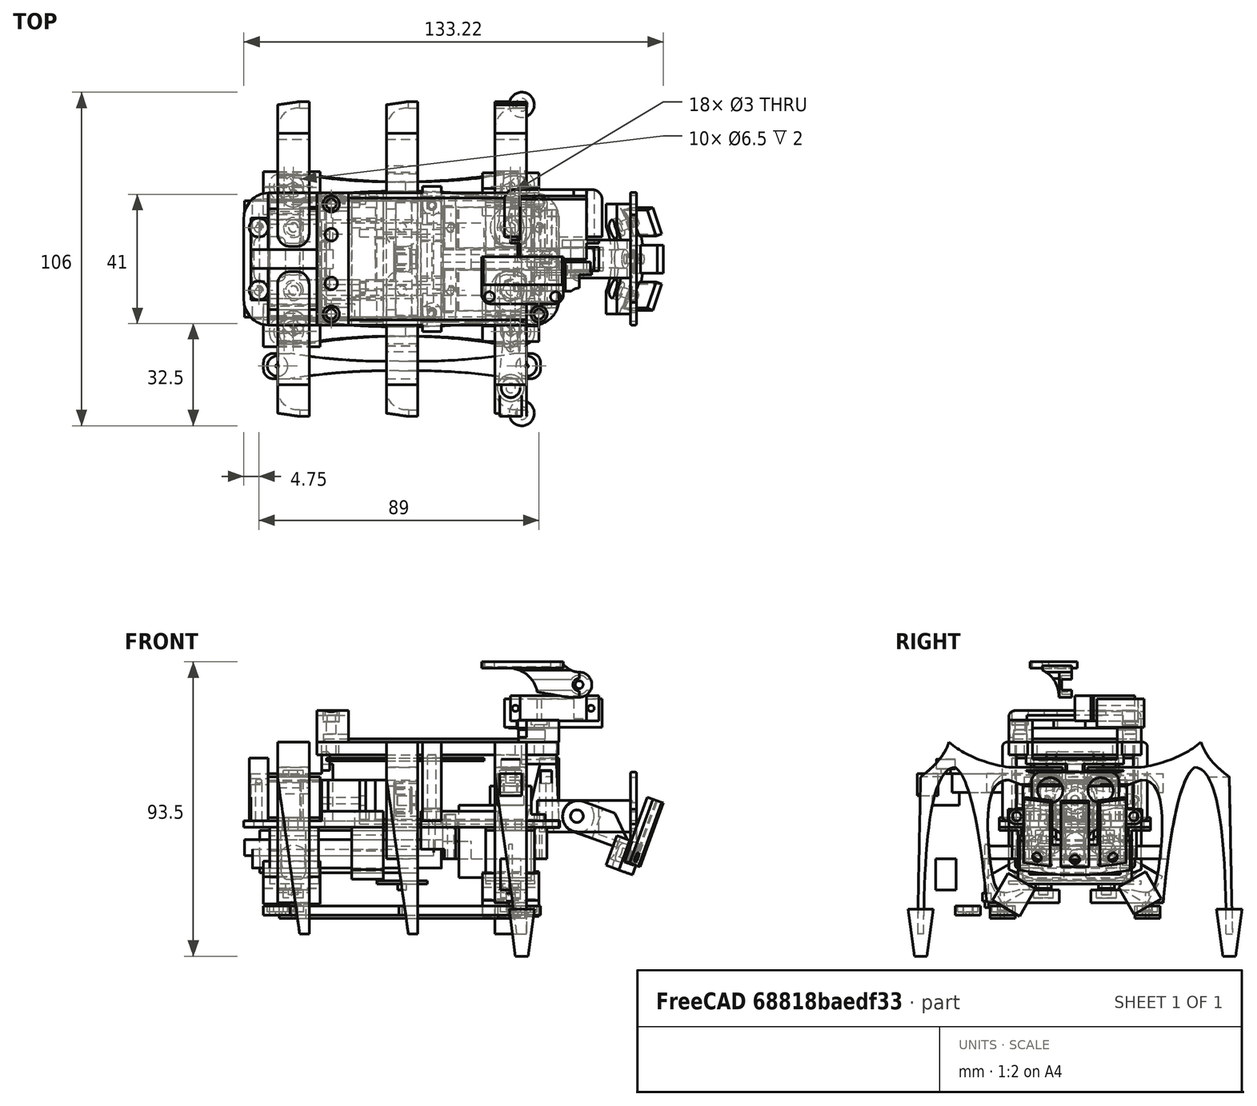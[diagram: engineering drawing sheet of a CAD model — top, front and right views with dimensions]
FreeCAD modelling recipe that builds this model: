
FCSTD DOCUMENT  (FreeCAD 0.20R29410 (Git))
Label: walki_24
License: All rights reserved
LicenseURL: http://en.wikipedia.org/wiki/All_rights_reserved
objects: Part::Cylinder×253, Part::Box×178, Part::MultiFuse×142, Part::Cut×92, Part::Fillet×64, App::DocumentObjectGroup×31, Part::Chamfer×26, Sketcher::SketchObject×17, PartDesign::Pad×17, PartDesign::Body×15, Part::Mirroring×10, Part::Wedge×7, App::Part×3, Part::Cone×2, Image::ImagePlane×1, Part::Feature×1, Part::FeaturePython×1, Mesh::Feature×1
note: 842 computed .brp shape members not serialized (recipe doc carries the construction recipe); baked Part::Feature solids carry a one-line shape summary decoded from their .brp

FEATURE [Part::Box] Box  label="Würfel"
  AttacherType = Attacher::AttachEngine3D
  Height = 23
  Length = 23
  Width = 13
FEATURE [Part::Box] Box001  label="Würfel001"
  AttacherType = Attacher::AttachEngine3D
  Height = 2
  Length = 32
  Placement = pos=(-4.5,0,18) rot=(0,0,1;0rad)
  Width = 13
FEATURE [Part::Cylinder] Cylinder  label="Zylinder"
  Angle = 360
  AttacherType = Attacher::AttachEngine3D
  FirstAngle = 0
  Height = 6
  Placement = pos=(16.5,6.5,23) rot=(0,0,1;0rad)
  Radius = 6.5
  SecondAngle = 0
FEATURE [Part::Cylinder] Cylinder001  label="Zylinder001"
  Angle = 360
  AttacherType = Attacher::AttachEngine3D
  FirstAngle = 0
  Height = 5
  Placement = pos=(16.5,6.5,30) rot=(0,0,1;0rad)
  Radius = 1.5
  SecondAngle = 0
FEATURE [Part::Cylinder] Cylinder002  label="Zylinder002"
  Angle = 360
  AttacherType = Attacher::AttachEngine3D
  FirstAngle = 0
  Height = 10
  Placement = pos=(25.5,6.5,13) rot=(0,0,1;0rad)
  Radius = 1.5
  SecondAngle = 0
FEATURE [Part::Cylinder] Cylinder003  label="Zylinder003"
  Angle = 360
  AttacherType = Attacher::AttachEngine3D
  FirstAngle = 0
  Height = 10
  Placement = pos=(-2.5,6.5,13) rot=(0,0,1;0rad)
  Radius = 1.5
  SecondAngle = 0
FEATURE [Part::Cylinder] Cylinder004  label="Zylinder004"
  Angle = 360
  AttacherType = Attacher::AttachEngine3D
  FirstAngle = 0
  Height = 5
  Placement = pos=(16.5,6.5,29) rot=(0,0,1;0rad)
  Radius = 3.5
  SecondAngle = 0
FEATURE [Part::MultiFuse] Fusion
  Shapes = -> [Cylinder003,Cylinder002,Cylinder001]
FEATURE [Part::MultiFuse] Fusion001
  Shapes = -> [Box,Cylinder004,Box001,Cylinder]
FEATURE [Part::Cut] Cut  label="Servo1"
  Base = -> Fusion001
  Placement = pos=(0,3.5,-25) rot=(0,0,1;0rad)
  Tool = -> Fusion
FEATURE [Part::Box] Box002  label="Würfel002"
  AttacherType = Attacher::AttachEngine3D
  Height = 23
  Length = 23
  Width = 13
FEATURE [Part::Cylinder] Cylinder005  label="Zylinder005"
  Angle = 360
  AttacherType = Attacher::AttachEngine3D
  FirstAngle = 0
  Height = 5
  Placement = pos=(16.5,6.5,30) rot=(0,0,1;0rad)
  Radius = 1.5
  SecondAngle = 0
FEATURE [Part::Cylinder] Cylinder006  label="Zylinder006"
  Angle = 360
  AttacherType = Attacher::AttachEngine3D
  FirstAngle = 0
  Height = 10
  Placement = pos=(-2.5,6.5,13) rot=(0,0,1;0rad)
  Radius = 1.5
  SecondAngle = 0
FEATURE [Part::Cylinder] Cylinder007  label="Zylinder007"
  Angle = 360
  AttacherType = Attacher::AttachEngine3D
  FirstAngle = 0
  Height = 10
  Placement = pos=(25.5,6.5,13) rot=(0,0,1;0rad)
  Radius = 1.5
  SecondAngle = 0
FEATURE [Part::MultiFuse] Fusion003
  Shapes = -> [Cylinder006,Cylinder007,Cylinder005]
FEATURE [Part::Cylinder] Cylinder008  label="Zylinder008"
  Angle = 360
  AttacherType = Attacher::AttachEngine3D
  FirstAngle = 0
  Height = 5
  Placement = pos=(16.5,6.5,29) rot=(0,0,1;0rad)
  Radius = 3.5
  SecondAngle = 0
FEATURE [Part::Box] Box003  label="Würfel003"
  AttacherType = Attacher::AttachEngine3D
  Height = 2
  Length = 32
  Placement = pos=(-4.5,0,18) rot=(0,0,1;0rad)
  Width = 13
FEATURE [Part::Cylinder] Cylinder009  label="Zylinder009"
  Angle = 360
  AttacherType = Attacher::AttachEngine3D
  FirstAngle = 0
  Height = 6
  Placement = pos=(16.5,6.5,23) rot=(0,0,1;0rad)
  Radius = 6.5
  SecondAngle = 0
FEATURE [Part::MultiFuse] Fusion002
  Shapes = -> [Box002,Cylinder008,Box003,Cylinder009]
FEATURE [Part::Cut] Cut001  label="Servo2"
  Base = -> Fusion002
  Placement = pos=(0,-16.5,-25) rot=(0,0,1;0rad)
  Tool = -> Fusion003
FEATURE [Part::Cylinder] Cylinder010  label="Zylinder010"
  Angle = 360
  AttacherType = Attacher::AttachEngine3D
  FirstAngle = 0
  Height = 10
  Placement = pos=(25.5,6.5,13) rot=(0,0,1;0rad)
  Radius = 1.5
  SecondAngle = 0
FEATURE [Part::Cylinder] Cylinder011  label="Zylinder011"
  Angle = 360
  AttacherType = Attacher::AttachEngine3D
  FirstAngle = 0
  Height = 5
  Placement = pos=(16.5,6.5,29) rot=(0,0,1;0rad)
  Radius = 3.5
  SecondAngle = 0
FEATURE [Part::Box] Box004  label="Würfel004"
  AttacherType = Attacher::AttachEngine3D
  Height = 2
  Length = 32
  Placement = pos=(-4.5,0,18) rot=(0,0,1;0rad)
  Width = 13
FEATURE [Part::Cylinder] Cylinder012  label="Zylinder012"
  Angle = 360
  AttacherType = Attacher::AttachEngine3D
  FirstAngle = 0
  Height = 6
  Placement = pos=(16.5,6.5,23) rot=(0,0,1;0rad)
  Radius = 6.5
  SecondAngle = 0
FEATURE [Part::Cylinder] Cylinder013  label="Zylinder013"
  Angle = 360
  AttacherType = Attacher::AttachEngine3D
  FirstAngle = 0
  Height = 5
  Placement = pos=(16.5,6.5,30) rot=(0,0,1;0rad)
  Radius = 1.5
  SecondAngle = 0
FEATURE [Part::Cylinder] Cylinder014  label="Zylinder014"
  Angle = 360
  AttacherType = Attacher::AttachEngine3D
  FirstAngle = 0
  Height = 10
  Placement = pos=(-2.5,6.5,13) rot=(0,0,1;0rad)
  Radius = 1.5
  SecondAngle = 0
FEATURE [Part::MultiFuse] Fusion004
  Shapes = -> [Cylinder014,Cylinder010,Cylinder013]
FEATURE [Part::Box] Box005  label="Würfel005"
  AttacherType = Attacher::AttachEngine3D
  Height = 23
  Length = 23
  Width = 13
FEATURE [Part::MultiFuse] Fusion005
  Shapes = -> [Box005,Cylinder011,Box004,Cylinder012]
FEATURE [Part::Cut] Cut002  label="Servo3"
  Base = -> Fusion005
  Placement = pos=(-49.5,16.5,6) rot=(0.57735,-0.57735,0.57735;4.18879rad)
  Tool = -> Fusion004
FEATURE [Part::Box] Box006  label="Würfel006"
  AttacherType = Attacher::AttachEngine3D
  Height = 18
  Length = 17.5
  Placement = pos=(7.5,-21.5,-28) rot=(0,0,1;0rad)
  Width = 3.5
FEATURE [Part::Box] Box007  label="Base"
  AttacherType = Attacher::AttachEngine3D
  Height = 2
  Length = 100
  Placement = pos=(-68.25,-21,-9) rot=(0,0,1;0rad)
  Width = 42
FEATURE [Part::Cylinder] Cylinder015  label="Zylinder015"
  Angle = 360
  AttacherType = Attacher::AttachEngine3D
  FirstAngle = 0
  Height = 2.5
  Placement = pos=(16.5,10,-29.5) rot=(0,0,1;0rad)
  Radius = 1.4
  SecondAngle = 0
FEATURE [Part::Cylinder] Cylinder016  label="Zylinder016"
  Angle = 360
  AttacherType = Attacher::AttachEngine3D
  FirstAngle = 0
  Height = 2.5
  Placement = pos=(16.5,-10,-29.5) rot=(0,0,1;0rad)
  Radius = 1.4
  SecondAngle = 0
FEATURE [Part::Box] Box008  label="Würfel008"
  AttacherType = Attacher::AttachEngine3D
  Height = 1
  Length = 16
  Placement = pos=(8.5,-21,-27.5) rot=(0,0,1;0rad)
  Width = 42
FEATURE [Part::Cylinder] Cylinder017  label="Zylinder017"
  Angle = 360
  AttacherType = Attacher::AttachEngine3D
  FirstAngle = 0
  Height = 2
  Placement = pos=(16.5,10,-29.5) rot=(0,0,1;0rad)
  Radius = 1.4
  SecondAngle = 0
FEATURE [Part::Cylinder] Cylinder018  label="Zylinder018"
  Angle = 360
  AttacherType = Attacher::AttachEngine3D
  FirstAngle = 0
  Height = 2
  Placement = pos=(16.5,-10,-29.5) rot=(0,0,1;0rad)
  Radius = 1.4
  SecondAngle = 0
FEATURE [Part::MultiFuse] Fusion007
  Placement = pos=(-34.5,0,0.5) rot=(0,0,1;0rad)
  Shapes = -> [Box008,Cylinder017,Cylinder018]
FEATURE [Part::Cylinder] Cylinder021  label="Zylinder021"
  Angle = 360
  AttacherType = Attacher::AttachEngine3D
  FirstAngle = 0
  Height = 2
  Placement = pos=(16.5,10,-26.5) rot=(0,0,1;0rad)
  Radius = 1.4
  SecondAngle = 0
FEATURE [Part::Cylinder] Cylinder022  label="Zylinder022"
  Angle = 360
  AttacherType = Attacher::AttachEngine3D
  FirstAngle = 0
  Height = 2
  Placement = pos=(16.5,-10,-26.5) rot=(0,0,1;0rad)
  Radius = 1.4
  SecondAngle = 0
FEATURE [Part::Box] Box010  label="Würfel010"
  AttacherType = Attacher::AttachEngine3D
  Height = 1
  Length = 16
  Placement = pos=(8.5,-16,-27.5) rot=(0,0,1;0rad)
  Width = 32
FEATURE [Part::Box] Box012  label="Würfel012"
  AttacherType = Attacher::AttachEngine3D
  Height = 14
  Length = 12
  Placement = pos=(-43.5,-21,-8) rot=(0,0,1;0rad)
  Width = 42
FEATURE [Part::Cylinder] Cylinder023  label="Zylinder023"
  Angle = 360
  AttacherType = Attacher::AttachEngine3D
  FirstAngle = 0
  Height = 20
  Placement = pos=(-45,-9,-1.5) rot=(0,1,0;1.5708rad)
  Radius = 1
  SecondAngle = 0
FEATURE [Part::Cylinder] Cylinder024  label="Zylinder024"
  Angle = 360
  AttacherType = Attacher::AttachEngine3D
  FirstAngle = 0
  Height = 20
  Placement = pos=(-45,19,-1.5) rot=(0,1,0;1.5708rad)
  Radius = 1
  SecondAngle = 0
FEATURE [Part::MultiFuse] Fusion010
  Shapes = -> [Cylinder023,Cylinder024]
FEATURE [Part::Cylinder] Cylinder026  label="Zylinder026"
  Angle = 360
  AttacherType = Attacher::AttachEngine3D
  FirstAngle = 0
  Height = 5
  Placement = pos=(16.5,6.5,30) rot=(0,0,1;0rad)
  Radius = 1.5
  SecondAngle = 0
FEATURE [Part::Box] Box014  label="Würfel014"
  AttacherType = Attacher::AttachEngine3D
  Height = 23
  Length = 23
  Width = 13
FEATURE [Part::Cylinder] Cylinder027  label="Zylinder027"
  Angle = 360
  AttacherType = Attacher::AttachEngine3D
  FirstAngle = 0
  Height = 5
  Placement = pos=(16.5,6.5,29) rot=(0,0,1;0rad)
  Radius = 3.5
  SecondAngle = 0
FEATURE [Part::Cylinder] Cylinder028  label="Zylinder028"
  Angle = 360
  AttacherType = Attacher::AttachEngine3D
  FirstAngle = 0
  Height = 6
  Placement = pos=(16.5,6.5,23) rot=(0,0,1;0rad)
  Radius = 6.5
  SecondAngle = 0
FEATURE [Part::Cylinder] Cylinder029  label="Zylinder029"
  Angle = 360
  AttacherType = Attacher::AttachEngine3D
  FirstAngle = 0
  Height = 10
  Placement = pos=(25.5,6.5,13) rot=(0,0,1;0rad)
  Radius = 1.5
  SecondAngle = 0
FEATURE [Part::Cylinder] Cylinder030  label="Zylinder030"
  Angle = 360
  AttacherType = Attacher::AttachEngine3D
  FirstAngle = 0
  Height = 10
  Placement = pos=(-2.5,6.5,13) rot=(0,0,1;0rad)
  Radius = 1.5
  SecondAngle = 0
FEATURE [Part::MultiFuse] Fusion013
  Shapes = -> [Cylinder030,Cylinder029,Cylinder026]
FEATURE [Part::Box] Box015  label="Würfel015"
  AttacherType = Attacher::AttachEngine3D
  Height = 2
  Length = 32
  Placement = pos=(-4.5,0,18) rot=(0,0,1;0rad)
  Width = 13
FEATURE [Part::MultiFuse] Fusion012
  Shapes = -> [Box014,Cylinder027,Box015,Cylinder028]
FEATURE [Part::Cut] Cut005  label="Servo3_mask"
  Base = -> Fusion012
  Placement = pos=(-49.5,16.5,5) rot=(0.57735,-0.57735,0.57735;4.18879rad)
  Tool = -> Fusion013
FEATURE [Part::Box] Box016  label="Würfel016"
  AttacherType = Attacher::AttachEngine3D
  Height = 23
  Length = 23
  Width = 13
FEATURE [Part::Cylinder] Cylinder031  label="Zylinder031"
  Angle = 360
  AttacherType = Attacher::AttachEngine3D
  FirstAngle = 0
  Height = 5
  Placement = pos=(16.5,6.5,30) rot=(0,0,1;0rad)
  Radius = 1.5
  SecondAngle = 0
FEATURE [Part::Cylinder] Cylinder032  label="Zylinder032"
  Angle = 360
  AttacherType = Attacher::AttachEngine3D
  FirstAngle = 0
  Height = 10
  Placement = pos=(-2.5,6.5,13) rot=(0,0,1;0rad)
  Radius = 1.5
  SecondAngle = 0
FEATURE [Part::Cylinder] Cylinder033  label="Zylinder033"
  Angle = 360
  AttacherType = Attacher::AttachEngine3D
  FirstAngle = 0
  Height = 10
  Placement = pos=(25.5,6.5,13) rot=(0,0,1;0rad)
  Radius = 1.5
  SecondAngle = 0
FEATURE [Part::MultiFuse] Fusion015
  Shapes = -> [Cylinder032,Cylinder033,Cylinder031]
FEATURE [Part::Cylinder] Cylinder034  label="Zylinder034"
  Angle = 360
  AttacherType = Attacher::AttachEngine3D
  FirstAngle = 0
  Height = 5
  Placement = pos=(16.5,6.5,29) rot=(0,0,1;0rad)
  Radius = 3.5
  SecondAngle = 0
FEATURE [Part::Box] Box017  label="Würfel017"
  AttacherType = Attacher::AttachEngine3D
  Height = 2
  Length = 32
  Placement = pos=(-4.5,0,18) rot=(0,0,1;0rad)
  Width = 13
FEATURE [Part::Cylinder] Cylinder035  label="Zylinder035"
  Angle = 360
  AttacherType = Attacher::AttachEngine3D
  FirstAngle = 0
  Height = 6
  Placement = pos=(16.5,6.5,23) rot=(0,0,1;0rad)
  Radius = 6.5
  SecondAngle = 0
FEATURE [Part::MultiFuse] Fusion014
  Shapes = -> [Box016,Cylinder034,Box017,Cylinder035]
FEATURE [Part::Cut] Cut007  label="Servo1_mask"
  Base = -> Fusion014
  Placement = pos=(0,3.5,-25) rot=(0,0,1;0rad)
  Tool = -> Fusion015
FEATURE [Part::Cylinder] Cylinder036  label="Zylinder036"
  Angle = 360
  AttacherType = Attacher::AttachEngine3D
  FirstAngle = 0
  Height = 10
  Placement = pos=(25.5,6.5,13) rot=(0,0,1;0rad)
  Radius = 1.5
  SecondAngle = 0
FEATURE [Part::Cylinder] Cylinder037  label="Zylinder037"
  Angle = 360
  AttacherType = Attacher::AttachEngine3D
  FirstAngle = 0
  Height = 5
  Placement = pos=(16.5,6.5,29) rot=(0,0,1;0rad)
  Radius = 3.5
  SecondAngle = 0
FEATURE [Part::Box] Box018  label="Würfel018"
  AttacherType = Attacher::AttachEngine3D
  Height = 2
  Length = 32
  Placement = pos=(-4.5,0,18) rot=(0,0,1;0rad)
  Width = 13
FEATURE [Part::Cylinder] Cylinder038  label="Zylinder038"
  Angle = 360
  AttacherType = Attacher::AttachEngine3D
  FirstAngle = 0
  Height = 6
  Placement = pos=(16.5,6.5,23) rot=(0,0,1;0rad)
  Radius = 6.5
  SecondAngle = 0
FEATURE [Part::Cylinder] Cylinder039  label="Zylinder039"
  Angle = 360
  AttacherType = Attacher::AttachEngine3D
  FirstAngle = 0
  Height = 5
  Placement = pos=(16.5,6.5,30) rot=(0,0,1;0rad)
  Radius = 1.5
  SecondAngle = 0
FEATURE [Part::Cylinder] Cylinder040  label="Zylinder040"
  Angle = 360
  AttacherType = Attacher::AttachEngine3D
  FirstAngle = 0
  Height = 10
  Placement = pos=(-2.5,6.5,13) rot=(0,0,1;0rad)
  Radius = 1.5
  SecondAngle = 0
FEATURE [Part::MultiFuse] Fusion016
  Shapes = -> [Cylinder040,Cylinder036,Cylinder039]
FEATURE [Part::Box] Box019  label="Würfel019"
  AttacherType = Attacher::AttachEngine3D
  Height = 23
  Length = 23
  Width = 13
FEATURE [Part::MultiFuse] Fusion017
  Shapes = -> [Box019,Cylinder037,Box018,Cylinder038]
FEATURE [Part::Cut] Cut008  label="Servo2_mask"
  Base = -> Fusion017
  Placement = pos=(0,-16.5,-25) rot=(0,0,1;0rad)
  Tool = -> Fusion016
FEATURE [Part::Box] Box020  label="Würfel020"
  AttacherType = Attacher::AttachEngine3D
  Height = 18
  Length = 15.5
  Placement = pos=(8.5,-21,-27) rot=(0,0,1;0rad)
  Width = 42
FEATURE [Part::Box] Box021  label="Würfel021"
  AttacherType = Attacher::AttachEngine3D
  Height = 18
  Length = 17.5
  Placement = pos=(7.5,18,-28) rot=(0,0,1;0rad)
  Width = 3.5
FEATURE [Part::MultiFuse] Fusion018
  Shapes = -> [Box006,Box021]
FEATURE [Part::Cut] Cut009
  Base = -> Box020
  Tool = -> Fusion018
FEATURE [Part::Cylinder] Cylinder041  label="Zylinder041"
  Angle = 360
  AttacherType = Attacher::AttachEngine3D
  FirstAngle = 0
  Height = 10
  Placement = pos=(16.5,20.5,-14) rot=(0,0,1;0rad)
  Radius = 1.5
  SecondAngle = 0
FEATURE [Part::Cylinder] Cylinder042  label="Zylinder042"
  Angle = 360
  AttacherType = Attacher::AttachEngine3D
  FirstAngle = 0
  Height = 1
  Placement = pos=(16.5,20.5,-10) rot=(0,0,1;0rad)
  Radius = 3.5
  SecondAngle = 0
FEATURE [Part::Cylinder] Cylinder043  label="Zylinder043"
  Angle = 360
  AttacherType = Attacher::AttachEngine3D
  FirstAngle = 0
  Height = 2
  Placement = pos=(16.5,20.5,-9) rot=(0,0,1;0rad)
  Radius = 3.5
  SecondAngle = 0
FEATURE [Part::Cylinder] Cylinder044  label="Zylinder044"
  Angle = 360
  AttacherType = Attacher::AttachEngine3D
  FirstAngle = 0
  Height = 2
  Placement = pos=(16.5,-20.5,-9) rot=(0,0,1;0rad)
  Radius = 3.5
  SecondAngle = 0
FEATURE [Part::Cylinder] Cylinder045  label="Zylinder045"
  Angle = 360
  AttacherType = Attacher::AttachEngine3D
  FirstAngle = 0
  Height = 1
  Placement = pos=(16.5,-20.5,-10) rot=(0,0,1;0rad)
  Radius = 3.5
  SecondAngle = 0
FEATURE [Part::Cylinder] Cylinder046  label="Zylinder046"
  Angle = 360
  AttacherType = Attacher::AttachEngine3D
  FirstAngle = 0
  Height = 10
  Placement = pos=(16.5,-20.5,-14) rot=(0,0,1;0rad)
  Radius = 1.5
  SecondAngle = 0
FEATURE [Part::MultiFuse] Fusion019
  Shapes = -> [Cylinder045,Cylinder042,Cylinder016,Cylinder015]
FEATURE [Part::Cylinder] Cylinder047  label="Zylinder047"
  Angle = 360
  AttacherType = Attacher::AttachEngine3D
  FirstAngle = 0
  Height = 10
  Placement = pos=(16.5,-20.5,-14) rot=(0,0,1;0rad)
  Radius = 1.5
  SecondAngle = 0
FEATURE [Part::Cylinder] Cylinder048  label="Zylinder048"
  Angle = 360
  AttacherType = Attacher::AttachEngine3D
  FirstAngle = 0
  Height = 10
  Placement = pos=(16.5,20.5,-14) rot=(0,0,1;0rad)
  Radius = 1.5
  SecondAngle = 0
FEATURE [Part::Box] Box022  label="Würfel022"
  AttacherType = Attacher::AttachEngine3D
  Height = 21
  Length = 22
  Placement = pos=(1,-4,-26) rot=(0,0,1;0rad)
  Width = 8
FEATURE [Part::MultiFuse] Fusion021
  Shapes = -> [Cylinder041,Cylinder046,Box022]
FEATURE [Part::MultiFuse] Fusion022
  Shapes = -> [Cut007,Cut008]
FEATURE [Part::Box] Box023  label="Würfel023"
  AttacherType = Attacher::AttachEngine3D
  Height = 2
  Length = 32
  Placement = pos=(-4.5,0,18) rot=(0,0,1;0rad)
  Width = 13
FEATURE [Part::Box] Box024  label="Würfel024"
  AttacherType = Attacher::AttachEngine3D
  Height = 2
  Length = 32
  Placement = pos=(-4.5,0,18) rot=(0,0,1;0rad)
  Width = 13
FEATURE [Part::Cylinder] Cylinder049  label="Zylinder049"
  Angle = 360
  AttacherType = Attacher::AttachEngine3D
  FirstAngle = 0
  Height = 5
  Placement = pos=(16.5,6.5,29) rot=(0,0,1;0rad)
  Radius = 3.5
  SecondAngle = 0
FEATURE [Part::Cylinder] Cylinder050  label="Zylinder050"
  Angle = 360
  AttacherType = Attacher::AttachEngine3D
  FirstAngle = 0
  Height = 10
  Placement = pos=(-2.5,6.5,13) rot=(0,0,1;0rad)
  Radius = 1.5
  SecondAngle = 0
FEATURE [Part::Cylinder] Cylinder051  label="Zylinder051"
  Angle = 360
  AttacherType = Attacher::AttachEngine3D
  FirstAngle = 0
  Height = 10
  Placement = pos=(25.5,6.5,13) rot=(0,0,1;0rad)
  Radius = 1.5
  SecondAngle = 0
FEATURE [Part::Box] Box025  label="Würfel025"
  AttacherType = Attacher::AttachEngine3D
  Height = 23
  Length = 23
  Width = 13
FEATURE [Part::Cylinder] Cylinder052  label="Zylinder052"
  Angle = 360
  AttacherType = Attacher::AttachEngine3D
  FirstAngle = 0
  Height = 5
  Placement = pos=(16.5,6.5,30) rot=(0,0,1;0rad)
  Radius = 1.5
  SecondAngle = 0
FEATURE [Part::Cylinder] Cylinder053  label="Zylinder053"
  Angle = 360
  AttacherType = Attacher::AttachEngine3D
  FirstAngle = 0
  Height = 6
  Placement = pos=(16.5,6.5,23) rot=(0,0,1;0rad)
  Radius = 6.5
  SecondAngle = 0
FEATURE [Part::Cylinder] Cylinder054  label="Zylinder054"
  Angle = 360
  AttacherType = Attacher::AttachEngine3D
  FirstAngle = 0
  Height = 5
  Placement = pos=(16.5,6.5,29) rot=(0,0,1;0rad)
  Radius = 3.5
  SecondAngle = 0
FEATURE [Part::Cylinder] Cylinder055  label="Zylinder055"
  Angle = 360
  AttacherType = Attacher::AttachEngine3D
  FirstAngle = 0
  Height = 6
  Placement = pos=(16.5,6.5,23) rot=(0,0,1;0rad)
  Radius = 6.5
  SecondAngle = 0
FEATURE [Part::Cylinder] Cylinder056  label="Zylinder056"
  Angle = 360
  AttacherType = Attacher::AttachEngine3D
  FirstAngle = 0
  Height = 10
  Placement = pos=(25.5,6.5,13) rot=(0,0,1;0rad)
  Radius = 1.5
  SecondAngle = 0
FEATURE [Part::Cylinder] Cylinder057  label="Zylinder057"
  Angle = 360
  AttacherType = Attacher::AttachEngine3D
  FirstAngle = 0
  Height = 10
  Placement = pos=(-2.5,6.5,13) rot=(0,0,1;0rad)
  Radius = 1.5
  SecondAngle = 0
FEATURE [Part::Box] Box026  label="Würfel026"
  AttacherType = Attacher::AttachEngine3D
  Height = 23
  Length = 23
  Width = 13
FEATURE [Part::Cylinder] Cylinder058  label="Zylinder058"
  Angle = 360
  AttacherType = Attacher::AttachEngine3D
  FirstAngle = 0
  Height = 5
  Placement = pos=(16.5,6.5,30) rot=(0,0,1;0rad)
  Radius = 1.5
  SecondAngle = 0
FEATURE [Part::MultiFuse] Fusion024
  Shapes = -> [Box025,Cylinder054,Box024,Cylinder055]
FEATURE [Part::MultiFuse] Fusion025
  Shapes = -> [Cylinder050,Cylinder051,Cylinder052]
FEATURE [Part::Cut] Cut012  label="Servo2_mask001"
  Base = -> Fusion024
  Placement = pos=(0,-16.5,-26) rot=(0,0,1;0rad)
  Tool = -> Fusion025
FEATURE [Part::MultiFuse] Fusion026
  Shapes = -> [Cylinder057,Cylinder056,Cylinder058]
FEATURE [Part::MultiFuse] Fusion027
  Shapes = -> [Box026,Cylinder049,Box023,Cylinder053]
FEATURE [Part::Cut] Cut011  label="Servo1_mask001"
  Base = -> Fusion027
  Placement = pos=(0,3.5,-26) rot=(0,0,1;0rad)
  Tool = -> Fusion026
FEATURE [Part::MultiFuse] Fusion023
  Shapes = -> [Cut011,Cut012]
FEATURE [Part::Box] Box028  label="Würfel028"
  AttacherType = Attacher::AttachEngine3D
  Height = 18
  Length = 17.5
  Placement = pos=(7.5,-21.5,-28) rot=(0,0,1;0rad)
  Width = 3.5
FEATURE [Part::Cylinder] Cylinder059  label="Zylinder059"
  Angle = 360
  AttacherType = Attacher::AttachEngine3D
  FirstAngle = 0
  Height = 2.5
  Placement = pos=(16.5,10,-29.5) rot=(0,0,1;0rad)
  Radius = 1.4
  SecondAngle = 0
FEATURE [Part::Cylinder] Cylinder060  label="Zylinder060"
  Angle = 360
  AttacherType = Attacher::AttachEngine3D
  FirstAngle = 0
  Height = 2.5
  Placement = pos=(16.5,-10,-29.5) rot=(0,0,1;0rad)
  Radius = 1.4
  SecondAngle = 0
FEATURE [Part::Cylinder] Cylinder061  label="Zylinder061"
  Angle = 360
  AttacherType = Attacher::AttachEngine3D
  FirstAngle = 0
  Height = 5
  Placement = pos=(16.5,6.5,29) rot=(0,0,1;0rad)
  Radius = 3.5
  SecondAngle = 0
FEATURE [Part::Box] Box029  label="Würfel029"
  AttacherType = Attacher::AttachEngine3D
  Height = 23
  Length = 23
  Width = 13
FEATURE [Part::Cylinder] Cylinder062  label="Zylinder062"
  Angle = 360
  AttacherType = Attacher::AttachEngine3D
  FirstAngle = 0
  Height = 6
  Placement = pos=(16.5,6.5,23) rot=(0,0,1;0rad)
  Radius = 6.5
  SecondAngle = 0
FEATURE [Part::Cylinder] Cylinder063  label="Zylinder063"
  Angle = 360
  AttacherType = Attacher::AttachEngine3D
  FirstAngle = 0
  Height = 5
  Placement = pos=(16.5,6.5,29) rot=(0,0,1;0rad)
  Radius = 3.5
  SecondAngle = 0
FEATURE [Part::Box] Box030  label="Würfel030"
  AttacherType = Attacher::AttachEngine3D
  Height = 18
  Length = 17.5
  Placement = pos=(7.5,18,-28) rot=(0,0,1;0rad)
  Width = 3.5
FEATURE [Part::Box] Box031  label="Würfel031"
  AttacherType = Attacher::AttachEngine3D
  Height = 2
  Length = 32
  Placement = pos=(-4.5,0,18) rot=(0,0,1;0rad)
  Width = 13
FEATURE [Part::Cylinder] Cylinder064  label="Zylinder064"
  Angle = 360
  AttacherType = Attacher::AttachEngine3D
  FirstAngle = 0
  Height = 10
  Placement = pos=(16.5,-20.5,-14) rot=(0,0,1;0rad)
  Radius = 1.5
  SecondAngle = 0
FEATURE [Part::Box] Box032  label="Würfel032"
  AttacherType = Attacher::AttachEngine3D
  Height = 2
  Length = 32
  Placement = pos=(-4.5,0,18) rot=(0,0,1;0rad)
  Width = 13
FEATURE [Part::Cylinder] Cylinder065  label="Zylinder065"
  Angle = 360
  AttacherType = Attacher::AttachEngine3D
  FirstAngle = 0
  Height = 10
  Placement = pos=(25.5,6.5,13) rot=(0,0,1;0rad)
  Radius = 1.5
  SecondAngle = 0
FEATURE [Part::Cylinder] Cylinder066  label="Zylinder066"
  Angle = 360
  AttacherType = Attacher::AttachEngine3D
  FirstAngle = 0
  Height = 10
  Placement = pos=(16.5,20.5,-14) rot=(0,0,1;0rad)
  Radius = 1.5
  SecondAngle = 0
FEATURE [Part::Cylinder] Cylinder067  label="Zylinder067"
  Angle = 360
  AttacherType = Attacher::AttachEngine3D
  FirstAngle = 0
  Height = 10
  Placement = pos=(25.5,6.5,13) rot=(0,0,1;0rad)
  Radius = 1.5
  SecondAngle = 0
FEATURE [Part::Cylinder] Cylinder068  label="Zylinder068"
  Angle = 360
  AttacherType = Attacher::AttachEngine3D
  FirstAngle = 0
  Height = 1
  Placement = pos=(16.5,20.5,-10) rot=(0,0,1;0rad)
  Radius = 3.5
  SecondAngle = 0
FEATURE [Part::Cylinder] Cylinder069  label="Zylinder069"
  Angle = 360
  AttacherType = Attacher::AttachEngine3D
  FirstAngle = 0
  Height = 10
  Placement = pos=(-2.5,6.5,13) rot=(0,0,1;0rad)
  Radius = 1.5
  SecondAngle = 0
FEATURE [Part::Box] Box033  label="Würfel033"
  AttacherType = Attacher::AttachEngine3D
  Height = 23
  Length = 23
  Width = 13
FEATURE [Part::Cylinder] Cylinder070  label="Zylinder070"
  Angle = 360
  AttacherType = Attacher::AttachEngine3D
  FirstAngle = 0
  Height = 10
  Placement = pos=(-2.5,6.5,13) rot=(0,0,1;0rad)
  Radius = 1.5
  SecondAngle = 0
FEATURE [Part::Box] Box036  label="Würfel036"
  AttacherType = Attacher::AttachEngine3D
  Height = 18
  Length = 15.5
  Placement = pos=(-60,-21,-27) rot=(0,0,1;0rad)
  Width = 42
FEATURE [Part::Cylinder] Cylinder071  label="Zylinder071"
  Angle = 360
  AttacherType = Attacher::AttachEngine3D
  FirstAngle = 0
  Height = 5
  Placement = pos=(16.5,6.5,30) rot=(0,0,1;0rad)
  Radius = 1.5
  SecondAngle = 0
FEATURE [Part::Cylinder] Cylinder072  label="Zylinder072"
  Angle = 360
  AttacherType = Attacher::AttachEngine3D
  FirstAngle = 0
  Height = 1
  Placement = pos=(16.5,-20.5,-10) rot=(0,0,1;0rad)
  Radius = 3.5
  SecondAngle = 0
FEATURE [Part::Cylinder] Cylinder073  label="Zylinder073"
  Angle = 360
  AttacherType = Attacher::AttachEngine3D
  FirstAngle = 0
  Height = 6
  Placement = pos=(16.5,6.5,23) rot=(0,0,1;0rad)
  Radius = 6.5
  SecondAngle = 0
FEATURE [Part::Cylinder] Cylinder074  label="Zylinder074"
  Angle = 360
  AttacherType = Attacher::AttachEngine3D
  FirstAngle = 0
  Height = 5
  Placement = pos=(16.5,6.5,30) rot=(0,0,1;0rad)
  Radius = 1.5
  SecondAngle = 0
FEATURE [Part::MultiFuse] Fusion030
  Placement = pos=(-69,0,0) rot=(0,0,1;0rad)
  Shapes = -> [Cylinder072,Cylinder068,Cylinder060,Cylinder059]
FEATURE [Part::MultiFuse] Fusion033
  Shapes = -> [Box033,Cylinder061,Box032,Cylinder073]
FEATURE [Part::MultiFuse] Fusion034
  Shapes = -> [Box029,Cylinder063,Box031,Cylinder062]
FEATURE [Part::MultiFuse] Fusion035
  Shapes = -> [Cylinder069,Cylinder067,Cylinder071]
FEATURE [Part::Cut] Cut021  label="Servo2_mask002"
  Base = -> Fusion033
  Placement = pos=(0,-16.5,-26) rot=(0,0,1;0rad)
  Tool = -> Fusion035
FEATURE [Part::MultiFuse] Fusion036
  Shapes = -> [Cylinder070,Cylinder065,Cylinder074]
FEATURE [Part::Cut] Cut016  label="Servo1_mask002"
  Base = -> Fusion034
  Placement = pos=(0,3.5,-26) rot=(0,0,1;0rad)
  Tool = -> Fusion036
FEATURE [Part::MultiFuse] Fusion032
  Shapes = -> [Cut016,Cut021]
FEATURE [Part::MultiFuse] Fusion037
  Placement = pos=(-68.5,0,0) rot=(0,0,1;0rad)
  Shapes = -> [Box028,Box030]
FEATURE [Part::Box] Box035  label="Würfel035"
  AttacherType = Attacher::AttachEngine3D
  Height = 15
  Length = 10
  Placement = pos=(22,-14.5,-24) rot=(0,0,1;0rad)
  Width = 29
FEATURE [Part::Cylinder] Cylinder075  label="Zylinder075"
  Angle = 360
  AttacherType = Attacher::AttachEngine3D
  FirstAngle = 0
  Height = 10
  Placement = pos=(-52.5,-20.5,-14) rot=(0,0,1;0rad)
  Radius = 1.5
  SecondAngle = 0
FEATURE [Part::Cylinder] Cylinder076  label="Zylinder076"
  Angle = 360
  AttacherType = Attacher::AttachEngine3D
  FirstAngle = 0
  Height = 10
  Placement = pos=(-52.5,20.5,-14) rot=(0,0,1;0rad)
  Radius = 1.5
  SecondAngle = 0
FEATURE [Part::Cylinder] Cylinder077  label="Zylinder077"
  Angle = 360
  AttacherType = Attacher::AttachEngine3D
  FirstAngle = 0
  Height = 2
  Placement = pos=(-52.5,20.5,-9) rot=(0,0,1;0rad)
  Radius = 3.5
  SecondAngle = 0
FEATURE [Part::Cylinder] Cylinder078  label="Zylinder078"
  Angle = 360
  AttacherType = Attacher::AttachEngine3D
  FirstAngle = 0
  Height = 2
  Placement = pos=(-52.5,-20.5,-9) rot=(0,0,1;0rad)
  Radius = 3.5
  SecondAngle = 0
FEATURE [Part::Cylinder] Cylinder079  label="Zylinder079"
  Angle = 360
  AttacherType = Attacher::AttachEngine3D
  FirstAngle = 0
  Height = 10
  Placement = pos=(-2.5,10,-13) rot=(0,0,1;0rad)
  Radius = 1.4
  SecondAngle = 0
FEATURE [Part::Cylinder] Cylinder080  label="Zylinder080"
  Angle = 360
  AttacherType = Attacher::AttachEngine3D
  FirstAngle = 0
  Height = 10
  Placement = pos=(25.5,10,-13) rot=(0,0,1;0rad)
  Radius = 1.4
  SecondAngle = 0
FEATURE [Part::Cylinder] Cylinder081  label="Zylinder081"
  Angle = 360
  AttacherType = Attacher::AttachEngine3D
  FirstAngle = 0
  Height = 10
  Placement = pos=(25.5,-10,-13) rot=(0,0,1;0rad)
  Radius = 1.4
  SecondAngle = 0
FEATURE [Part::Cylinder] Cylinder082  label="Zylinder082"
  Angle = 360
  AttacherType = Attacher::AttachEngine3D
  FirstAngle = 0
  Height = 10
  Placement = pos=(-2.5,-10,-13) rot=(0,0,1;0rad)
  Radius = 1.4
  SecondAngle = 0
FEATURE [Part::MultiFuse] Fusion039
  Shapes = -> [Cylinder081,Cylinder080,Cylinder082,Cylinder079,Cylinder075,Cylinder076,Cylinder047,Cylinder048]
FEATURE [Part::MultiFuse] Fusion040
  Shapes = -> [Fusion022,Fusion039]
FEATURE [Part::MultiFuse] Fusion041
  Shapes = -> [Cylinder043,Cylinder044,Box007,Cylinder077,Cylinder078]
FEATURE [Part::Cut] Cut026
  Base = -> Fusion041
  Tool = -> Fusion040
FEATURE [App::DocumentObjectGroup] Gruppe  label="Servos"
  Group = -> [Cut,Cut001,Cut002]
FEATURE [Part::Box] Box038  label="Würfel038"
  AttacherType = Attacher::AttachEngine3D
  Height = 3
  Length = 56
  Placement = pos=(-43.5,20,-7) rot=(0,0,1;0rad)
  Width = 1
FEATURE [Part::Box] Box039  label="Würfel039"
  AttacherType = Attacher::AttachEngine3D
  Height = 3
  Length = 56
  Placement = pos=(-43.5,-21,-7) rot=(0,0,1;0rad)
  Width = 1
FEATURE [Part::Box] Box040  label="Würfel040"
  AttacherType = Attacher::AttachEngine3D
  Height = 10
  Length = 12
  Placement = pos=(-24,-21.5,-11) rot=(0,0,1;0rad)
  Width = 13
FEATURE [Part::Box] Box041  label="Würfel041"
  AttacherType = Attacher::AttachEngine3D
  Height = 10
  Length = 12
  Placement = pos=(-24,8.5,-11) rot=(0,0,1;0rad)
  Width = 13
FEATURE [Part::MultiFuse] Fusion042
  Shapes = -> [Box038,Box039]
FEATURE [Part::MultiFuse] Fusion043
  Shapes = -> [Cut026,Fusion042]
FEATURE [Part::MultiFuse] Fusion044
  Shapes = -> [Box040,Box041]
FEATURE [Part::Cylinder] Cylinder083  label="Zylinder083"
  Angle = 360
  AttacherType = Attacher::AttachEngine3D
  FirstAngle = 0
  Height = 1
  Placement = pos=(-52.5,-20.5,-8) rot=(0,0,1;0rad)
  Radius = 3.5
  SecondAngle = 0
FEATURE [Part::Cylinder] Cylinder084  label="Zylinder084"
  Angle = 360
  AttacherType = Attacher::AttachEngine3D
  FirstAngle = 0
  Height = 1
  Placement = pos=(-52.5,20.5,-8) rot=(0,0,1;0rad)
  Radius = 3.5
  SecondAngle = 0
FEATURE [Part::Cylinder] Cylinder085  label="Zylinder085"
  Angle = 360
  AttacherType = Attacher::AttachEngine3D
  FirstAngle = 0
  Height = 4
  Placement = pos=(-52.5,-20.5,-9.5) rot=(0,0,1;0rad)
  Radius = 1.4
  SecondAngle = 0
FEATURE [Part::Cylinder] Cylinder086  label="Zylinder086"
  Angle = 360
  AttacherType = Attacher::AttachEngine3D
  FirstAngle = 0
  Height = 4
  Placement = pos=(-52.5,20.5,-9.5) rot=(0,0,1;0rad)
  Radius = 1.4
  SecondAngle = 0
FEATURE [Part::MultiFuse] Fusion009
  Placement = pos=(-69,0,32.5) rot=(0,0,1;0rad)
  Shapes = -> [Box010,Cylinder021,Cylinder022]
FEATURE [Part::Box] Box042  label="Würfel042"
  AttacherType = Attacher::AttachEngine3D
  Height = 14
  Length = 16.5
  Placement = pos=(-60.5,-21,-8) rot=(0,0,1;0rad)
  Width = 42
FEATURE [Part::Box] Box043  label="Würfel043"
  AttacherType = Attacher::AttachEngine3D
  Height = 12.5
  Length = 18
  Placement = pos=(-61.5,-14.5,-8) rot=(0,0,1;0rad)
  Width = 29
FEATURE [Part::Box] Box044  label="Würfel044"
  AttacherType = Attacher::AttachEngine3D
  Height = 17
  Length = 18
  Placement = pos=(-61.5,-22,-7) rot=(0,0,1;0rad)
  Width = 6
FEATURE [Part::Box] Box045  label="Würfel045"
  AttacherType = Attacher::AttachEngine3D
  Height = 17
  Length = 18
  Placement = pos=(-61.5,16,-7) rot=(0,0,1;0rad)
  Width = 6
FEATURE [Part::MultiFuse] Fusion046
  Shapes = -> [Cylinder083,Cylinder084,Box042,Fusion009]
FEATURE [Part::MultiFuse] Fusion047
  Shapes = -> [Cylinder085,Cylinder086,Box043,Box044,Box045]
FEATURE [Part::Cylinder] Cylinder087  label="Zylinder087"
  Angle = 360
  AttacherType = Attacher::AttachEngine3D
  FirstAngle = 0
  Height = 10
  Placement = pos=(16.5,10,-31.5) rot=(0,0,1;0rad)
  Radius = 3.15
  SecondAngle = 0
FEATURE [Part::Cylinder] Cylinder088  label="Zylinder088"
  Angle = 360
  AttacherType = Attacher::AttachEngine3D
  FirstAngle = 0
  Height = 10
  Placement = pos=(16.5,10,-2) rot=(0,0,1;0rad)
  Radius = 4.25
  SecondAngle = 0
FEATURE [Part::Wedge] Wedge  label="Keil"
  AttacherType = Attacher::AttachEngine3D
  Placement = pos=(12.5,10,0) rot=(0,0,1;0rad)
  X2max = 6
  X2min = 2
  Xmax = 8
  Xmin = 0
  Ymax = 18
  Ymin = 0
  Z2max = 8
  Z2min = 2
  Zmax = 8
  Zmin = 2
FEATURE [Part::Box] Box046  label="Würfel046"
  AttacherType = Attacher::AttachEngine3D
  Height = 7
  Length = 7
  Placement = pos=(13,1,1) rot=(0,0,1;0rad)
  Width = 9
FEATURE [Part::Cylinder] Cylinder089  label="Zylinder089"
  Angle = 360
  AttacherType = Attacher::AttachEngine3D
  FirstAngle = 0
  Height = 14
  Placement = pos=(16.5,10,-2) rot=(0,0,1;0rad)
  Radius = 1.5
  SecondAngle = 0
FEATURE [Part::Cylinder] Cylinder090  label="Zylinder090"
  Angle = 360
  AttacherType = Attacher::AttachEngine3D
  FirstAngle = 0
  Height = 3
  Placement = pos=(16.5,10,9.5) rot=(0,0,1;0rad)
  Radius = 3
  SecondAngle = 0
FEATURE [Part::MultiFuse] Fusion048
  Shapes = -> [Cylinder087,Cylinder088,Wedge,Box046,Cylinder089,Cylinder090]
FEATURE [Part::Cylinder] Cylinder092  label="Zylinder092"
  Angle = 360
  AttacherType = Attacher::AttachEngine3D
  FirstAngle = 0
  Height = 10
  Placement = pos=(-52.5,10,-1) rot=(0,0,1;0rad)
  Radius = 3.15
  SecondAngle = 0
FEATURE [Part::Cylinder] Cylinder093  label="Zylinder093"
  Angle = 360
  AttacherType = Attacher::AttachEngine3D
  FirstAngle = 0
  Height = 10
  Placement = pos=(-52.5,10,-31.5) rot=(0,0,1;0rad)
  Radius = 3.15
  SecondAngle = 0
FEATURE [Part::Box] Box047  label="Würfel047"
  AttacherType = Attacher::AttachEngine3D
  Height = 10
  Length = 12
  Placement = pos=(-58.5,3.5,-2.5) rot=(0,0,1;0rad)
  Width = 23
FEATURE [Part::Box] Box048  label="Würfel048"
  AttacherType = Attacher::AttachEngine3D
  Height = 10
  Length = 18
  Placement = pos=(-62,14.134,-28.366) rot=(-1,0,0;0.523599rad)
  Width = 10
FEATURE [Part::Box] Box049  label="Würfel049"
  AttacherType = Attacher::AttachEngine3D
  Height = 10
  Length = 18
  Placement = pos=(-62,-22.933,-33.4462) rot=(1,0,0;0.523599rad)
  Width = 10
FEATURE [Part::Box] Box050  label="Würfel050"
  AttacherType = Attacher::AttachEngine3D
  Height = 10
  Length = 18
  Placement = pos=(7.5,13.7625,-28.0795) rot=(-1,0,0;1.0472rad)
  Width = 10
FEATURE [Part::Box] Box051  label="Würfel051"
  AttacherType = Attacher::AttachEngine3D
  Height = 10
  Length = 18
  Placement = pos=(7.5,-26.207,-32.3052) rot=(-1,0,0;0.523599rad)
  Width = 10
FEATURE [Part::MultiFuse] Fusion051
  Shapes = -> [Box051,Box050]
FEATURE [Part::Box] Box053  label="Würfel053"
  AttacherType = Attacher::AttachEngine3D
  Height = 10
  Length = 3
  Placement = pos=(-31.5,-10,-8) rot=(0,0,1;0rad)
  Width = 33
FEATURE [Part::Box] Box054  label="Würfel054"
  AttacherType = Attacher::AttachEngine3D
  Height = 10
  Length = 24
  Placement = pos=(-0.5,3.5,-12.5) rot=(0,0,1;0rad)
  Width = 13
FEATURE [Part::Box] Box055  label="Würfel055"
  AttacherType = Attacher::AttachEngine3D
  Height = 10
  Length = 24
  Placement = pos=(-0.5,-16.5,-12.5) rot=(0,0,1;0rad)
  Width = 13
FEATURE [Part::Box] Box057  label="Würfel057"
  AttacherType = Attacher::AttachEngine3D
  Height = 1.5
  Length = 26
  Placement = pos=(-31.5,7,-8) rot=(0,0,1;0rad)
  Width = 2.5
FEATURE [Part::Box] Box058  label="Würfel058"
  AttacherType = Attacher::AttachEngine3D
  Height = 1.5
  Length = 26
  Placement = pos=(-31.5,-9.5,-8) rot=(0,0,1;0rad)
  Width = 2.5
FEATURE [Part::Box] Box059  label="Würfel059"
  AttacherType = Attacher::AttachEngine3D
  Height = 1.5
  Length = 3
  Placement = pos=(-8.5,-9.5,-8) rot=(0,0,1;0rad)
  Width = 19
FEATURE [Part::Box] Box060  label="Würfel060"
  AttacherType = Attacher::AttachEngine3D
  Height = 1.5
  Length = 33.2
  Placement = pos=(-5.75,-1,-8) rot=(0,0,1;0rad)
  Width = 2.5
FEATURE [Sketcher::SketchObject] Sketch
  FullyConstrained = false
  MapMode = 5
  Placement = pos=(0,0,0) rot=(0.57735,0.57735,0.57735;2.0944rad)
  Support = -> [YZ_Plane]
  sketch-geometry (50):
    g0: LineSegment StartX=4 StartY=4 StartZ=0 EndX=4 EndY=10 EndZ=0
    g1: LineSegment StartX=4 StartY=10 StartZ=0 EndX=21 EndY=10 EndZ=0
    g2: LineSegment StartX=5 StartY=-29 StartZ=0 EndX=18 EndY=-29 EndZ=0
    g3: LineSegment StartX=5 StartY=-29 StartZ=0 EndX=5 EndY=-33 EndZ=0
    g4: LineSegment StartX=5 StartY=-33 StartZ=0 EndX=28 EndY=-33 EndZ=0
    g5: LineSegment StartX=4 StartY=4 StartZ=0 EndX=16 EndY=4 EndZ=0
    g6: LineSegment StartX=16 StartY=4 StartZ=0 EndX=21 EndY=6 EndZ=0
    g7: Circle CenterX=21 CenterY=10 CenterZ=0 NormalX=0 NormalY=0 NormalZ=1 AngleXU=0 Radius=2
    g8: Circle CenterX=33 CenterY=12 CenterZ=0 NormalX=0 NormalY=0 NormalZ=1 AngleXU=0 Radius=2
    g9: Circle CenterX=40 CenterY=18 CenterZ=0 NormalX=0 NormalY=0 NormalZ=1 AngleXU=0 Radius=2
    g10: BSplineCurve PolesCount=3 KnotsCount=2 Degree=2 IsPeriodic=0
    g11: GeomPoint X=21 Y=10 Z=0
    g12: GeomPoint X=40 Y=18 Z=0
    g13: Circle CenterX=40 CenterY=18 CenterZ=0 NormalX=0 NormalY=0 NormalZ=1 AngleXU=0 Radius=1
    g14: Circle CenterX=42 CenterY=12 CenterZ=0 NormalX=0 NormalY=0 NormalZ=1 AngleXU=0 Radius=1
    g15: Circle CenterX=49 CenterY=7 CenterZ=0 NormalX=0 NormalY=0 NormalZ=1 AngleXU=0 Radius=1
    g16: BSplineCurve PolesCount=3 KnotsCount=2 Degree=2 IsPeriodic=0
    g17: GeomPoint X=40 Y=18 Z=0
    g18: GeomPoint X=49 Y=7 Z=0
    g19: Circle CenterX=49 CenterY=7 CenterZ=0 NormalX=0 NormalY=0 NormalZ=1 AngleXU=0 Radius=8
    g20: Circle CenterX=50 CenterY=-43 CenterZ=0 NormalX=0 NormalY=0 NormalZ=1 AngleXU=0 Radius=8
    g21: BSplineCurve PolesCount=2 KnotsCount=2 Degree=1 IsPeriodic=0
    g22: GeomPoint X=49 Y=7 Z=0
    g23: GeomPoint X=50 Y=-43 Z=0
    g24: Circle CenterX=48 CenterY=-43 CenterZ=0 NormalX=0 NormalY=0 NormalZ=1 AngleXU=0 Radius=8
    g25: Circle CenterX=48 CenterY=10 CenterZ=0 NormalX=0 NormalY=0 NormalZ=1 AngleXU=0 Radius=8
    g26: Circle CenterX=38 CenterY=10 CenterZ=0 NormalX=0 NormalY=0 NormalZ=1 AngleXU=0 Radius=8
    g27: BSplineCurve PolesCount=3 KnotsCount=2 Degree=2 IsPeriodic=0
    g28: GeomPoint X=48 Y=-43 Z=0
    g29: GeomPoint X=38 Y=10 Z=0
    g30: LineSegment StartX=48 StartY=-43 StartZ=0 EndX=50 EndY=-43 EndZ=0
    g31: Circle CenterX=28 CenterY=-33 CenterZ=0 NormalX=0 NormalY=0 NormalZ=1 AngleXU=0 Radius=4
    g32: Circle CenterX=31.5452 CenterY=5.41621 CenterZ=0 NormalX=0 NormalY=0 NormalZ=1 AngleXU=0 Radius=4
    g33: Circle CenterX=38 CenterY=10 CenterZ=0 NormalX=0 NormalY=0 NormalZ=1 AngleXU=0 Radius=4
    g34: BSplineCurve PolesCount=3 KnotsCount=2 Degree=2 IsPeriodic=0
    g35: GeomPoint X=28 Y=-33 Z=0
    g36: GeomPoint X=38 Y=10 Z=0
    g37-g43: Circle x7 (B-spline internal-alignment scaffolding for g44; pole/knot coordinates omitted)
    g44: BSplineCurve PolesCount=7 KnotsCount=5 Degree=3 IsPeriodic=0
    g45-g49: GeomPoint x5 (B-spline internal-alignment scaffolding for g44; pole/knot coordinates omitted)
  constraints (42):
    c: Weight(g7) = 1
    c: Equal(g7,g8)
    c: Equal(g7,g9)
    c: InternalAlignment(g7,g10)
    c: InternalAlignment(g8,g10)
    c: InternalAlignment(g9,g10)
    c: InternalAlignment(g11,g10)
    c: InternalAlignment(g12,g10)
    c: Weight(g13) = 1
    c: Equal(g13,g14)
    c: Equal(g13,g15)
    c: InternalAlignment(g13,g16)
    c: InternalAlignment(g14,g16)
    c: InternalAlignment(g15,g16)
    c: InternalAlignment(g17,g16)
    c: InternalAlignment(g18,g16)
    c: Weight(g19) = 1
    c: Equal(g19,g20)
    c: InternalAlignment(g19,g21)
    c: InternalAlignment(g20,g21)
    c: InternalAlignment(g22,g21)
    c: InternalAlignment(g23,g21)
    c: Weight(g24) = 1
    c: Equal(g24,g25)
    c: Equal(g24,g26)
    c: InternalAlignment(g24,g27)
    c: InternalAlignment(g25,g27)
    c: InternalAlignment(g26,g27)
    c: InternalAlignment(g28,g27)
    c: InternalAlignment(g29,g27)
    c: Weight(g31) = 1
    c: Equal(g31,g32)
    c: Equal(g31,g33)
    c: InternalAlignment(g31,g34)
    c: InternalAlignment(g32,g34)
    c: InternalAlignment(g33,g34)
    c: InternalAlignment(g35,g34)
    c: InternalAlignment(g36,g34)
    c: Weight(g37) = 1
    c: Equal(g37, g38-g43) x6
    c: InternalAlignment(g37-g43 -> g44) x7
    c: InternalAlignment(g45-g49 -> g44) x5
FEATURE [PartDesign::Pad] Pad
  AllowMultiFace = false
  Direction = (1,1,1)
  Length = 10
  Length2 = 100
  Placement = pos=(0,0,0) rot=(0.57735,0.57735,0.57735;2.0944rad)
  Profile = -> Sketch
  Type = 0
FEATURE [Part::Chamfer] Chamfer
  Base = -> Pad
  Edges = 1 edges: [Edge21 r1=7 r2=50]
  Placement = pos=(11.5,0,0) rot=(0,0,1;0rad)
FEATURE [Part::Fillet] Fillet014
  Base = -> Chamfer
  Edges = 1 edges r=1: [Edge4]
FEATURE [Part::Fillet] Fillet015
  Base = -> Fillet014
  Edges = 1 edges r=1: [Edge44]
FEATURE [Part::Fillet] Fillet016
  Base = -> Fillet015
  Edges = 2 edges r=4: [Edge16,Edge50]
FEATURE [PartDesign::Body] Body  label="leg_front_L_template"
  Group = -> [Sketch,Pad]
  Origin = -> Origin
  Placement = pos=(11.5,0,0) rot=(0,0,1;0rad)
  Tip = -> Pad
FEATURE [Part::Cylinder] Cylinder094  label="Zylinder094"
  Angle = 360
  AttacherType = Attacher::AttachEngine3D
  FirstAngle = 0
  Height = 2.5
  Placement = pos=(16.5,23,-35.5) rot=(0,0,1;0rad)
  Radius = 1.4
  SecondAngle = 0
FEATURE [Part::Cylinder] Cylinder095  label="Zylinder095"
  Angle = 360
  AttacherType = Attacher::AttachEngine3D
  FirstAngle = 0
  Height = 3.5
  Placement = pos=(16.5,23,-36) rot=(0,0,1;0rad)
  Radius = 3.25
  SecondAngle = 0
FEATURE [Part::Cylinder] Cylinder096  label="Zylinder096"
  Angle = 360
  AttacherType = Attacher::AttachEngine3D
  FirstAngle = 0
  Height = 20
  Placement = pos=(-52.5,23,-38.5) rot=(0,0,1;0rad)
  Radius = 0.6
  SecondAngle = 0
FEATURE [Part::Cylinder] Cylinder099  label="Zylinder099"
  Angle = 360
  AttacherType = Attacher::AttachEngine3D
  FirstAngle = 0
  Height = 20
  Placement = pos=(16.5,23,-38.5) rot=(0,0,1;0rad)
  Radius = 0.6
  SecondAngle = 0
FEATURE [Part::Box] Box062  label="Würfel062"
  AttacherType = Attacher::AttachEngine3D
  Height = 5
  Length = 5
  Placement = pos=(-29,5,-8) rot=(0,0,1;0rad)
  Width = 6
FEATURE [Part::Cylinder] Cylinder097  label="Zylinder097"
  Angle = 360
  AttacherType = Attacher::AttachEngine3D
  FirstAngle = 0
  Height = 3.5
  Placement = pos=(-52.5,23,-36) rot=(0,0,1;0rad)
  Radius = 3.25
  SecondAngle = 0
FEATURE [Part::Box] Box063  label="Würfel063"
  AttacherType = Attacher::AttachEngine3D
  Height = 24
  Length = 23
  Placement = pos=(0,0,-1) rot=(0,0,1;0rad)
  Width = 13
FEATURE [Part::Box] Box064  label="Würfel064"
  AttacherType = Attacher::AttachEngine3D
  Height = 2
  Length = 32
  Placement = pos=(-4.5,0,18) rot=(0,0,1;0rad)
  Width = 13
FEATURE [Part::Cylinder] Cylinder100  label="Zylinder100"
  Angle = 360
  AttacherType = Attacher::AttachEngine3D
  FirstAngle = 0
  Height = 10
  Placement = pos=(25.5,6.5,13) rot=(0,0,1;0rad)
  Radius = 1.5
  SecondAngle = 0
FEATURE [Part::Cylinder] Cylinder101  label="Zylinder101"
  Angle = 360
  AttacherType = Attacher::AttachEngine3D
  FirstAngle = 0
  Height = 6
  Placement = pos=(16.5,6.5,23) rot=(0,0,1;0rad)
  Radius = 6.5
  SecondAngle = 0
FEATURE [Part::Cylinder] Cylinder102  label="Zylinder102"
  Angle = 360
  AttacherType = Attacher::AttachEngine3D
  FirstAngle = 0
  Height = 5
  Placement = pos=(16.5,6.5,29) rot=(0,0,1;0rad)
  Radius = 3.5
  SecondAngle = 0
FEATURE [Part::Cylinder] Cylinder103  label="Zylinder103"
  Angle = 360
  AttacherType = Attacher::AttachEngine3D
  FirstAngle = 0
  Height = 5
  Placement = pos=(16.5,6.5,30) rot=(0,0,1;0rad)
  Radius = 1.5
  SecondAngle = 0
FEATURE [Part::Cylinder] Cylinder104  label="Zylinder104"
  Angle = 360
  AttacherType = Attacher::AttachEngine3D
  FirstAngle = 0
  Height = 10
  Placement = pos=(-2.5,6.5,13) rot=(0,0,1;0rad)
  Radius = 1.5
  SecondAngle = 0
FEATURE [Part::MultiFuse] Fusion060
  Shapes = -> [Box063,Cylinder102,Box064,Cylinder101]
FEATURE [Part::MultiFuse] Fusion061
  Shapes = -> [Cylinder104,Cylinder100,Cylinder103]
FEATURE [Part::Cut] Cut044  label="Servo3_mask001"
  Base = -> Fusion060
  Placement = pos=(-49.5,16.5,5) rot=(0.57735,-0.57735,0.57735;4.18879rad)
  Tool = -> Fusion061
FEATURE [Part::Box] Box065  label="Würfel065"
  AttacherType = Attacher::AttachEngine3D
  Height = 12
  Length = 12
  Placement = pos=(-45,-22,-5) rot=(0,0,1;0rad)
  Width = 9
FEATURE [Part::MultiFuse] Fusion063
  Placement = pos=(0,0,1) rot=(0,0,1;0rad)
  Shapes = -> [Box065,Fusion010,Cut005,Box053,Box055,Box054,Box062]
FEATURE [Part::Cylinder] Cylinder105  label="Zylinder105"
  Angle = 360
  AttacherType = Attacher::AttachEngine3D
  FirstAngle = 0
  Height = 15
  Placement = pos=(-2.5,10,-20) rot=(0,0,1;0rad)
  Radius = 1
  SecondAngle = 0
FEATURE [Part::Cylinder] Cylinder106  label="Zylinder106"
  Angle = 360
  AttacherType = Attacher::AttachEngine3D
  FirstAngle = 0
  Height = 15
  Placement = pos=(-2.5,-10,-20) rot=(0,0,1;0rad)
  Radius = 1
  SecondAngle = 0
FEATURE [Part::Cylinder] Cylinder107  label="Zylinder107"
  Angle = 360
  AttacherType = Attacher::AttachEngine3D
  FirstAngle = 0
  Height = 15
  Placement = pos=(25.5,-10,-20) rot=(0,0,1;0rad)
  Radius = 1
  SecondAngle = 0
FEATURE [Part::Cylinder] Cylinder108  label="Zylinder108"
  Angle = 360
  AttacherType = Attacher::AttachEngine3D
  FirstAngle = 0
  Height = 15
  Placement = pos=(25.5,10,-20) rot=(0,0,1;0rad)
  Radius = 1
  SecondAngle = 0
FEATURE [Part::MultiFuse] Fusion064
  Shapes = -> [Box058,Box059,Box060,Box057]
FEATURE [Part::MultiFuse] Fusion065
  Shapes = -> [Box012,Fusion043]
FEATURE [Part::Cut] Cut046
  Base = -> Fusion065
  Tool = -> Fusion044
FEATURE [Part::Cut] Cut047
  Base = -> Cut046
  Tool = -> Fusion063
FEATURE [Part::Box] Box066  label="Würfel066"
  AttacherType = Attacher::AttachEngine3D
  Height = 13
  Length = 10
  Placement = pos=(-50,5.5,-7) rot=(0,0,1;0rad)
  Width = 11
FEATURE [Part::Wedge] Wedge001  label="Keil001"
  AttacherType = Attacher::AttachEngine3D
  Placement = pos=(12.5,10,0) rot=(0,0,1;0rad)
  X2max = 6
  X2min = 2
  Xmax = 8
  Xmin = 0
  Ymax = 18
  Ymin = 0
  Z2max = 8
  Z2min = 2
  Zmax = 8
  Zmin = 2
FEATURE [Part::Cylinder] Cylinder109  label="Zylinder109"
  Angle = 360
  AttacherType = Attacher::AttachEngine3D
  FirstAngle = 0
  Height = 10
  Placement = pos=(16.5,10,-29) rot=(0,0,1;0rad)
  Radius = 3.25
  SecondAngle = 0
FEATURE [Part::Cylinder] Cylinder110  label="Zylinder110"
  Angle = 360
  AttacherType = Attacher::AttachEngine3D
  FirstAngle = 0
  Height = 10
  Placement = pos=(16.5,10,-2) rot=(0,0,1;0rad)
  Radius = 4.25
  SecondAngle = 0
FEATURE [Part::Cylinder] Cylinder111  label="Zylinder111"
  Angle = 360
  AttacherType = Attacher::AttachEngine3D
  FirstAngle = 0
  Height = 2.5
  Placement = pos=(16.5,23,-32.5) rot=(0,0,1;0rad)
  Radius = 1.4
  SecondAngle = 0
FEATURE [Part::Cylinder] Cylinder112  label="Zylinder112"
  Angle = 360
  AttacherType = Attacher::AttachEngine3D
  FirstAngle = 0
  Height = 14
  Placement = pos=(16.5,10,-2) rot=(0,0,1;0rad)
  Radius = 1.5
  SecondAngle = 0
FEATURE [Part::Cylinder] Cylinder113  label="Zylinder113"
  Angle = 360
  AttacherType = Attacher::AttachEngine3D
  FirstAngle = 0
  Height = 3
  Placement = pos=(16.5,10,9.5) rot=(0,0,1;0rad)
  Radius = 3
  SecondAngle = 0
FEATURE [Part::Box] Box067  label="Würfel067"
  AttacherType = Attacher::AttachEngine3D
  Height = 7
  Length = 7
  Placement = pos=(13,1,1) rot=(0,0,1;0rad)
  Width = 9
FEATURE [Part::MultiFuse] Fusion068
  Shapes = -> [Cylinder109,Cylinder110,Wedge001,Box067,Cylinder112,Cylinder113]
FEATURE [Part::Cylinder] Cylinder114  label="Zylinder114"
  Angle = 360
  AttacherType = Attacher::AttachEngine3D
  FirstAngle = 0
  Height = 20
  Placement = pos=(16.5,23,-34.5) rot=(0,0,1;0rad)
  Radius = 0.6
  SecondAngle = 0
FEATURE [Part::Box] Box068  label="Würfel068"
  AttacherType = Attacher::AttachEngine3D
  Height = 0.5
  Length = 12
  Placement = pos=(10.5,2.5,4) rot=(0,0,1;0rad)
  Width = 16
FEATURE [Part::MultiFuse] Fusion067
  Placement = pos=(0,-51,0) rot=(0,0,1;0rad)
  Shapes = -> [Fusion068,Cylinder111,Cylinder114]
FEATURE [Part::Chamfer] Chamfer006
  Base = -> Box047
  Edges = 1 edges r=3: [Edge12]
FEATURE [Part::Chamfer] Chamfer007
  Base = -> Chamfer006
  Edges = 1 edges r=1: [Edge9]
FEATURE [Sketcher::SketchObject] Sketch004
  FullyConstrained = false
  MapMode = 5
  Support = -> [XY_Plane004]
  sketch-geometry (12):
    g0: LineSegment StartX=-5 StartY=17 StartZ=0 EndX=-1 EndY=17 EndZ=0
    g1: LineSegment StartX=-1 StartY=17 StartZ=0 EndX=-1 EndY=3 EndZ=0
    g2: LineSegment StartX=-1 StartY=3 StartZ=0 EndX=24 EndY=3 EndZ=0
    g3: LineSegment StartX=24 StartY=3 StartZ=0 EndX=24 EndY=17 EndZ=0
    g4: LineSegment StartX=24 StartY=17 StartZ=0 EndX=28 EndY=17 EndZ=0
    g5: LineSegment StartX=28 StartY=17 StartZ=0 EndX=28 EndY=-17 EndZ=0
    g6: LineSegment StartX=-5 StartY=17 StartZ=0 EndX=-5 EndY=-17 EndZ=0
    g7: LineSegment StartX=-1 StartY=-3 StartZ=0 EndX=-1 EndY=-17 EndZ=0
    g8: LineSegment StartX=-1 StartY=-3 StartZ=0 EndX=24 EndY=-3 EndZ=0
    g9: LineSegment StartX=24 StartY=-3 StartZ=0 EndX=24 EndY=-17 EndZ=0
    g10: LineSegment StartX=24 StartY=-17 StartZ=0 EndX=28 EndY=-17 EndZ=0
    g11: LineSegment StartX=-5 StartY=-17 StartZ=0 EndX=-1 EndY=-17 EndZ=0
FEATURE [PartDesign::Pad] Pad005
  AllowMultiFace = false
  Direction = (1,1,1)
  Length = 10
  Length2 = 100
  Profile = -> Sketch004
  Type = 0
FEATURE [PartDesign::Body] Body001
  Group = -> [Sketch004,Pad005]
  Origin = -> Origin004
  Tip = -> Pad005
FEATURE [App::Part] Part001  label="front_servo_support001"
  Group = -> [Body001]
  Origin = -> Origin003
  Placement = pos=(0,0,-19) rot=(0,0,1;0rad)
FEATURE [Part::MultiFuse] Fusion070
  Shapes = -> [Cylinder099,Fusion048]
FEATURE [Part::MultiFuse] Fusion072
  Shapes = -> [Cylinder093,Cylinder092,Cylinder096,Chamfer007]
FEATURE [Part::MultiFuse] Fusion074
  Placement = pos=(0,0,17) rot=(0,0,1;0rad)
  Shapes = -> [Cylinder105,Cylinder107,Cylinder108,Cylinder106]
FEATURE [Part::Cut] Cut055
  Base = -> Body001
  Placement = pos=(0,0,-19) rot=(0,0,1;0rad)
  Tool = -> Fusion074
FEATURE [Part::Box] Box070  label="Würfel070"
  AttacherType = Attacher::AttachEngine3D
  Height = 4
  Length = 10
  Placement = pos=(-23,-27.5,-19) rot=(0,0,1;0rad)
  Width = 55
FEATURE [Part::MultiFuse] Fusion079
  Shapes = -> [Cylinder094,Fillet016]
FEATURE [Part::Cut] Cut058
  Base = -> Fusion079
  Tool = -> Fusion070
FEATURE [Part::Cut] Cut059
  Base = -> Cut058
  Tool = -> Box068
FEATURE [Part::Fillet] Fillet060
  Base = -> Cut059
  Edges = 2 edges r=4: [Edge5,Edge37]
FEATURE [App::DocumentObjectGroup] Gruppe002  label="leg_front_left"
  Group = -> [Fillet060]
FEATURE [Sketcher::SketchObject] Sketch008
  FullyConstrained = false
  MapMode = 5
  Placement = pos=(0,0,0) rot=(0.57735,0.57735,0.57735;2.0944rad)
  Support = -> [YZ_Plane016]
  sketch-geometry (50):
    g0: LineSegment StartX=4 StartY=4 StartZ=0 EndX=4 EndY=10 EndZ=0
    g1: LineSegment StartX=4 StartY=10 StartZ=0 EndX=21 EndY=10 EndZ=0
    g2: LineSegment StartX=5 StartY=-29 StartZ=0 EndX=18 EndY=-29 EndZ=0
    g3: LineSegment StartX=5 StartY=-29 StartZ=0 EndX=5 EndY=-33 EndZ=0
    g4: LineSegment StartX=5 StartY=-33 StartZ=0 EndX=28 EndY=-33 EndZ=0
    g5: LineSegment StartX=4 StartY=4 StartZ=0 EndX=16 EndY=4 EndZ=0
    g6: LineSegment StartX=16 StartY=4 StartZ=0 EndX=21 EndY=6 EndZ=0
    g7: Circle CenterX=21 CenterY=10 CenterZ=0 NormalX=0 NormalY=0 NormalZ=1 AngleXU=0 Radius=2
    g8: Circle CenterX=33 CenterY=12 CenterZ=0 NormalX=0 NormalY=0 NormalZ=1 AngleXU=0 Radius=2
    g9: Circle CenterX=40 CenterY=18 CenterZ=0 NormalX=0 NormalY=0 NormalZ=1 AngleXU=0 Radius=2
    g10: BSplineCurve PolesCount=3 KnotsCount=2 Degree=2 IsPeriodic=0
    g11: GeomPoint X=21 Y=10 Z=0
    g12: GeomPoint X=40 Y=18 Z=0
    g13: Circle CenterX=40 CenterY=18 CenterZ=0 NormalX=0 NormalY=0 NormalZ=1 AngleXU=0 Radius=1
    g14: Circle CenterX=42 CenterY=12 CenterZ=0 NormalX=0 NormalY=0 NormalZ=1 AngleXU=0 Radius=1
    g15: Circle CenterX=49 CenterY=7 CenterZ=0 NormalX=0 NormalY=0 NormalZ=1 AngleXU=0 Radius=1
    g16: BSplineCurve PolesCount=3 KnotsCount=2 Degree=2 IsPeriodic=0
    g17: GeomPoint X=40 Y=18 Z=0
    g18: GeomPoint X=49 Y=7 Z=0
    g19: Circle CenterX=49 CenterY=7 CenterZ=0 NormalX=0 NormalY=0 NormalZ=1 AngleXU=0 Radius=8
    g20: Circle CenterX=50 CenterY=-43 CenterZ=0 NormalX=0 NormalY=0 NormalZ=1 AngleXU=0 Radius=8
    g21: BSplineCurve PolesCount=2 KnotsCount=2 Degree=1 IsPeriodic=0
    g22: GeomPoint X=49 Y=7 Z=0
    g23: GeomPoint X=50 Y=-43 Z=0
    g24: Circle CenterX=48 CenterY=-43 CenterZ=0 NormalX=0 NormalY=0 NormalZ=1 AngleXU=0 Radius=8
    g25: Circle CenterX=48 CenterY=10 CenterZ=0 NormalX=0 NormalY=0 NormalZ=1 AngleXU=0 Radius=8
    g26: Circle CenterX=38 CenterY=10 CenterZ=0 NormalX=0 NormalY=0 NormalZ=1 AngleXU=0 Radius=8
    g27: BSplineCurve PolesCount=3 KnotsCount=2 Degree=2 IsPeriodic=0
    g28: GeomPoint X=48 Y=-43 Z=0
    g29: GeomPoint X=38 Y=10 Z=0
    g30: LineSegment StartX=48 StartY=-43 StartZ=0 EndX=50 EndY=-43 EndZ=0
    g31: Circle CenterX=28 CenterY=-33 CenterZ=0 NormalX=0 NormalY=0 NormalZ=1 AngleXU=0 Radius=4
    g32: Circle CenterX=31.5452 CenterY=5.41621 CenterZ=0 NormalX=0 NormalY=0 NormalZ=1 AngleXU=0 Radius=4
    g33: Circle CenterX=38 CenterY=10 CenterZ=0 NormalX=0 NormalY=0 NormalZ=1 AngleXU=0 Radius=4
    g34: BSplineCurve PolesCount=3 KnotsCount=2 Degree=2 IsPeriodic=0
    g35: GeomPoint X=28 Y=-33 Z=0
    g36: GeomPoint X=38 Y=10 Z=0
    g37-g43: Circle x7 (B-spline internal-alignment scaffolding for g44; pole/knot coordinates omitted)
    g44: BSplineCurve PolesCount=7 KnotsCount=5 Degree=3 IsPeriodic=0
    g45-g49: GeomPoint x5 (B-spline internal-alignment scaffolding for g44; pole/knot coordinates omitted)
  constraints (42):
    c: Weight(g7) = 1
    c: Equal(g7,g8)
    c: Equal(g7,g9)
    c: InternalAlignment(g7,g10)
    c: InternalAlignment(g8,g10)
    c: InternalAlignment(g9,g10)
    c: InternalAlignment(g11,g10)
    c: InternalAlignment(g12,g10)
    c: Weight(g13) = 1
    c: Equal(g13,g14)
    c: Equal(g13,g15)
    c: InternalAlignment(g13,g16)
    c: InternalAlignment(g14,g16)
    c: InternalAlignment(g15,g16)
    c: InternalAlignment(g17,g16)
    c: InternalAlignment(g18,g16)
    c: Weight(g19) = 1
    c: Equal(g19,g20)
    c: InternalAlignment(g19,g21)
    c: InternalAlignment(g20,g21)
    c: InternalAlignment(g22,g21)
    c: InternalAlignment(g23,g21)
    c: Weight(g24) = 1
    c: Equal(g24,g25)
    c: Equal(g24,g26)
    c: InternalAlignment(g24,g27)
    c: InternalAlignment(g25,g27)
    c: InternalAlignment(g26,g27)
    c: InternalAlignment(g28,g27)
    c: InternalAlignment(g29,g27)
    c: Weight(g31) = 1
    c: Equal(g31,g32)
    c: Equal(g31,g33)
    c: InternalAlignment(g31,g34)
    c: InternalAlignment(g32,g34)
    c: InternalAlignment(g33,g34)
    c: InternalAlignment(g35,g34)
    c: InternalAlignment(g36,g34)
    c: Weight(g37) = 1
    c: Equal(g37, g38-g43) x6
    c: InternalAlignment(g37-g43 -> g44) x7
    c: InternalAlignment(g45-g49 -> g44) x5
FEATURE [Part::Cylinder] Cylinder120  label="Zylinder120"
  Angle = 360
  AttacherType = Attacher::AttachEngine3D
  FirstAngle = 0
  Height = 2.5
  Placement = pos=(16.5,23,-35.5) rot=(0,0,1;0rad)
  Radius = 1.4
  SecondAngle = 0
FEATURE [PartDesign::Pad] Pad008
  AllowMultiFace = false
  Direction = (1,1,1)
  Length = 10
  Length2 = 100
  Placement = pos=(0,0,0) rot=(0.57735,0.57735,0.57735;2.0944rad)
  Profile = -> Sketch008
  Type = 0
FEATURE [PartDesign::Body] Pad008Body
  Group = -> [Sketch008,Pad008]
  Origin = -> Origin006
  Tip = -> Pad008
FEATURE [Part::Chamfer] Chamfer011
  Base = -> Pad008Body
  Edges = 1 edges: [Edge21 r1=7 r2=50]
  Placement = pos=(11.5,0,0) rot=(0,0,1;0rad)
FEATURE [Part::Fillet] Fillet063
  Base = -> Chamfer011
  Edges = 1 edges r=1: [Edge4]
FEATURE [Part::Fillet] Fillet064
  Base = -> Fillet063
  Edges = 1 edges r=1: [Edge44]
FEATURE [Part::Fillet] Fillet062
  Base = -> Fillet064
  Edges = 2 edges r=4: [Edge16,Edge50]
FEATURE [Part::MultiFuse] Fusion080
  Placement = pos=(-69,0,0) rot=(0,0,1;0rad)
  Shapes = -> [Cylinder120,Fillet062]
FEATURE [Part::Cut] Cut060
  Base = -> Fusion080
  Tool = -> Fusion072
FEATURE [Part::Fillet] Fillet065
  Base = -> Cut060
  Edges = 2 edges r=4: [Edge7,Edge39]
FEATURE [App::DocumentObjectGroup] Gruppe001  label="leg_rear_left"
  Group = -> [Fillet065]
FEATURE [Sketcher::SketchObject] Sketch009
  FullyConstrained = false
  MapMode = 5
  Support = -> [XY_Plane007]
  sketch-geometry (18):
    g0: LineSegment StartX=-57 StartY=19 StartZ=0 EndX=-57 EndY=27 EndZ=0
    g1: LineSegment StartX=-57 StartY=19 StartZ=0 EndX=-48.5 EndY=19 EndZ=0
    g2: LineSegment StartX=-57 StartY=27 StartZ=0 EndX=-48.5 EndY=27 EndZ=0
    g3: LineSegment StartX=12.5 StartY=19 StartZ=0 EndX=21 EndY=19 EndZ=0
    g4: LineSegment StartX=21 StartY=19 StartZ=0 EndX=21 EndY=27 EndZ=0
    g5: LineSegment StartX=21 StartY=27 StartZ=0 EndX=12.5 EndY=27 EndZ=0
    g6: Circle CenterX=-48.5 CenterY=19 CenterZ=0 NormalX=0 NormalY=0 NormalZ=1 AngleXU=0 Radius=5
    g7: Circle CenterX=-18 CenterY=24 CenterZ=0 NormalX=0 NormalY=0 NormalZ=1 AngleXU=0 Radius=5
    g8: Circle CenterX=12.5 CenterY=19 CenterZ=0 NormalX=0 NormalY=0 NormalZ=1 AngleXU=0 Radius=5
    g9: BSplineCurve PolesCount=3 KnotsCount=2 Degree=2 IsPeriodic=0
    g10: GeomPoint X=-48.5 Y=19 Z=0
    g11: GeomPoint X=12.5 Y=19 Z=0
    g12: Circle CenterX=-48.5 CenterY=27 CenterZ=0 NormalX=0 NormalY=0 NormalZ=1 AngleXU=0 Radius=5
    g13: Circle CenterX=-18 CenterY=22 CenterZ=0 NormalX=0 NormalY=0 NormalZ=1 AngleXU=0 Radius=5
    g14: Circle CenterX=12.5 CenterY=27 CenterZ=0 NormalX=0 NormalY=0 NormalZ=1 AngleXU=0 Radius=5
    g15: BSplineCurve PolesCount=3 KnotsCount=2 Degree=2 IsPeriodic=0
    g16: GeomPoint X=-48.5 Y=27 Z=0
    g17: GeomPoint X=12.5 Y=27 Z=0
  constraints (16):
    c: Weight(g6) = 1
    c: Equal(g6,g7)
    c: Equal(g6,g8)
    c: InternalAlignment(g6,g9)
    c: InternalAlignment(g7,g9)
    c: InternalAlignment(g8,g9)
    c: InternalAlignment(g10,g9)
    c: InternalAlignment(g11,g9)
    c: Weight(g12) = 1
    c: Equal(g12,g13)
    c: Equal(g12,g14)
    c: InternalAlignment(g12,g15)
    c: InternalAlignment(g13,g15)
    c: InternalAlignment(g14,g15)
    c: InternalAlignment(g16,g15)
    c: InternalAlignment(g17,g15)
FEATURE [PartDesign::Pad] Pad009
  AllowMultiFace = false
  Direction = (1,1,1)
  Length = 4
  Length2 = 100
  Profile = -> Sketch009
  Type = 0
FEATURE [PartDesign::Body] Body002
  Group = -> [Sketch009,Pad009]
  Origin = -> Origin007
  Placement = pos=(0,0,-38) rot=(0,0,1;0rad)
  Tip = -> Pad009
FEATURE [App::Part] Part
  Group = -> [Pad008Body,Body002]
  Origin = -> Origin005
  Placement = pos=(0,0,1) rot=(0,0,1;0rad)
FEATURE [Part::Cylinder] Cylinder121  label="Zylinder121"
  Angle = 360
  AttacherType = Attacher::AttachEngine3D
  FirstAngle = 0
  Height = 9.5
  Placement = pos=(16.5,23,-39) rot=(0,0,1;0rad)
  Radius = 0.6
  SecondAngle = 0
FEATURE [Part::Cylinder] Cylinder122  label="Zylinder122"
  Angle = 360
  AttacherType = Attacher::AttachEngine3D
  FirstAngle = 0
  Height = 9.5
  Placement = pos=(-52.5,23,-39) rot=(0,0,1;0rad)
  Radius = 0.6
  SecondAngle = 0
FEATURE [Part::MultiFuse] Fusion081
  Shapes = -> [Cylinder095,Cylinder097,Cylinder121,Cylinder122]
FEATURE [Sketcher::SketchObject] Sketch010
  FullyConstrained = false
  MapMode = 5
  Placement = pos=(0,0,0) rot=(0.57735,0.57735,0.57735;2.0944rad)
  Support = -> [YZ_Plane025]
  sketch-geometry (50):
    g0: LineSegment StartX=4 StartY=4 StartZ=0 EndX=4 EndY=10 EndZ=0
    g1: LineSegment StartX=4 StartY=10 StartZ=0 EndX=21 EndY=10 EndZ=0
    g2: LineSegment StartX=5 StartY=-29 StartZ=0 EndX=18 EndY=-29 EndZ=0
    g3: LineSegment StartX=5 StartY=-29 StartZ=0 EndX=5 EndY=-33 EndZ=0
    g4: LineSegment StartX=5 StartY=-33 StartZ=0 EndX=28 EndY=-33 EndZ=0
    g5: LineSegment StartX=4 StartY=4 StartZ=0 EndX=16 EndY=4 EndZ=0
    g6: LineSegment StartX=16 StartY=4 StartZ=0 EndX=21 EndY=6 EndZ=0
    g7: Circle CenterX=21 CenterY=10 CenterZ=0 NormalX=0 NormalY=0 NormalZ=1 AngleXU=0 Radius=2
    g8: Circle CenterX=33 CenterY=12 CenterZ=0 NormalX=0 NormalY=0 NormalZ=1 AngleXU=0 Radius=2
    g9: Circle CenterX=40 CenterY=18 CenterZ=0 NormalX=0 NormalY=0 NormalZ=1 AngleXU=0 Radius=2
    g10: BSplineCurve PolesCount=3 KnotsCount=2 Degree=2 IsPeriodic=0
    g11: GeomPoint X=21 Y=10 Z=0
    g12: GeomPoint X=40 Y=18 Z=0
    g13: Circle CenterX=40 CenterY=18 CenterZ=0 NormalX=0 NormalY=0 NormalZ=1 AngleXU=0 Radius=1
    g14: Circle CenterX=42 CenterY=12 CenterZ=0 NormalX=0 NormalY=0 NormalZ=1 AngleXU=0 Radius=1
    g15: Circle CenterX=49 CenterY=7 CenterZ=0 NormalX=0 NormalY=0 NormalZ=1 AngleXU=0 Radius=1
    g16: BSplineCurve PolesCount=3 KnotsCount=2 Degree=2 IsPeriodic=0
    g17: GeomPoint X=40 Y=18 Z=0
    g18: GeomPoint X=49 Y=7 Z=0
    g19: Circle CenterX=49 CenterY=7 CenterZ=0 NormalX=0 NormalY=0 NormalZ=1 AngleXU=0 Radius=8
    g20: Circle CenterX=50 CenterY=-43 CenterZ=0 NormalX=0 NormalY=0 NormalZ=1 AngleXU=0 Radius=8
    g21: BSplineCurve PolesCount=2 KnotsCount=2 Degree=1 IsPeriodic=0
    g22: GeomPoint X=49 Y=7 Z=0
    g23: GeomPoint X=50 Y=-43 Z=0
    g24: Circle CenterX=48 CenterY=-43 CenterZ=0 NormalX=0 NormalY=0 NormalZ=1 AngleXU=0 Radius=8
    g25: Circle CenterX=48 CenterY=10 CenterZ=0 NormalX=0 NormalY=0 NormalZ=1 AngleXU=0 Radius=8
    g26: Circle CenterX=38 CenterY=10 CenterZ=0 NormalX=0 NormalY=0 NormalZ=1 AngleXU=0 Radius=8
    g27: BSplineCurve PolesCount=3 KnotsCount=2 Degree=2 IsPeriodic=0
    g28: GeomPoint X=48 Y=-43 Z=0
    g29: GeomPoint X=38 Y=10 Z=0
    g30: LineSegment StartX=48 StartY=-43 StartZ=0 EndX=50 EndY=-43 EndZ=0
    g31: Circle CenterX=28 CenterY=-33 CenterZ=0 NormalX=0 NormalY=0 NormalZ=1 AngleXU=0 Radius=4
    g32: Circle CenterX=31.5452 CenterY=5.41621 CenterZ=0 NormalX=0 NormalY=0 NormalZ=1 AngleXU=0 Radius=4
    g33: Circle CenterX=38 CenterY=10 CenterZ=0 NormalX=0 NormalY=0 NormalZ=1 AngleXU=0 Radius=4
    g34: BSplineCurve PolesCount=3 KnotsCount=2 Degree=2 IsPeriodic=0
    g35: GeomPoint X=28 Y=-33 Z=0
    g36: GeomPoint X=38 Y=10 Z=0
    g37-g43: Circle x7 (B-spline internal-alignment scaffolding for g44; pole/knot coordinates omitted)
    g44: BSplineCurve PolesCount=7 KnotsCount=5 Degree=3 IsPeriodic=0
    g45-g49: GeomPoint x5 (B-spline internal-alignment scaffolding for g44; pole/knot coordinates omitted)
  constraints (42):
    c: Weight(g7) = 1
    c: Equal(g7,g8)
    c: Equal(g7,g9)
    c: InternalAlignment(g7,g10)
    c: InternalAlignment(g8,g10)
    c: InternalAlignment(g9,g10)
    c: InternalAlignment(g11,g10)
    c: InternalAlignment(g12,g10)
    c: Weight(g13) = 1
    c: Equal(g13,g14)
    c: Equal(g13,g15)
    c: InternalAlignment(g13,g16)
    c: InternalAlignment(g14,g16)
    c: InternalAlignment(g15,g16)
    c: InternalAlignment(g17,g16)
    c: InternalAlignment(g18,g16)
    c: Weight(g19) = 1
    c: Equal(g19,g20)
    c: InternalAlignment(g19,g21)
    c: InternalAlignment(g20,g21)
    c: InternalAlignment(g22,g21)
    c: InternalAlignment(g23,g21)
    c: Weight(g24) = 1
    c: Equal(g24,g25)
    c: Equal(g24,g26)
    c: InternalAlignment(g24,g27)
    c: InternalAlignment(g25,g27)
    c: InternalAlignment(g26,g27)
    c: InternalAlignment(g28,g27)
    c: InternalAlignment(g29,g27)
    c: Weight(g31) = 1
    c: Equal(g31,g32)
    c: Equal(g31,g33)
    c: InternalAlignment(g31,g34)
    c: InternalAlignment(g32,g34)
    c: InternalAlignment(g33,g34)
    c: InternalAlignment(g35,g34)
    c: InternalAlignment(g36,g34)
    c: Weight(g37) = 1
    c: Equal(g37, g38-g43) x6
    c: InternalAlignment(g37-g43 -> g44) x7
    c: InternalAlignment(g45-g49 -> g44) x5
FEATURE [Part::Wedge] Wedge004  label="Keil004"
  AttacherType = Attacher::AttachEngine3D
  Placement = pos=(12.5,10,0) rot=(0,0,1;0rad)
  X2max = 6
  X2min = 2
  Xmax = 8
  Xmin = 0
  Ymax = 18
  Ymin = 0
  Z2max = 8
  Z2min = 2
  Zmax = 8
  Zmin = 2
FEATURE [Part::Cylinder] Cylinder123  label="Zylinder123"
  Angle = 360
  AttacherType = Attacher::AttachEngine3D
  FirstAngle = 0
  Height = 10
  Placement = pos=(16.5,10,-2) rot=(0,0,1;0rad)
  Radius = 4.25
  SecondAngle = 0
FEATURE [Part::Box] Box074  label="Würfel074"
  AttacherType = Attacher::AttachEngine3D
  Height = 7
  Length = 7
  Placement = pos=(13,1,1) rot=(0,0,1;0rad)
  Width = 9
FEATURE [Part::Cylinder] Cylinder124  label="Zylinder124"
  Angle = 360
  AttacherType = Attacher::AttachEngine3D
  FirstAngle = 0
  Height = 3
  Placement = pos=(16.5,10,9.5) rot=(0,0,1;0rad)
  Radius = 3
  SecondAngle = 0
FEATURE [Part::Cylinder] Cylinder125  label="Zylinder125"
  Angle = 360
  AttacherType = Attacher::AttachEngine3D
  FirstAngle = 0
  Height = 14
  Placement = pos=(16.5,10,-2) rot=(0,0,1;0rad)
  Radius = 1.5
  SecondAngle = 0
FEATURE [Part::Cylinder] Cylinder126  label="Zylinder126"
  Angle = 360
  AttacherType = Attacher::AttachEngine3D
  FirstAngle = 0
  Height = 10
  Placement = pos=(16.5,10,-31.5) rot=(0,0,1;0rad)
  Radius = 3.15
  SecondAngle = 0
FEATURE [Part::MultiFuse] Fusion082
  Shapes = -> [Cylinder126,Cylinder123,Wedge004,Box074,Cylinder125,Cylinder124]
FEATURE [Part::Cylinder] Cylinder127  label="Zylinder127"
  Angle = 360
  AttacherType = Attacher::AttachEngine3D
  FirstAngle = 0
  Height = 20
  Placement = pos=(16.5,23,-38.5) rot=(0,0,1;0rad)
  Radius = 0.6
  SecondAngle = 0
FEATURE [Part::Cylinder] Cylinder128  label="Zylinder128"
  Angle = 360
  AttacherType = Attacher::AttachEngine3D
  FirstAngle = 0
  Height = 2.5
  Placement = pos=(16.5,23,-35.5) rot=(0,0,1;0rad)
  Radius = 1.4
  SecondAngle = 0
FEATURE [PartDesign::Pad] Pad010
  AllowMultiFace = false
  Direction = (1,1,1)
  Length = 10
  Length2 = 100
  Placement = pos=(0,0,0) rot=(0.57735,0.57735,0.57735;2.0944rad)
  Profile = -> Sketch010
  Type = 0
FEATURE [Part::Box] Box075  label="Würfel075"
  AttacherType = Attacher::AttachEngine3D
  Height = 0.5
  Length = 12
  Placement = pos=(10.5,2.5,4) rot=(0,0,1;0rad)
  Width = 16
FEATURE [Part::MultiFuse] Fusion084
  Shapes = -> [Cylinder127,Fusion082]
FEATURE [Sketcher::SketchObject] Sketch011
  FullyConstrained = false
  MapMode = 5
  Placement = pos=(0,0,0) rot=(0.57735,0.57735,0.57735;2.0944rad)
  Support = -> [YZ_Plane019]
  sketch-geometry (50):
    g0: LineSegment StartX=4 StartY=4 StartZ=0 EndX=4 EndY=10 EndZ=0
    g1: LineSegment StartX=4 StartY=10 StartZ=0 EndX=21 EndY=10 EndZ=0
    g2: LineSegment StartX=5 StartY=-29 StartZ=0 EndX=18 EndY=-29 EndZ=0
    g3: LineSegment StartX=5 StartY=-29 StartZ=0 EndX=5 EndY=-33 EndZ=0
    g4: LineSegment StartX=5 StartY=-33 StartZ=0 EndX=28 EndY=-33 EndZ=0
    g5: LineSegment StartX=4 StartY=4 StartZ=0 EndX=16 EndY=4 EndZ=0
    g6: LineSegment StartX=16 StartY=4 StartZ=0 EndX=21 EndY=6 EndZ=0
    g7: Circle CenterX=21 CenterY=10 CenterZ=0 NormalX=0 NormalY=0 NormalZ=1 AngleXU=0 Radius=2
    g8: Circle CenterX=33 CenterY=12 CenterZ=0 NormalX=0 NormalY=0 NormalZ=1 AngleXU=0 Radius=2
    g9: Circle CenterX=40 CenterY=18 CenterZ=0 NormalX=0 NormalY=0 NormalZ=1 AngleXU=0 Radius=2
    g10: BSplineCurve PolesCount=3 KnotsCount=2 Degree=2 IsPeriodic=0
    g11: GeomPoint X=21 Y=10 Z=0
    g12: GeomPoint X=40 Y=18 Z=0
    g13: Circle CenterX=40 CenterY=18 CenterZ=0 NormalX=0 NormalY=0 NormalZ=1 AngleXU=0 Radius=1
    g14: Circle CenterX=42 CenterY=12 CenterZ=0 NormalX=0 NormalY=0 NormalZ=1 AngleXU=0 Radius=1
    g15: Circle CenterX=49 CenterY=7 CenterZ=0 NormalX=0 NormalY=0 NormalZ=1 AngleXU=0 Radius=1
    g16: BSplineCurve PolesCount=3 KnotsCount=2 Degree=2 IsPeriodic=0
    g17: GeomPoint X=40 Y=18 Z=0
    g18: GeomPoint X=49 Y=7 Z=0
    g19: Circle CenterX=49 CenterY=7 CenterZ=0 NormalX=0 NormalY=0 NormalZ=1 AngleXU=0 Radius=8
    g20: Circle CenterX=50 CenterY=-43 CenterZ=0 NormalX=0 NormalY=0 NormalZ=1 AngleXU=0 Radius=8
    g21: BSplineCurve PolesCount=2 KnotsCount=2 Degree=1 IsPeriodic=0
    g22: GeomPoint X=49 Y=7 Z=0
    g23: GeomPoint X=50 Y=-43 Z=0
    g24: Circle CenterX=48 CenterY=-43 CenterZ=0 NormalX=0 NormalY=0 NormalZ=1 AngleXU=0 Radius=8
    g25: Circle CenterX=48 CenterY=10 CenterZ=0 NormalX=0 NormalY=0 NormalZ=1 AngleXU=0 Radius=8
    g26: Circle CenterX=38 CenterY=10 CenterZ=0 NormalX=0 NormalY=0 NormalZ=1 AngleXU=0 Radius=8
    g27: BSplineCurve PolesCount=3 KnotsCount=2 Degree=2 IsPeriodic=0
    g28: GeomPoint X=48 Y=-43 Z=0
    g29: GeomPoint X=38 Y=10 Z=0
    g30: LineSegment StartX=48 StartY=-43 StartZ=0 EndX=50 EndY=-43 EndZ=0
    g31: Circle CenterX=28 CenterY=-33 CenterZ=0 NormalX=0 NormalY=0 NormalZ=1 AngleXU=0 Radius=4
    g32: Circle CenterX=31.5452 CenterY=5.41621 CenterZ=0 NormalX=0 NormalY=0 NormalZ=1 AngleXU=0 Radius=4
    g33: Circle CenterX=38 CenterY=10 CenterZ=0 NormalX=0 NormalY=0 NormalZ=1 AngleXU=0 Radius=4
    g34: BSplineCurve PolesCount=3 KnotsCount=2 Degree=2 IsPeriodic=0
    g35: GeomPoint X=28 Y=-33 Z=0
    g36: GeomPoint X=38 Y=10 Z=0
    g37-g43: Circle x7 (B-spline internal-alignment scaffolding for g44; pole/knot coordinates omitted)
    g44: BSplineCurve PolesCount=7 KnotsCount=5 Degree=3 IsPeriodic=0
    g45-g49: GeomPoint x5 (B-spline internal-alignment scaffolding for g44; pole/knot coordinates omitted)
  constraints (42):
    c: Weight(g7) = 1
    c: Equal(g7,g8)
    c: Equal(g7,g9)
    c: InternalAlignment(g7,g10)
    c: InternalAlignment(g8,g10)
    c: InternalAlignment(g9,g10)
    c: InternalAlignment(g11,g10)
    c: InternalAlignment(g12,g10)
    c: Weight(g13) = 1
    c: Equal(g13,g14)
    c: Equal(g13,g15)
    c: InternalAlignment(g13,g16)
    c: InternalAlignment(g14,g16)
    c: InternalAlignment(g15,g16)
    c: InternalAlignment(g17,g16)
    c: InternalAlignment(g18,g16)
    c: Weight(g19) = 1
    c: Equal(g19,g20)
    c: InternalAlignment(g19,g21)
    c: InternalAlignment(g20,g21)
    c: InternalAlignment(g22,g21)
    c: InternalAlignment(g23,g21)
    c: Weight(g24) = 1
    c: Equal(g24,g25)
    c: Equal(g24,g26)
    c: InternalAlignment(g24,g27)
    c: InternalAlignment(g25,g27)
    c: InternalAlignment(g26,g27)
    c: InternalAlignment(g28,g27)
    c: InternalAlignment(g29,g27)
    c: Weight(g31) = 1
    c: Equal(g31,g32)
    c: Equal(g31,g33)
    c: InternalAlignment(g31,g34)
    c: InternalAlignment(g32,g34)
    c: InternalAlignment(g33,g34)
    c: InternalAlignment(g35,g34)
    c: InternalAlignment(g36,g34)
    c: Weight(g37) = 1
    c: Equal(g37, g38-g43) x6
    c: InternalAlignment(g37-g43 -> g44) x7
    c: InternalAlignment(g45-g49 -> g44) x5
FEATURE [Part::Box] Box076  label="Würfel076"
  AttacherType = Attacher::AttachEngine3D
  Height = 10
  Length = 12
  Placement = pos=(-58.5,3.5,-2.5) rot=(0,0,1;0rad)
  Width = 23
FEATURE [Part::Cylinder] Cylinder129  label="Zylinder129"
  Angle = 360
  AttacherType = Attacher::AttachEngine3D
  FirstAngle = 0
  Height = 10
  Placement = pos=(-52.5,10,-1) rot=(0,0,1;0rad)
  Radius = 3.15
  SecondAngle = 0
FEATURE [Part::Cylinder] Cylinder130  label="Zylinder130"
  Angle = 360
  AttacherType = Attacher::AttachEngine3D
  FirstAngle = 0
  Height = 10
  Placement = pos=(-52.5,10,-31.5) rot=(0,0,1;0rad)
  Radius = 3.15
  SecondAngle = 0
FEATURE [Part::Chamfer] Chamfer015
  Base = -> Box076
  Edges = 1 edges r=3: [Edge12]
FEATURE [Part::Chamfer] Chamfer014
  Base = -> Chamfer015
  Edges = 1 edges r=1: [Edge9]
FEATURE [Part::Cylinder] Cylinder131  label="Zylinder131"
  Angle = 360
  AttacherType = Attacher::AttachEngine3D
  FirstAngle = 0
  Height = 20
  Placement = pos=(-52.5,23,-38.5) rot=(0,0,1;0rad)
  Radius = 0.6
  SecondAngle = 0
FEATURE [PartDesign::Pad] Pad011
  AllowMultiFace = false
  Direction = (1,1,1)
  Length = 10
  Length2 = 100
  Placement = pos=(0,0,0) rot=(0.57735,0.57735,0.57735;2.0944rad)
  Profile = -> Sketch011
  Type = 0
FEATURE [PartDesign::Body] Pad008Body001
  Group = -> [Sketch011,Pad011]
  Origin = -> Origin008
  Tip = -> Pad011
FEATURE [Part::Chamfer] Chamfer016
  Base = -> Pad008Body001
  Edges = 1 edges: [Edge21 r1=7 r2=50]
  Placement = pos=(11.5,0,0) rot=(0,0,1;0rad)
FEATURE [Part::Fillet] Fillet074
  Base = -> Chamfer016
  Edges = 1 edges r=1: [Edge4]
FEATURE [Part::Fillet] Fillet072
  Base = -> Fillet074
  Edges = 1 edges r=1: [Edge44]
FEATURE [Part::Fillet] Fillet071
  Base = -> Fillet072
  Edges = 2 edges r=4: [Edge16,Edge50]
FEATURE [Part::Cylinder] Cylinder132  label="Zylinder132"
  Angle = 360
  AttacherType = Attacher::AttachEngine3D
  FirstAngle = 0
  Height = 2.5
  Placement = pos=(16.5,23,-35.5) rot=(0,0,1;0rad)
  Radius = 1.4
  SecondAngle = 0
FEATURE [Part::MultiFuse] Fusion085
  Placement = pos=(-69,0,0) rot=(0,0,1;0rad)
  Shapes = -> [Cylinder132,Fillet071]
FEATURE [Part::MultiFuse] Fusion086
  Shapes = -> [Cylinder130,Cylinder129,Cylinder131,Chamfer014]
FEATURE [Part::Cut] Cut064
  Base = -> Fusion085
  Tool = -> Fusion086
FEATURE [Part::Fillet] Fillet073
  Base = -> Cut064
  Edges = 2 edges r=4: [Edge7,Edge39]
FEATURE [Part::Mirroring] Part__Mirroring002  label="Fillet073 (Mirror #3)"
  Base = (0,0,0)
  Normal = (0,0,1)
  Placement = pos=(0,0,0) rot=(1,0,0;3.14159rad)
  Source = -> Fillet073
FEATURE [App::DocumentObjectGroup] Gruppe013  label="leg_rear_right"
  Group = -> [Part__Mirroring002]
FEATURE [Part::Cut] Cut061
  Base = -> Body002
  Tool = -> Fusion081
FEATURE [Part::Fillet] Fillet075
  Base = -> Cut061
  Edges = 4 edges r=3: [Edge5,Edge8,Edge25,Edge26]
FEATURE [Sketcher::SketchObject] Sketch012
  FullyConstrained = false
  MapMode = 5
  Support = -> [XY_Plane009]
  sketch-geometry (18):
    g0: LineSegment StartX=-57 StartY=19 StartZ=0 EndX=-57 EndY=27 EndZ=0
    g1: LineSegment StartX=-57 StartY=19 StartZ=0 EndX=-48.5 EndY=19 EndZ=0
    g2: LineSegment StartX=-57 StartY=27 StartZ=0 EndX=-48.5 EndY=27 EndZ=0
    g3: LineSegment StartX=12.5 StartY=19 StartZ=0 EndX=21 EndY=19 EndZ=0
    g4: LineSegment StartX=21 StartY=19 StartZ=0 EndX=21 EndY=27 EndZ=0
    g5: LineSegment StartX=21 StartY=27 StartZ=0 EndX=12.5 EndY=27 EndZ=0
    g6: Circle CenterX=-48.5 CenterY=19 CenterZ=0 NormalX=0 NormalY=0 NormalZ=1 AngleXU=0 Radius=5
    g7: Circle CenterX=-18 CenterY=24 CenterZ=0 NormalX=0 NormalY=0 NormalZ=1 AngleXU=0 Radius=5
    g8: Circle CenterX=12.5 CenterY=19 CenterZ=0 NormalX=0 NormalY=0 NormalZ=1 AngleXU=0 Radius=5
    g9: BSplineCurve PolesCount=3 KnotsCount=2 Degree=2 IsPeriodic=0
    g10: GeomPoint X=-48.5 Y=19 Z=0
    g11: GeomPoint X=12.5 Y=19 Z=0
    g12: Circle CenterX=-48.5 CenterY=27 CenterZ=0 NormalX=0 NormalY=0 NormalZ=1 AngleXU=0 Radius=5
    g13: Circle CenterX=-18 CenterY=22 CenterZ=0 NormalX=0 NormalY=0 NormalZ=1 AngleXU=0 Radius=5
    g14: Circle CenterX=12.5 CenterY=27 CenterZ=0 NormalX=0 NormalY=0 NormalZ=1 AngleXU=0 Radius=5
    g15: BSplineCurve PolesCount=3 KnotsCount=2 Degree=2 IsPeriodic=0
    g16: GeomPoint X=-48.5 Y=27 Z=0
    g17: GeomPoint X=12.5 Y=27 Z=0
  constraints (16):
    c: Weight(g6) = 1
    c: Equal(g6,g7)
    c: Equal(g6,g8)
    c: InternalAlignment(g6,g9)
    c: InternalAlignment(g7,g9)
    c: InternalAlignment(g8,g9)
    c: InternalAlignment(g10,g9)
    c: InternalAlignment(g11,g9)
    c: Weight(g12) = 1
    c: Equal(g12,g13)
    c: Equal(g12,g14)
    c: InternalAlignment(g12,g15)
    c: InternalAlignment(g13,g15)
    c: InternalAlignment(g14,g15)
    c: InternalAlignment(g16,g15)
    c: InternalAlignment(g17,g15)
FEATURE [Part::Cylinder] Cylinder133  label="Zylinder133"
  Angle = 360
  AttacherType = Attacher::AttachEngine3D
  FirstAngle = 0
  Height = 3.5
  Placement = pos=(16.5,23,-36) rot=(0,0,1;0rad)
  Radius = 3.25
  SecondAngle = 0
FEATURE [Part::Cylinder] Cylinder134  label="Zylinder134"
  Angle = 360
  AttacherType = Attacher::AttachEngine3D
  FirstAngle = 0
  Height = 3.5
  Placement = pos=(-52.5,23,-36) rot=(0,0,1;0rad)
  Radius = 3.25
  SecondAngle = 0
FEATURE [Part::Cylinder] Cylinder135  label="Zylinder135"
  Angle = 360
  AttacherType = Attacher::AttachEngine3D
  FirstAngle = 0
  Height = 9.5
  Placement = pos=(-52.5,23,-39) rot=(0,0,1;0rad)
  Radius = 0.6
  SecondAngle = 0
FEATURE [PartDesign::Pad] Pad012
  AllowMultiFace = false
  Direction = (1,1,1)
  Length = 4
  Length2 = 100
  Profile = -> Sketch012
  Type = 0
FEATURE [PartDesign::Body] Body003
  Group = -> [Sketch012,Pad012]
  Origin = -> Origin009
  Placement = pos=(0,0,-38) rot=(0,0,1;0rad)
  Tip = -> Pad012
FEATURE [Part::Cylinder] Cylinder136  label="Zylinder136"
  Angle = 360
  AttacherType = Attacher::AttachEngine3D
  FirstAngle = 0
  Height = 9.5
  Placement = pos=(16.5,23,-39) rot=(0,0,1;0rad)
  Radius = 0.6
  SecondAngle = 0
FEATURE [Part::MultiFuse] Fusion087
  Shapes = -> [Cylinder133,Cylinder134,Cylinder136,Cylinder135]
FEATURE [Part::Cut] Cut065
  Base = -> Body003
  Tool = -> Fusion087
FEATURE [Part::Fillet] Fillet076
  Base = -> Cut065
  Edges = 4 edges r=3: [Edge5,Edge8,Edge25,Edge26]
  Placement = pos=(0,-46,0) rot=(0,0,1;0rad)
FEATURE [Sketcher::SketchObject] Sketch013
  FullyConstrained = false
  MapMode = 5
  Support = -> [XY_Plane010]
  sketch-geometry (18):
    g0: LineSegment StartX=-57 StartY=19 StartZ=0 EndX=-57 EndY=27 EndZ=0
    g1: LineSegment StartX=-57 StartY=19 StartZ=0 EndX=-48.5 EndY=19 EndZ=0
    g2: LineSegment StartX=-57 StartY=27 StartZ=0 EndX=-48.5 EndY=27 EndZ=0
    g3: LineSegment StartX=12.5 StartY=19 StartZ=0 EndX=21 EndY=19 EndZ=0
    g4: LineSegment StartX=21 StartY=19 StartZ=0 EndX=21 EndY=27 EndZ=0
    g5: LineSegment StartX=21 StartY=27 StartZ=0 EndX=12.5 EndY=27 EndZ=0
    g6: Circle CenterX=-48.5 CenterY=19 CenterZ=0 NormalX=0 NormalY=0 NormalZ=1 AngleXU=0 Radius=5
    g7: Circle CenterX=-18 CenterY=24 CenterZ=0 NormalX=0 NormalY=0 NormalZ=1 AngleXU=0 Radius=5
    g8: Circle CenterX=12.5 CenterY=19 CenterZ=0 NormalX=0 NormalY=0 NormalZ=1 AngleXU=0 Radius=5
    g9: BSplineCurve PolesCount=3 KnotsCount=2 Degree=2 IsPeriodic=0
    g10: GeomPoint X=-48.5 Y=19 Z=0
    g11: GeomPoint X=12.5 Y=19 Z=0
    g12: Circle CenterX=-48.5 CenterY=27 CenterZ=0 NormalX=0 NormalY=0 NormalZ=1 AngleXU=0 Radius=5
    g13: Circle CenterX=-18 CenterY=22 CenterZ=0 NormalX=0 NormalY=0 NormalZ=1 AngleXU=0 Radius=5
    g14: Circle CenterX=12.5 CenterY=27 CenterZ=0 NormalX=0 NormalY=0 NormalZ=1 AngleXU=0 Radius=5
    g15: BSplineCurve PolesCount=3 KnotsCount=2 Degree=2 IsPeriodic=0
    g16: GeomPoint X=-48.5 Y=27 Z=0
    g17: GeomPoint X=12.5 Y=27 Z=0
  constraints (16):
    c: Weight(g6) = 1
    c: Equal(g6,g7)
    c: Equal(g6,g8)
    c: InternalAlignment(g6,g9)
    c: InternalAlignment(g7,g9)
    c: InternalAlignment(g8,g9)
    c: InternalAlignment(g10,g9)
    c: InternalAlignment(g11,g9)
    c: Weight(g12) = 1
    c: Equal(g12,g13)
    c: Equal(g12,g14)
    c: InternalAlignment(g12,g15)
    c: InternalAlignment(g13,g15)
    c: InternalAlignment(g14,g15)
    c: InternalAlignment(g16,g15)
    c: InternalAlignment(g17,g15)
FEATURE [Part::Cylinder] Cylinder137  label="Zylinder137"
  Angle = 360
  AttacherType = Attacher::AttachEngine3D
  FirstAngle = 0
  Height = 3.5
  Placement = pos=(-52.5,23,-36) rot=(0,0,1;0rad)
  Radius = 3.25
  SecondAngle = 0
FEATURE [Part::Cylinder] Cylinder138  label="Zylinder138"
  Angle = 360
  AttacherType = Attacher::AttachEngine3D
  FirstAngle = 0
  Height = 9.5
  Placement = pos=(-52.5,23,-39) rot=(0,0,1;0rad)
  Radius = 0.6
  SecondAngle = 0
FEATURE [PartDesign::Pad] Pad013
  AllowMultiFace = false
  Direction = (1,1,1)
  Length = 4
  Length2 = 100
  Profile = -> Sketch013
  Type = 0
FEATURE [PartDesign::Body] Body004
  Group = -> [Sketch013,Pad013]
  Origin = -> Origin010
  Placement = pos=(0,0,-38) rot=(0,0,1;0rad)
  Tip = -> Pad013
FEATURE [Part::Cylinder] Cylinder139  label="Zylinder139"
  Angle = 360
  AttacherType = Attacher::AttachEngine3D
  FirstAngle = 0
  Height = 3.5
  Placement = pos=(16.5,23,-36) rot=(0,0,1;0rad)
  Radius = 3.25
  SecondAngle = 0
FEATURE [Part::Cylinder] Cylinder140  label="Zylinder140"
  Angle = 360
  AttacherType = Attacher::AttachEngine3D
  FirstAngle = 0
  Height = 9.5
  Placement = pos=(16.5,23,-39) rot=(0,0,1;0rad)
  Radius = 0.6
  SecondAngle = 0
FEATURE [Part::MultiFuse] Fusion088
  Shapes = -> [Cylinder139,Cylinder137,Cylinder140,Cylinder138]
FEATURE [Part::Cut] Cut066
  Base = -> Body004
  Tool = -> Fusion088
FEATURE [Part::Fillet] Fillet077
  Base = -> Cut066
  Edges = 4 edges r=3: [Edge5,Edge8,Edge25,Edge26]
  Placement = pos=(0,-90,0) rot=(0,0,1;0rad)
FEATURE [Part::Box] Box078  label="Würfel077"
  AttacherType = Attacher::AttachEngine3D
  Height = 10
  Length = 40
  Placement = pos=(-14,-72,-42) rot=(0,0,1;0rad)
  Width = 10
FEATURE [Part::Cut] Cut067
  Base = -> Fillet077
  Placement = pos=(-5,44,0) rot=(0,0,1;0rad)
  Tool = -> Box078
FEATURE [Sketcher::SketchObject] Sketch014
  FullyConstrained = false
  MapMode = 5
  Support = -> [XY_Plane011]
  sketch-geometry (18):
    g0: LineSegment StartX=-57 StartY=19 StartZ=0 EndX=-57 EndY=27 EndZ=0
    g1: LineSegment StartX=-57 StartY=19 StartZ=0 EndX=-48.5 EndY=19 EndZ=0
    g2: LineSegment StartX=-57 StartY=27 StartZ=0 EndX=-48.5 EndY=27 EndZ=0
    g3: LineSegment StartX=12.5 StartY=19 StartZ=0 EndX=21 EndY=19 EndZ=0
    g4: LineSegment StartX=21 StartY=19 StartZ=0 EndX=21 EndY=27 EndZ=0
    g5: LineSegment StartX=21 StartY=27 StartZ=0 EndX=12.5 EndY=27 EndZ=0
    g6: Circle CenterX=-48.5 CenterY=19 CenterZ=0 NormalX=0 NormalY=0 NormalZ=1 AngleXU=0 Radius=5
    g7: Circle CenterX=-18 CenterY=24 CenterZ=0 NormalX=0 NormalY=0 NormalZ=1 AngleXU=0 Radius=5
    g8: Circle CenterX=12.5 CenterY=19 CenterZ=0 NormalX=0 NormalY=0 NormalZ=1 AngleXU=0 Radius=5
    g9: BSplineCurve PolesCount=3 KnotsCount=2 Degree=2 IsPeriodic=0
    g10: GeomPoint X=-48.5 Y=19 Z=0
    g11: GeomPoint X=12.5 Y=19 Z=0
    g12: Circle CenterX=-48.5 CenterY=27 CenterZ=0 NormalX=0 NormalY=0 NormalZ=1 AngleXU=0 Radius=5
    g13: Circle CenterX=-18 CenterY=22 CenterZ=0 NormalX=0 NormalY=0 NormalZ=1 AngleXU=0 Radius=5
    g14: Circle CenterX=12.5 CenterY=27 CenterZ=0 NormalX=0 NormalY=0 NormalZ=1 AngleXU=0 Radius=5
    g15: BSplineCurve PolesCount=3 KnotsCount=2 Degree=2 IsPeriodic=0
    g16: GeomPoint X=-48.5 Y=27 Z=0
    g17: GeomPoint X=12.5 Y=27 Z=0
  constraints (16):
    c: Weight(g6) = 1
    c: Equal(g6,g7)
    c: Equal(g6,g8)
    c: InternalAlignment(g6,g9)
    c: InternalAlignment(g7,g9)
    c: InternalAlignment(g8,g9)
    c: InternalAlignment(g10,g9)
    c: InternalAlignment(g11,g9)
    c: Weight(g12) = 1
    c: Equal(g12,g13)
    c: Equal(g12,g14)
    c: InternalAlignment(g12,g15)
    c: InternalAlignment(g13,g15)
    c: InternalAlignment(g14,g15)
    c: InternalAlignment(g16,g15)
    c: InternalAlignment(g17,g15)
FEATURE [PartDesign::Pad] Pad014
  AllowMultiFace = false
  Direction = (1,1,1)
  Length = 4
  Length2 = 100
  Profile = -> Sketch014
  Type = 0
FEATURE [PartDesign::Body] Body005
  Group = -> [Sketch014,Pad014]
  Origin = -> Origin011
  Placement = pos=(0,0,-38) rot=(0,0,1;0rad)
  Tip = -> Pad014
FEATURE [Part::Cylinder] Cylinder141  label="Zylinder141"
  Angle = 360
  AttacherType = Attacher::AttachEngine3D
  FirstAngle = 0
  Height = 3.5
  Placement = pos=(16.5,23,-36) rot=(0,0,1;0rad)
  Radius = 3.25
  SecondAngle = 0
FEATURE [Part::Cylinder] Cylinder142  label="Zylinder142"
  Angle = 360
  AttacherType = Attacher::AttachEngine3D
  FirstAngle = 0
  Height = 9.5
  Placement = pos=(-52.5,23,-39) rot=(0,0,1;0rad)
  Radius = 0.6
  SecondAngle = 0
FEATURE [Part::Box] Box079  label="Würfel078"
  AttacherType = Attacher::AttachEngine3D
  Height = 10
  Length = 40
  Placement = pos=(-14,-72,-42) rot=(0,0,1;0rad)
  Width = 10
FEATURE [Part::Cylinder] Cylinder143  label="Zylinder143"
  Angle = 360
  AttacherType = Attacher::AttachEngine3D
  FirstAngle = 0
  Height = 3.5
  Placement = pos=(-52.5,23,-36) rot=(0,0,1;0rad)
  Radius = 3.25
  SecondAngle = 0
FEATURE [Part::Cylinder] Cylinder144  label="Zylinder144"
  Angle = 360
  AttacherType = Attacher::AttachEngine3D
  FirstAngle = 0
  Height = 9.5
  Placement = pos=(16.5,23,-39) rot=(0,0,1;0rad)
  Radius = 0.6
  SecondAngle = 0
FEATURE [Part::MultiFuse] Fusion089
  Shapes = -> [Cylinder141,Cylinder143,Cylinder144,Cylinder142]
FEATURE [Part::Cut] Cut069
  Base = -> Body005
  Tool = -> Fusion089
FEATURE [Part::Fillet] Fillet078
  Base = -> Cut069
  Edges = 4 edges r=3: [Edge5,Edge8,Edge25,Edge26]
  Placement = pos=(0,-90,0) rot=(0,0,1;0rad)
FEATURE [Part::Cut] Cut068
  Base = -> Fillet078
  Placement = pos=(-5,35,0) rot=(0,0,1;0rad)
  Tool = -> Box079
FEATURE [Part::Mirroring] Part__Mirroring003  label="Cut068 (Mirror #4)"
  Base = (-40.5,-7.62939e-06,-36)
  Normal = (0,1,-1.19209e-07)
  Placement = pos=(-36,9,0) rot=(0,0,1;3.14159rad)
  Source = -> Cut068
FEATURE [Part::MultiFuse] Fusion090
  Placement = pos=(0,-11,0) rot=(0,0,1;0rad)
  Shapes = -> [Cut067,Part__Mirroring003]
FEATURE [Part::Box] Box080  label="Würfel079"
  AttacherType = Attacher::AttachEngine3D
  Height = 4
  Length = 10
  Placement = pos=(-23,-35.5,-38) rot=(0,0,1;0rad)
  Width = 3
FEATURE [Part::Box] Box081  label="Würfel080"
  AttacherType = Attacher::AttachEngine3D
  Height = 4
  Length = 90
  Placement = pos=(-63,-38.5,-41) rot=(0,0,1;0rad)
  Width = 9
FEATURE [Part::MultiFuse] Fusion091
  Shapes = -> [Fusion090,Box080]
FEATURE [Part::Cut] Cut070
  Base = -> Fusion091
  Tool = -> Box081
FEATURE [Part::Box] Box083  label="Würfel081"
  AttacherType = Attacher::AttachEngine3D
  Height = 10
  Length = 10
  Placement = pos=(-65,-7,-13.5) rot=(0,0,1;0rad)
  Width = 14
FEATURE [Part::Fillet] Fillet079
  Base = -> Box083
  Edges = 4 edges r=2: [Edge1,Edge3,Edge5,Edge7]
FEATURE [Part::Cylinder] Cylinder145  label="Zylinder145"
  Angle = 360
  AttacherType = Attacher::AttachEngine3D
  FirstAngle = 0
  Height = 20
  Placement = pos=(-8.5,17,-7) rot=(0,0,1;0rad)
  Radius = 3
  SecondAngle = 0
FEATURE [Part::Cylinder] Cylinder146  label="Zylinder146"
  Angle = 360
  AttacherType = Attacher::AttachEngine3D
  FirstAngle = 0
  Height = 25
  Placement = pos=(-63.5,10,-10) rot=(0,0,1;0rad)
  Radius = 1.5
  SecondAngle = 0
FEATURE [Part::Box] Box084  label="rp2"
  AttacherType = Attacher::AttachEngine3D
  Height = 1
  Length = 50
  Placement = pos=(-42,-11.5,12.5) rot=(0,0,1;0rad)
  Width = 23
FEATURE [Part::Cylinder] Cylinder147  label="Zylinder147"
  Angle = 360
  AttacherType = Attacher::AttachEngine3D
  FirstAngle = 0
  Height = 25
  Placement = pos=(-8.5,17,-10) rot=(0,0,1;0rad)
  Radius = 1
  SecondAngle = 0
FEATURE [Part::Cylinder] Cylinder148  label="Zylinder148"
  Angle = 360
  AttacherType = Attacher::AttachEngine3D
  FirstAngle = 0
  Height = 20
  Placement = pos=(-63.5,-10,-7) rot=(0,0,1;0rad)
  Radius = 3
  SecondAngle = 0
FEATURE [Part::Cylinder] Cylinder149  label="Zylinder149"
  Angle = 360
  AttacherType = Attacher::AttachEngine3D
  FirstAngle = 0
  Height = 20
  Placement = pos=(-8.5,-17,-7) rot=(0,0,1;0rad)
  Radius = 3
  SecondAngle = 0
FEATURE [Part::Cylinder] Cylinder150  label="Zylinder150"
  Angle = 360
  AttacherType = Attacher::AttachEngine3D
  FirstAngle = 0
  Height = 25
  Placement = pos=(-8.5,-17,-10) rot=(0,0,1;0rad)
  Radius = 1
  SecondAngle = 0
FEATURE [Part::Cylinder] Cylinder151  label="Zylinder151"
  Angle = 360
  AttacherType = Attacher::AttachEngine3D
  FirstAngle = 0
  Height = 25
  Placement = pos=(-63.5,-10,-10) rot=(0,0,1;0rad)
  Radius = 1.5
  SecondAngle = 0
FEATURE [Part::Cylinder] Cylinder152  label="Zylinder152"
  Angle = 360
  AttacherType = Attacher::AttachEngine3D
  FirstAngle = 0
  Height = 20
  Placement = pos=(-63.5,10,-7) rot=(0,0,1;0rad)
  Radius = 3
  SecondAngle = 0
FEATURE [Part::Cylinder] Cylinder154  label="Zylinder154"
  Angle = 360
  AttacherType = Attacher::AttachEngine3D
  FirstAngle = 0
  Height = 25
  Placement = pos=(28.75,0,-10) rot=(0,0,1;0rad)
  Radius = 1
  SecondAngle = 0
FEATURE [Part::Cylinder] Cylinder155  label="Zylinder155"
  Angle = 360
  AttacherType = Attacher::AttachEngine3D
  FirstAngle = 0
  Height = 20
  Placement = pos=(28.75,0,-7) rot=(0,0,1;0rad)
  Radius = 3
  SecondAngle = 0
FEATURE [Part::Cylinder] Cylinder156  label="Zylinder156"
  Angle = 360
  AttacherType = Attacher::AttachEngine3D
  FirstAngle = 0
  Height = 20
  Placement = pos=(28.75,0,-21) rot=(0,0,1;0rad)
  Radius = 3
  SecondAngle = 0
FEATURE [Part::Box] Box086  label="Würfel083"
  AttacherType = Attacher::AttachEngine3D
  Height = 10
  Length = 9.5
  Placement = pos=(-42.5,-19.25,-11) rot=(0,0,1;0rad)
  Width = 5
FEATURE [Part::Box] Box087  label="Würfel084"
  AttacherType = Attacher::AttachEngine3D
  Height = 10
  Length = 7
  Placement = pos=(-12,-5.5,-11) rot=(0,0,1;0rad)
  Width = 11
FEATURE [Part::MultiFuse] Fusion092
  Shapes = -> [Box086,Box087,Cylinder154,Cylinder150,Cylinder151,Cylinder146,Cylinder147,Fillet079]
FEATURE [Part::Cut] Cut072
  Base = -> Cut047
  Tool = -> Fusion092
FEATURE [Part::Fillet] Fillet080
  Base = -> Cut072
  Edges = 4 edges r=8: [Edge125,Edge126,Edge177,Edge180]
FEATURE [Part::MultiFuse] Fusion093
  Shapes = -> [Fusion047,Cut044]
FEATURE [Part::Chamfer] Chamfer017
  Base = -> Fillet080
  Edges = 1 edges r=2: [Edge368]
FEATURE [Part::MultiFuse] Fusion094
  Shapes = -> [Fusion021,Box035]
FEATURE [Part::MultiFuse] Fusion095
  Shapes = -> [Fusion019,Cut009]
FEATURE [Part::MultiFuse] Fusion096
  Shapes = -> [Fusion032,Fusion094,Fusion023]
FEATURE [Part::Cut] Cut074
  Base = -> Fusion095
  Tool = -> Fusion096
FEATURE [Part::Cut] Cut076
  Base = -> Cut055
  Tool = -> Cylinder156
FEATURE [App::DocumentObjectGroup] Gruppe010  label="front_servo_support"
  Group = -> [Part001,YZ_Plane012,Cut076]
FEATURE [Part::MultiFuse] Fusion097
  Placement = pos=(-69,0,0) rot=(0,0,1;0rad)
  Shapes = -> [Cylinder066,Cylinder064]
FEATURE [Part::MultiFuse] Fusion098
  Shapes = -> [Fusion030,Box036]
FEATURE [Part::MultiFuse] Fusion099
  Shapes = -> [Fusion037,Fusion097]
FEATURE [Part::Cut] Cut077
  Base = -> Fusion098
  Tool = -> Fusion099
FEATURE [Part::Box] Box088  label="battery002"
  AttacherType = Attacher::AttachEngine3D
  Height = 13.5
  Length = 50
  Placement = pos=(-63.25,-12,-22) rot=(0,0,1;0rad)
  Width = 25
FEATURE [Part::Fillet] Fillet
  Base = -> Box088
  Edges = 2 edges r=5: [Edge9,Edge11]
  Placement = pos=(0,-0.5,-1.5) rot=(0,0,1;0rad)
FEATURE [App::DocumentObjectGroup] Gruppe016  label="battery1"
  Group = -> [Fillet]
FEATURE [Part::MultiFuse] Fusion100
  Shapes = -> [Box049,Box048]
FEATURE [Part::Chamfer] Chamfer018
  Base = -> Cut077
  Edges = 2 edges: [Edge29 r1=2 r2=3,Edge32 r1=3 r2=2]
FEATURE [Part::Box] Box089  label="Würfel085"
  AttacherType = Attacher::AttachEngine3D
  Height = 10
  Length = 32.5
  Placement = pos=(-44.5,-8,-19) rot=(0,0,1;0rad)
  Width = 16
FEATURE [Part::MultiFuse] Fusion101
  Shapes = -> [Chamfer018,Box089]
FEATURE [Part::Box] Box090  label="battery003"
  AttacherType = Attacher::AttachEngine3D
  Height = 13.5
  Length = 50
  Placement = pos=(-63.25,-12,-22) rot=(0,0,1;0rad)
  Width = 25
FEATURE [Part::Fillet] Fillet081
  Base = -> Box090
  Edges = 2 edges r=5: [Edge9,Edge11]
  Placement = pos=(0,-0.5,-1.5) rot=(0,0,1;0rad)
FEATURE [Part::Cylinder] Cylinder157  label="Zylinder157"
  Angle = 360
  AttacherType = Attacher::AttachEngine3D
  FirstAngle = 0
  Height = 41
  Placement = pos=(-58,-20.5,-16.5) rot=(-1,0,0;1.5708rad)
  Radius = 2
  SecondAngle = 0
FEATURE [Part::Box] Box091  label="Würfel086"
  AttacherType = Attacher::AttachEngine3D
  Height = 10
  Length = 2
  Placement = pos=(-57.5,17.5,-21) rot=(0,0,1;0rad)
  Width = 2
FEATURE [Part::Box] Box092  label="Würfel087"
  AttacherType = Attacher::AttachEngine3D
  Height = 10
  Length = 2
  Placement = pos=(-57.5,-19.5,-21) rot=(0,0,1;0rad)
  Width = 2
FEATURE [Part::MultiFuse] Fusion102
  Shapes = -> [Box091,Box092]
FEATURE [Part::Cut] Cut078
  Base = -> Cylinder157
  Tool = -> Fusion102
FEATURE [Part::MultiFuse] Fusion103
  Shapes = -> [Cut078,Fusion101]
FEATURE [Part::Box] Box093  label="Würfel088"
  AttacherType = Attacher::AttachEngine3D
  Height = 4
  Length = 9
  Placement = pos=(-13,-8,-13) rot=(0,0,1;0rad)
  Width = 2
FEATURE [Part::Box] Box094  label="Würfel089"
  AttacherType = Attacher::AttachEngine3D
  Height = 4
  Length = 9
  Placement = pos=(-13,6,-13) rot=(0,0,1;0rad)
  Width = 2
FEATURE [Part::Cylinder] Cylinder158  label="Zylinder158"
  Angle = 360
  AttacherType = Attacher::AttachEngine3D
  FirstAngle = 0
  Height = 20
  Placement = pos=(28.75,0,-21) rot=(0,0,1;0rad)
  Radius = 3
  SecondAngle = 0
FEATURE [Sketcher::SketchObject] Sketch015
  FullyConstrained = false
  MapMode = 5
  Support = -> [XY_Plane012]
  sketch-geometry (12):
    g0: LineSegment StartX=-5 StartY=17 StartZ=0 EndX=-1 EndY=17 EndZ=0
    g1: LineSegment StartX=-1 StartY=17 StartZ=0 EndX=-1 EndY=3 EndZ=0
    g2: LineSegment StartX=-1 StartY=3 StartZ=0 EndX=24 EndY=3 EndZ=0
    g3: LineSegment StartX=24 StartY=3 StartZ=0 EndX=24 EndY=17 EndZ=0
    g4: LineSegment StartX=24 StartY=17 StartZ=0 EndX=28 EndY=17 EndZ=0
    g5: LineSegment StartX=28 StartY=17 StartZ=0 EndX=28 EndY=-17 EndZ=0
    g6: LineSegment StartX=-5 StartY=17 StartZ=0 EndX=-5 EndY=-17 EndZ=0
    g7: LineSegment StartX=-1 StartY=-3 StartZ=0 EndX=-1 EndY=-17 EndZ=0
    g8: LineSegment StartX=-1 StartY=-3 StartZ=0 EndX=24 EndY=-3 EndZ=0
    g9: LineSegment StartX=24 StartY=-3 StartZ=0 EndX=24 EndY=-17 EndZ=0
    g10: LineSegment StartX=24 StartY=-17 StartZ=0 EndX=28 EndY=-17 EndZ=0
    g11: LineSegment StartX=-5 StartY=-17 StartZ=0 EndX=-1 EndY=-17 EndZ=0
FEATURE [Part::Cylinder] Cylinder159  label="Zylinder159"
  Angle = 360
  AttacherType = Attacher::AttachEngine3D
  FirstAngle = 0
  Height = 15
  Placement = pos=(25.5,-10,-20) rot=(0,0,1;0rad)
  Radius = 1
  SecondAngle = 0
FEATURE [Part::Cylinder] Cylinder160  label="Zylinder160"
  Angle = 360
  AttacherType = Attacher::AttachEngine3D
  FirstAngle = 0
  Height = 15
  Placement = pos=(-2.5,10,-20) rot=(0,0,1;0rad)
  Radius = 1
  SecondAngle = 0
FEATURE [Part::Cylinder] Cylinder161  label="Zylinder161"
  Angle = 360
  AttacherType = Attacher::AttachEngine3D
  FirstAngle = 0
  Height = 15
  Placement = pos=(-2.5,-10,-20) rot=(0,0,1;0rad)
  Radius = 1
  SecondAngle = 0
FEATURE [Part::Cylinder] Cylinder162  label="Zylinder162"
  Angle = 360
  AttacherType = Attacher::AttachEngine3D
  FirstAngle = 0
  Height = 15
  Placement = pos=(25.5,10,-20) rot=(0,0,1;0rad)
  Radius = 1
  SecondAngle = 0
FEATURE [Part::MultiFuse] Fusion104
  Placement = pos=(0,0,17) rot=(0,0,1;0rad)
  Shapes = -> [Cylinder160,Cylinder159,Cylinder162,Cylinder161]
FEATURE [PartDesign::Pad] Pad015
  AllowMultiFace = false
  Direction = (1,1,1)
  Length = 10
  Length2 = 100
  Profile = -> Sketch015
  Type = 0
FEATURE [PartDesign::Body] Body006
  Group = -> [Sketch015,Pad015]
  Origin = -> Origin012
  Tip = -> Pad015
FEATURE [Part::Cut] Cut081
  Base = -> Body006
  Placement = pos=(0,0,-19) rot=(0,0,1;0rad)
  Tool = -> Fusion104
FEATURE [Part::Cut] Cut080
  Base = -> Cut081
  Tool = -> Cylinder158
FEATURE [Part::Chamfer] Chamfer019
  Base = -> Cut074
  Edges = 2 edges r=1: [Edge20,Edge46]
FEATURE [Part::Cut] Cut082
  Base = -> Fusion046
  Placement = pos=(0,0,1) rot=(0,0,1;0rad)
  Tool = -> Fusion093
FEATURE [App::DocumentObjectGroup] Gruppe008  label="bank_rear"
  Group = -> [Cut082]
FEATURE [Part::MultiFuse] Fusion106
  Shapes = -> [Cylinder155,Cylinder148,Cylinder149,Cylinder152,Cylinder145]
FEATURE [Part::Box] Box097  label="Base001"
  AttacherType = Attacher::AttachEngine3D
  Height = 4
  Length = 100
  Placement = pos=(-68.25,-21,14) rot=(0,0,1;0rad)
  Width = 42
FEATURE [Part::Fillet] Fillet082
  Base = -> Box097
  Edges = 4 edges r=8: [Edge1,Edge3,Edge5,Edge7]
FEATURE [Part::Box] Box109  label="Würfel103"
  AttacherType = Attacher::AttachEngine3D
  Height = 16.5
  Length = 10
  Placement = pos=(-34,-14,-25.5) rot=(0,0,1;0rad)
  Width = 28
FEATURE [Part::Chamfer] Chamfer020
  Base = -> Box109
  Edges = 2 edges r=4: [Edge9,Edge11]
FEATURE [Part::MultiFuse] Fusion125
  Shapes = -> [Chamfer020,Cut080,Box093,Box094,Fusion103]
FEATURE [Part::Cut] Cut083
  Base = -> Fusion125
  Tool = -> Fillet081
FEATURE [Part::Box] Box110  label="Würfel104"
  AttacherType = Attacher::AttachEngine3D
  Height = 3
  Length = 56
  Placement = pos=(-43.5,20,-7) rot=(0,0,1;0rad)
  Width = 1
FEATURE [Part::Box] Box116  label="Würfel110"
  AttacherType = Attacher::AttachEngine3D
  Height = 6
  Length = 56
  Placement = pos=(-38,-18.5,13) rot=(0,0,1;0rad)
  Width = 37
FEATURE [Part::Cylinder] Cylinder197  label="Zylinder197"
  Angle = 360
  AttacherType = Attacher::AttachEngine3D
  FirstAngle = 0
  Height = 2.5
  Placement = pos=(-52.5,10,-30.5) rot=(0,0,1;0rad)
  Radius = 1.5
  SecondAngle = 0
FEATURE [Part::Cylinder] Cylinder198  label="Zylinder198"
  Angle = 360
  AttacherType = Attacher::AttachEngine3D
  FirstAngle = 0
  Height = 2.5
  Placement = pos=(-52.5,-10,-30.5) rot=(0,0,1;0rad)
  Radius = 1.5
  SecondAngle = 0
FEATURE [Part::Cylinder] Cylinder199  label="Zylinder199"
  Angle = 360
  AttacherType = Attacher::AttachEngine3D
  FirstAngle = 0
  Height = 2.5
  Placement = pos=(-52.5,10,-28.5) rot=(0,0,1;0rad)
  Radius = 2.5
  SecondAngle = 0
FEATURE [Part::Cylinder] Cylinder200  label="Zylinder200"
  Angle = 360
  AttacherType = Attacher::AttachEngine3D
  FirstAngle = 0
  Height = 2.5
  Placement = pos=(-52.5,-10,-28.5) rot=(0,0,1;0rad)
  Radius = 2.5
  SecondAngle = 0
FEATURE [Part::MultiFuse] Fusion130
  Shapes = -> [Cylinder197,Cylinder198,Cylinder199,Cylinder200]
FEATURE [Part::MultiFuse] Fusion131
  Shapes = -> [Cut083,Fusion130]
FEATURE [Part::Cylinder] Cylinder201  label="Zylinder201"
  Angle = 360
  AttacherType = Attacher::AttachEngine3D
  FirstAngle = 0
  Height = 2.5
  Placement = pos=(16.5,-10,-30.5) rot=(0,0,1;0rad)
  Radius = 1.5
  SecondAngle = 0
FEATURE [Part::Cylinder] Cylinder202  label="Zylinder202"
  Angle = 360
  AttacherType = Attacher::AttachEngine3D
  FirstAngle = 0
  Height = 2.5
  Placement = pos=(16.5,10,-30.5) rot=(0,0,1;0rad)
  Radius = 1.5
  SecondAngle = 0
FEATURE [Part::Cylinder] Cylinder203  label="Zylinder203"
  Angle = 360
  AttacherType = Attacher::AttachEngine3D
  FirstAngle = 0
  Height = 2.5
  Placement = pos=(16.5,10,-28.5) rot=(0,0,1;0rad)
  Radius = 2.5
  SecondAngle = 0
FEATURE [Part::Cylinder] Cylinder204  label="Zylinder204"
  Angle = 360
  AttacherType = Attacher::AttachEngine3D
  FirstAngle = 0
  Height = 2.5
  Placement = pos=(16.5,-10,-28.5) rot=(0,0,1;0rad)
  Radius = 2.5
  SecondAngle = 0
FEATURE [Part::MultiFuse] Fusion132
  Shapes = -> [Cylinder202,Cylinder201,Cylinder203,Cylinder204]
FEATURE [Part::MultiFuse] Fusion133
  Shapes = -> [Fusion132,Chamfer019]
FEATURE [App::DocumentObjectGroup] Gruppe003  label="bottom_front"
  Group = -> [Fusion133]
FEATURE [Part::Box] Box122  label="board004"
  AttacherType = Attacher::AttachEngine3D
  Height = 1
  Length = 69.8
  Placement = pos=(-42.5,-19.4,18.5) rot=(0,0,1;0rad)
  Width = 38.8
FEATURE [PartDesign::Body] Pad010Body
  Group = -> [Sketch010,Pad010]
  Origin = -> Origin014
  Tip = -> Pad010
FEATURE [Part::Chamfer] Chamfer013
  Base = -> Pad010Body
  Edges = 1 edges: [Edge21 r1=7 r2=50]
  Placement = pos=(11.5,0,0) rot=(0,0,1;0rad)
FEATURE [Part::Fillet] Fillet067
  Base = -> Chamfer013
  Edges = 1 edges r=1: [Edge4]
FEATURE [Part::Fillet] Fillet068
  Base = -> Fillet067
  Edges = 1 edges r=1: [Edge44]
FEATURE [Part::Fillet] Fillet069
  Base = -> Fillet068
  Edges = 2 edges r=4: [Edge16,Edge50]
FEATURE [Part::MultiFuse] Fusion083
  Shapes = -> [Cylinder128,Fillet069]
FEATURE [Part::Cut] Cut062
  Base = -> Fusion083
  Tool = -> Fusion084
FEATURE [Part::Cut] Cut063
  Base = -> Cut062
  Tool = -> Box075
FEATURE [Part::Fillet] Fillet070
  Base = -> Cut063
  Edges = 2 edges r=4: [Edge5,Edge37]
FEATURE [Part::Mirroring] Part__Mirroring001  label="Fillet070 (Mirror #2)"
  Base = (16.5,-27,0)
  Normal = (0,0,1)
  Placement = pos=(0,0,0) rot=(1,0,0;3.14159rad)
  Source = -> Fillet070
FEATURE [App::DocumentObjectGroup] Gruppe012  label="leg_front_right"
  Group = -> [Part__Mirroring001]
FEATURE [App::Part] Part002
  Group = -> [Pad010Body]
  Origin = -> Origin013
FEATURE [Image::ImagePlane] ImagePlane
  Placement = pos=(-7.5,0,19.5) rot=(0,0,1;3.14159rad)
  XSize = 69.8
  YSize = 38.8
FEATURE [Sketcher::SketchObject] Sketch016
  FullyConstrained = false
  MapMode = 5
  Support = -> [XY_Plane015]
  sketch-geometry (18):
    g0: LineSegment StartX=-57 StartY=19 StartZ=0 EndX=-57 EndY=27 EndZ=0
    g1: LineSegment StartX=-57 StartY=19 StartZ=0 EndX=-48.5 EndY=19 EndZ=0
    g2: LineSegment StartX=-57 StartY=27 StartZ=0 EndX=-48.5 EndY=27 EndZ=0
    g3: LineSegment StartX=12.5 StartY=19 StartZ=0 EndX=21 EndY=19 EndZ=0
    g4: LineSegment StartX=21 StartY=19 StartZ=0 EndX=21 EndY=27 EndZ=0
    g5: LineSegment StartX=21 StartY=27 StartZ=0 EndX=12.5 EndY=27 EndZ=0
    g6: Circle CenterX=-48.5 CenterY=19 CenterZ=0 NormalX=0 NormalY=0 NormalZ=1 AngleXU=0 Radius=5
    g7: Circle CenterX=-18 CenterY=24 CenterZ=0 NormalX=0 NormalY=0 NormalZ=1 AngleXU=0 Radius=5
    g8: Circle CenterX=12.5 CenterY=19 CenterZ=0 NormalX=0 NormalY=0 NormalZ=1 AngleXU=0 Radius=5
    g9: BSplineCurve PolesCount=3 KnotsCount=2 Degree=2 IsPeriodic=0
    g10: GeomPoint X=-48.5 Y=19 Z=0
    g11: GeomPoint X=12.5 Y=19 Z=0
    g12: Circle CenterX=-48.5 CenterY=27 CenterZ=0 NormalX=0 NormalY=0 NormalZ=1 AngleXU=0 Radius=5
    g13: Circle CenterX=-18 CenterY=22 CenterZ=0 NormalX=0 NormalY=0 NormalZ=1 AngleXU=0 Radius=5
    g14: Circle CenterX=12.5 CenterY=27 CenterZ=0 NormalX=0 NormalY=0 NormalZ=1 AngleXU=0 Radius=5
    g15: BSplineCurve PolesCount=3 KnotsCount=2 Degree=2 IsPeriodic=0
    g16: GeomPoint X=-48.5 Y=27 Z=0
    g17: GeomPoint X=12.5 Y=27 Z=0
  constraints (16):
    c: Weight(g6) = 1
    c: Equal(g6,g7)
    c: Equal(g6,g8)
    c: InternalAlignment(g6,g9)
    c: InternalAlignment(g7,g9)
    c: InternalAlignment(g8,g9)
    c: InternalAlignment(g10,g9)
    c: InternalAlignment(g11,g9)
    c: Weight(g12) = 1
    c: Equal(g12,g13)
    c: Equal(g12,g14)
    c: InternalAlignment(g12,g15)
    c: InternalAlignment(g13,g15)
    c: InternalAlignment(g14,g15)
    c: InternalAlignment(g16,g15)
    c: InternalAlignment(g17,g15)
FEATURE [Sketcher::SketchObject] Sketch017
  FullyConstrained = false
  MapMode = 5
  Support = -> [XY_Plane016]
  sketch-geometry (18):
    g0: LineSegment StartX=-57 StartY=19 StartZ=0 EndX=-57 EndY=27 EndZ=0
    g1: LineSegment StartX=-57 StartY=19 StartZ=0 EndX=-48.5 EndY=19 EndZ=0
    g2: LineSegment StartX=-57 StartY=27 StartZ=0 EndX=-48.5 EndY=27 EndZ=0
    g3: LineSegment StartX=12.5 StartY=19 StartZ=0 EndX=21 EndY=19 EndZ=0
    g4: LineSegment StartX=21 StartY=19 StartZ=0 EndX=21 EndY=27 EndZ=0
    g5: LineSegment StartX=21 StartY=27 StartZ=0 EndX=12.5 EndY=27 EndZ=0
    g6: Circle CenterX=-48.5 CenterY=19 CenterZ=0 NormalX=0 NormalY=0 NormalZ=1 AngleXU=0 Radius=5
    g7: Circle CenterX=-18 CenterY=24 CenterZ=0 NormalX=0 NormalY=0 NormalZ=1 AngleXU=0 Radius=5
    g8: Circle CenterX=12.5 CenterY=19 CenterZ=0 NormalX=0 NormalY=0 NormalZ=1 AngleXU=0 Radius=5
    g9: BSplineCurve PolesCount=3 KnotsCount=2 Degree=2 IsPeriodic=0
    g10: GeomPoint X=-48.5 Y=19 Z=0
    g11: GeomPoint X=12.5 Y=19 Z=0
    g12: Circle CenterX=-48.5 CenterY=27 CenterZ=0 NormalX=0 NormalY=0 NormalZ=1 AngleXU=0 Radius=5
    g13: Circle CenterX=-18 CenterY=22 CenterZ=0 NormalX=0 NormalY=0 NormalZ=1 AngleXU=0 Radius=5
    g14: Circle CenterX=12.5 CenterY=27 CenterZ=0 NormalX=0 NormalY=0 NormalZ=1 AngleXU=0 Radius=5
    g15: BSplineCurve PolesCount=3 KnotsCount=2 Degree=2 IsPeriodic=0
    g16: GeomPoint X=-48.5 Y=27 Z=0
    g17: GeomPoint X=12.5 Y=27 Z=0
  constraints (16):
    c: Weight(g6) = 1
    c: Equal(g6,g7)
    c: Equal(g6,g8)
    c: InternalAlignment(g6,g9)
    c: InternalAlignment(g7,g9)
    c: InternalAlignment(g8,g9)
    c: InternalAlignment(g10,g9)
    c: InternalAlignment(g11,g9)
    c: Weight(g12) = 1
    c: Equal(g12,g13)
    c: Equal(g12,g14)
    c: InternalAlignment(g12,g15)
    c: InternalAlignment(g13,g15)
    c: InternalAlignment(g14,g15)
    c: InternalAlignment(g16,g15)
    c: InternalAlignment(g17,g15)
FEATURE [Part::Box] Box123  label="Würfel113"
  AttacherType = Attacher::AttachEngine3D
  Height = 10
  Length = 40
  Placement = pos=(-14,-72,-42) rot=(0,0,1;0rad)
  Width = 10
FEATURE [Part::Cylinder] Cylinder205  label="Zylinder205"
  Angle = 360
  AttacherType = Attacher::AttachEngine3D
  FirstAngle = 0
  Height = 3.5
  Placement = pos=(-52.5,23,-36) rot=(0,0,1;0rad)
  Radius = 3.25
  SecondAngle = 0
FEATURE [PartDesign::Pad] Pad016
  AllowMultiFace = false
  Direction = (1,1,1)
  Length = 4
  Length2 = 100
  Profile = -> Sketch017
  Type = 0
FEATURE [PartDesign::Body] Body007
  Group = -> [Sketch017,Pad016]
  Origin = -> Origin015
  Placement = pos=(0,0,-38) rot=(0,0,1;0rad)
  Tip = -> Pad016
FEATURE [Part::Cylinder] Cylinder206  label="Zylinder206"
  Angle = 360
  AttacherType = Attacher::AttachEngine3D
  FirstAngle = 0
  Height = 9.5
  Placement = pos=(-52.5,23,-39) rot=(0,0,1;0rad)
  Radius = 0.6
  SecondAngle = 0
FEATURE [PartDesign::Pad] Pad017
  AllowMultiFace = false
  Direction = (1,1,1)
  Length = 4
  Length2 = 100
  Profile = -> Sketch016
  Type = 0
FEATURE [PartDesign::Body] Body008
  Group = -> [Sketch016,Pad017]
  Origin = -> Origin016
  Placement = pos=(0,0,-38) rot=(0,0,1;0rad)
  Tip = -> Pad017
FEATURE [Part::Cylinder] Cylinder207  label="Zylinder207"
  Angle = 360
  AttacherType = Attacher::AttachEngine3D
  FirstAngle = 0
  Height = 3.5
  Placement = pos=(16.5,23,-36) rot=(0,0,1;0rad)
  Radius = 3.25
  SecondAngle = 0
FEATURE [Part::Cylinder] Cylinder208  label="Zylinder208"
  Angle = 360
  AttacherType = Attacher::AttachEngine3D
  FirstAngle = 0
  Height = 9.5
  Placement = pos=(16.5,23,-39) rot=(0,0,1;0rad)
  Radius = 0.6
  SecondAngle = 0
FEATURE [Part::MultiFuse] Fusion134
  Shapes = -> [Cylinder207,Cylinder205,Cylinder208,Cylinder206]
FEATURE [Part::Cut] Cut086
  Base = -> Body008
  Tool = -> Fusion134
FEATURE [Part::Cylinder] Cylinder209  label="Zylinder209"
  Angle = 360
  AttacherType = Attacher::AttachEngine3D
  FirstAngle = 0
  Height = 3.5
  Placement = pos=(16.5,23,-36) rot=(0,0,1;0rad)
  Radius = 3.25
  SecondAngle = 0
FEATURE [Part::Cylinder] Cylinder210  label="Zylinder210"
  Angle = 360
  AttacherType = Attacher::AttachEngine3D
  FirstAngle = 0
  Height = 9.5
  Placement = pos=(-52.5,23,-39) rot=(0,0,1;0rad)
  Radius = 0.6
  SecondAngle = 0
FEATURE [Part::Box] Box125  label="Würfel115"
  AttacherType = Attacher::AttachEngine3D
  Height = 10
  Length = 40
  Placement = pos=(-14,-72,-42) rot=(0,0,1;0rad)
  Width = 10
FEATURE [Part::Cylinder] Cylinder211  label="Zylinder211"
  Angle = 360
  AttacherType = Attacher::AttachEngine3D
  FirstAngle = 0
  Height = 3.5
  Placement = pos=(-52.5,23,-36) rot=(0,0,1;0rad)
  Radius = 3.25
  SecondAngle = 0
FEATURE [Part::Cylinder] Cylinder212  label="Zylinder212"
  Angle = 360
  AttacherType = Attacher::AttachEngine3D
  FirstAngle = 0
  Height = 9.5
  Placement = pos=(16.5,23,-39) rot=(0,0,1;0rad)
  Radius = 0.6
  SecondAngle = 0
FEATURE [Part::MultiFuse] Fusion135
  Shapes = -> [Cylinder209,Cylinder211,Cylinder212,Cylinder210]
FEATURE [Part::Cut] Cut088
  Base = -> Body007
  Tool = -> Fusion135
FEATURE [Part::Box] Box126  label="Würfel116"
  AttacherType = Attacher::AttachEngine3D
  Height = 4
  Length = 90
  Placement = pos=(-63,-27.5,-41) rot=(0,0,1;0rad)
  Width = 9
FEATURE [Part::Fillet] Fillet086
  Base = -> Cut086
  Edges = 4 edges r=3: [Edge5,Edge8,Edge25,Edge26]
  Placement = pos=(0,-90,0) rot=(0,0,1;0rad)
FEATURE [Part::Cut] Cut087
  Base = -> Fillet086
  Placement = pos=(-3,44,0) rot=(0,0,1;0rad)
  Tool = -> Box123
FEATURE [Part::Fillet] Fillet087
  Base = -> Cut088
  Edges = 4 edges r=3: [Edge5,Edge8,Edge25,Edge26]
  Placement = pos=(0,-90,0) rot=(0,0,1;0rad)
FEATURE [Part::Cut] Cut090
  Base = -> Fillet087
  Placement = pos=(-5,35,0) rot=(0,0,1;0rad)
  Tool = -> Box125
FEATURE [Part::Mirroring] Part__Mirroring004  label="Cut068 (Mirror #4)001"
  Base = (-40.5,-7.62939e-06,-36)
  Normal = (0,1,-1.19209e-07)
  Placement = pos=(-38,9,0) rot=(0,0,1;3.14159rad)
  Source = -> Cut090
FEATURE [Part::MultiFuse] Fusion136
  Shapes = -> [Cut087,Part__Mirroring004]
FEATURE [Part::Cut] Cut091  label="bar_medium_long"
  Base = -> Fusion136
  Tool = -> Box126
FEATURE [Sketcher::SketchObject] Sketch018
  FullyConstrained = false
  MapMode = 5
  Support = -> [XY_Plane017]
  sketch-geometry (18):
    g0: LineSegment StartX=-57 StartY=19 StartZ=0 EndX=-57 EndY=27 EndZ=0
    g1: LineSegment StartX=-57 StartY=19 StartZ=0 EndX=-48.5 EndY=19 EndZ=0
    g2: LineSegment StartX=-57 StartY=27 StartZ=0 EndX=-48.5 EndY=27 EndZ=0
    g3: LineSegment StartX=12.5 StartY=19 StartZ=0 EndX=21 EndY=19 EndZ=0
    g4: LineSegment StartX=21 StartY=19 StartZ=0 EndX=21 EndY=27 EndZ=0
    g5: LineSegment StartX=21 StartY=27 StartZ=0 EndX=12.5 EndY=27 EndZ=0
    g6: Circle CenterX=-48.5 CenterY=19 CenterZ=0 NormalX=0 NormalY=0 NormalZ=1 AngleXU=0 Radius=5
    g7: Circle CenterX=-18 CenterY=24 CenterZ=0 NormalX=0 NormalY=0 NormalZ=1 AngleXU=0 Radius=5
    g8: Circle CenterX=12.5 CenterY=19 CenterZ=0 NormalX=0 NormalY=0 NormalZ=1 AngleXU=0 Radius=5
    g9: BSplineCurve PolesCount=3 KnotsCount=2 Degree=2 IsPeriodic=0
    g10: GeomPoint X=-48.5 Y=19 Z=0
    g11: GeomPoint X=12.5 Y=19 Z=0
    g12: Circle CenterX=-48.5 CenterY=27 CenterZ=0 NormalX=0 NormalY=0 NormalZ=1 AngleXU=0 Radius=5
    g13: Circle CenterX=-18 CenterY=22 CenterZ=0 NormalX=0 NormalY=0 NormalZ=1 AngleXU=0 Radius=5
    g14: Circle CenterX=12.5 CenterY=27 CenterZ=0 NormalX=0 NormalY=0 NormalZ=1 AngleXU=0 Radius=5
    g15: BSplineCurve PolesCount=3 KnotsCount=2 Degree=2 IsPeriodic=0
    g16: GeomPoint X=-48.5 Y=27 Z=0
    g17: GeomPoint X=12.5 Y=27 Z=0
  constraints (16):
    c: Weight(g6) = 1
    c: Equal(g6,g7)
    c: Equal(g6,g8)
    c: InternalAlignment(g6,g9)
    c: InternalAlignment(g7,g9)
    c: InternalAlignment(g8,g9)
    c: InternalAlignment(g10,g9)
    c: InternalAlignment(g11,g9)
    c: Weight(g12) = 1
    c: Equal(g12,g13)
    c: Equal(g12,g14)
    c: InternalAlignment(g12,g15)
    c: InternalAlignment(g13,g15)
    c: InternalAlignment(g14,g15)
    c: InternalAlignment(g16,g15)
    c: InternalAlignment(g17,g15)
FEATURE [Sketcher::SketchObject] Sketch019
  FullyConstrained = false
  MapMode = 5
  Support = -> [XY_Plane018]
  sketch-geometry (18):
    g0: LineSegment StartX=-57 StartY=19 StartZ=0 EndX=-57 EndY=27 EndZ=0
    g1: LineSegment StartX=-57 StartY=19 StartZ=0 EndX=-48.5 EndY=19 EndZ=0
    g2: LineSegment StartX=-57 StartY=27 StartZ=0 EndX=-48.5 EndY=27 EndZ=0
    g3: LineSegment StartX=12.5 StartY=19 StartZ=0 EndX=21 EndY=19 EndZ=0
    g4: LineSegment StartX=21 StartY=19 StartZ=0 EndX=21 EndY=27 EndZ=0
    g5: LineSegment StartX=21 StartY=27 StartZ=0 EndX=12.5 EndY=27 EndZ=0
    g6: Circle CenterX=-48.5 CenterY=19 CenterZ=0 NormalX=0 NormalY=0 NormalZ=1 AngleXU=0 Radius=5
    g7: Circle CenterX=-18 CenterY=24 CenterZ=0 NormalX=0 NormalY=0 NormalZ=1 AngleXU=0 Radius=5
    g8: Circle CenterX=12.5 CenterY=19 CenterZ=0 NormalX=0 NormalY=0 NormalZ=1 AngleXU=0 Radius=5
    g9: BSplineCurve PolesCount=3 KnotsCount=2 Degree=2 IsPeriodic=0
    g10: GeomPoint X=-48.5 Y=19 Z=0
    g11: GeomPoint X=12.5 Y=19 Z=0
    g12: Circle CenterX=-48.5 CenterY=27 CenterZ=0 NormalX=0 NormalY=0 NormalZ=1 AngleXU=0 Radius=5
    g13: Circle CenterX=-18 CenterY=22 CenterZ=0 NormalX=0 NormalY=0 NormalZ=1 AngleXU=0 Radius=5
    g14: Circle CenterX=12.5 CenterY=27 CenterZ=0 NormalX=0 NormalY=0 NormalZ=1 AngleXU=0 Radius=5
    g15: BSplineCurve PolesCount=3 KnotsCount=2 Degree=2 IsPeriodic=0
    g16: GeomPoint X=-48.5 Y=27 Z=0
    g17: GeomPoint X=12.5 Y=27 Z=0
  constraints (16):
    c: Weight(g6) = 1
    c: Equal(g6,g7)
    c: Equal(g6,g8)
    c: InternalAlignment(g6,g9)
    c: InternalAlignment(g7,g9)
    c: InternalAlignment(g8,g9)
    c: InternalAlignment(g10,g9)
    c: InternalAlignment(g11,g9)
    c: Weight(g12) = 1
    c: Equal(g12,g13)
    c: Equal(g12,g14)
    c: InternalAlignment(g12,g15)
    c: InternalAlignment(g13,g15)
    c: InternalAlignment(g14,g15)
    c: InternalAlignment(g16,g15)
    c: InternalAlignment(g17,g15)
FEATURE [Part::Cylinder] Cylinder213  label="Zylinder213"
  Angle = 360
  AttacherType = Attacher::AttachEngine3D
  FirstAngle = 0
  Height = 9.5
  Placement = pos=(16.5,23,-39) rot=(0,0,1;0rad)
  Radius = 0.6
  SecondAngle = 0
FEATURE [Part::Cylinder] Cylinder214  label="Zylinder214"
  Angle = 360
  AttacherType = Attacher::AttachEngine3D
  FirstAngle = 0
  Height = 9.5
  Placement = pos=(-52.5,23,-39) rot=(0,0,1;0rad)
  Radius = 0.6
  SecondAngle = 0
FEATURE [Part::Cylinder] Cylinder215  label="Zylinder215"
  Angle = 360
  AttacherType = Attacher::AttachEngine3D
  FirstAngle = 0
  Height = 9.5
  Placement = pos=(-52.5,23,-39) rot=(0,0,1;0rad)
  Radius = 0.6
  SecondAngle = 0
FEATURE [Part::Box] Box127  label="Würfel117"
  AttacherType = Attacher::AttachEngine3D
  Height = 10
  Length = 40
  Placement = pos=(-14,-72,-42) rot=(0,0,1;0rad)
  Width = 10
FEATURE [Part::Cylinder] Cylinder216  label="Zylinder216"
  Angle = 360
  AttacherType = Attacher::AttachEngine3D
  FirstAngle = 0
  Height = 3.5
  Placement = pos=(16.5,23,-36) rot=(0,0,1;0rad)
  Radius = 3.25
  SecondAngle = 0
FEATURE [PartDesign::Pad] Pad018
  AllowMultiFace = false
  Direction = (1,1,1)
  Length = 4
  Length2 = 100
  Profile = -> Sketch019
  Type = 0
FEATURE [PartDesign::Body] Body010
  Group = -> [Sketch019,Pad018]
  Origin = -> Origin017
  Placement = pos=(0,0,-38) rot=(0,0,1;0rad)
  Tip = -> Pad018
FEATURE [Part::Cylinder] Cylinder217  label="Zylinder217"
  Angle = 360
  AttacherType = Attacher::AttachEngine3D
  FirstAngle = 0
  Height = 3.5
  Placement = pos=(16.5,23,-36) rot=(0,0,1;0rad)
  Radius = 3.25
  SecondAngle = 0
FEATURE [Part::Box] Box128  label="Würfel118"
  AttacherType = Attacher::AttachEngine3D
  Height = 10
  Length = 40
  Placement = pos=(-14,-72,-42) rot=(0,0,1;0rad)
  Width = 10
FEATURE [Part::Cylinder] Cylinder218  label="Zylinder218"
  Angle = 360
  AttacherType = Attacher::AttachEngine3D
  FirstAngle = 0
  Height = 3.5
  Placement = pos=(-52.5,23,-36) rot=(0,0,1;0rad)
  Radius = 3.25
  SecondAngle = 0
FEATURE [PartDesign::Pad] Pad019
  AllowMultiFace = false
  Direction = (1,1,1)
  Length = 4
  Length2 = 100
  Profile = -> Sketch018
  Type = 0
FEATURE [PartDesign::Body] Body009
  Group = -> [Sketch018,Pad019]
  Origin = -> Origin018
  Placement = pos=(0,0,-38) rot=(0,0,1;0rad)
  Tip = -> Pad019
FEATURE [Part::Box] Box129  label="Würfel119"
  AttacherType = Attacher::AttachEngine3D
  Height = 4
  Length = 90
  Placement = pos=(-63,-27.5,-41) rot=(0,0,1;0rad)
  Width = 9
FEATURE [Part::Cylinder] Cylinder219  label="Zylinder219"
  Angle = 360
  AttacherType = Attacher::AttachEngine3D
  FirstAngle = 0
  Height = 9.5
  Placement = pos=(16.5,23,-39) rot=(0,0,1;0rad)
  Radius = 0.6
  SecondAngle = 0
FEATURE [Part::Cylinder] Cylinder220  label="Zylinder220"
  Angle = 360
  AttacherType = Attacher::AttachEngine3D
  FirstAngle = 0
  Height = 3.5
  Placement = pos=(-52.5,23,-36) rot=(0,0,1;0rad)
  Radius = 3.25
  SecondAngle = 0
FEATURE [Part::MultiFuse] Fusion137
  Shapes = -> [Cylinder217,Cylinder220,Cylinder213,Cylinder215]
FEATURE [Part::Cut] Cut095
  Base = -> Body010
  Tool = -> Fusion137
FEATURE [Part::Fillet] Fillet089
  Base = -> Cut095
  Edges = 4 edges r=3: [Edge5,Edge8,Edge25,Edge26]
  Placement = pos=(0,-90,0) rot=(0,0,1;0rad)
FEATURE [Part::Cut] Cut093
  Base = -> Fillet089
  Placement = pos=(-3,44,0) rot=(0,0,1;0rad)
  Tool = -> Box127
FEATURE [Part::MultiFuse] Fusion138
  Shapes = -> [Cylinder216,Cylinder218,Cylinder219,Cylinder214]
FEATURE [Part::Cut] Cut094
  Base = -> Body009
  Tool = -> Fusion138
FEATURE [Part::Fillet] Fillet088
  Base = -> Cut094
  Edges = 4 edges r=3: [Edge5,Edge8,Edge25,Edge26]
  Placement = pos=(0,-90,0) rot=(0,0,1;0rad)
FEATURE [Part::Cut] Cut096
  Base = -> Fillet088
  Placement = pos=(-5,35,0) rot=(0,0,1;0rad)
  Tool = -> Box128
FEATURE [Part::Mirroring] Part__Mirroring005  label="Cut068 (Mirror #4)002"
  Base = (-40.5,-7.62939e-06,-36)
  Normal = (0,1,-1.19209e-07)
  Placement = pos=(-38,9,0) rot=(0,0,1;3.14159rad)
  Source = -> Cut096
FEATURE [Part::MultiFuse] Fusion139
  Shapes = -> [Cut093,Part__Mirroring005]
FEATURE [Part::Cut] Cut092
  Base = -> Fusion139
  Placement = pos=(0,46,0) rot=(0,0,1;0rad)
  Tool = -> Box129
FEATURE [App::DocumentObjectGroup] Gruppe009  label="bar"
  Group = -> [Cut091,Cut092]
FEATURE [App::DocumentObjectGroup] Gruppe018  label="leg_front_right_source"
  Group = -> [Fillet070,YZ_Plane018]
FEATURE [App::DocumentObjectGroup] Gruppe019  label="leg_centre_left_source"
  Group = -> [YZ_Plane013]
FEATURE [App::DocumentObjectGroup] Gruppe020  label="base_source"
  Group = -> [Cut072,Fillet080]
FEATURE [App::DocumentObjectGroup] Gruppe021  label="leg_front_left_source"
  Group = -> [YZ_Plane014,Body]
FEATURE [App::DocumentObjectGroup] Gruppe022  label="leg_rear_left_source"
  Group = -> [Cut060]
FEATURE [Part::MultiFuse] Fusion140
  Placement = pos=(0,0,-0.5) rot=(0,0,1;0rad)
  Shapes = -> [Box084,Box122]
FEATURE [App::DocumentObjectGroup] Gruppe014  label="boards"
  Group = -> [Fusion140]
FEATURE [Part::Box] Box130  label="Würfel120"
  AttacherType = Attacher::AttachEngine3D
  Height = 6
  Length = 60
  Placement = pos=(-42,-15,13) rot=(0,0,1;0rad)
  Width = 30
FEATURE [Part::Cylinder] Cylinder221  label="Zylinder221"
  Angle = 360
  AttacherType = Attacher::AttachEngine3D
  FirstAngle = 0
  Height = 12
  Placement = pos=(-40.5,17.5,8) rot=(0,0,1;0rad)
  Radius = 1.5
  SecondAngle = 0
FEATURE [Part::Cylinder] Cylinder222  label="Zylinder222"
  Angle = 360
  AttacherType = Attacher::AttachEngine3D
  FirstAngle = 0
  Height = 12
  Placement = pos=(-40.5,-17.5,8) rot=(0,0,1;0rad)
  Radius = 1.5
  SecondAngle = 0
FEATURE [Part::Cylinder] Cylinder223  label="Zylinder223"
  Angle = 360
  AttacherType = Attacher::AttachEngine3D
  FirstAngle = 0
  Height = 12
  Placement = pos=(25.5,-17.5,8) rot=(0,0,1;0rad)
  Radius = 1.5
  SecondAngle = 0
FEATURE [Part::Cylinder] Cylinder224  label="Zylinder224"
  Angle = 360
  AttacherType = Attacher::AttachEngine3D
  FirstAngle = 0
  Height = 12
  Placement = pos=(25.5,17.5,8) rot=(0,0,1;0rad)
  Radius = 1.5
  SecondAngle = 0
FEATURE [Part::Box] Box131  label="Würfel121"
  AttacherType = Attacher::AttachEngine3D
  Height = 6
  Length = 12
  Placement = pos=(20,-15,13) rot=(0,0,1;0rad)
  Width = 30
FEATURE [Part::Box] Box132  label="Würfel122"
  AttacherType = Attacher::AttachEngine3D
  Height = 18
  Length = 10
  Placement = pos=(21.8,-2.5,-7) rot=(0,0,1;0rad)
  Width = 5
FEATURE [Part::Cylinder] Cylinder225  label="Zylinder225"
  Angle = 360
  AttacherType = Attacher::AttachEngine3D
  FirstAngle = 0
  Height = 17
  Placement = pos=(28.75,0,-10) rot=(0,0,1;0rad)
  Radius = 1
  SecondAngle = 0
FEATURE [Part::Chamfer] Chamfer021
  Base = -> Box132
  Edges = 2 edges: [Edge2 r1=17 r2=4,Edge6 r1=17 r2=0.8]
FEATURE [Part::Box] Box133  label="Würfel123"
  AttacherType = Attacher::AttachEngine3D
  Height = 4
  Length = 3.5
  Placement = pos=(26,-16.5,6) rot=(0,0,1;0rad)
  Width = 31
FEATURE [Part::Chamfer] Chamfer022
  Base = -> Box133
  Edges = 2 edges: [Edge9 r1=3.9 r2=14,Edge11 r1=3.9 r2=14]
  Placement = pos=(0,1,-1) rot=(0,0,1;0rad)
FEATURE [Part::Box] Box134  label="Würfel124"
  AttacherType = Attacher::AttachEngine3D
  Height = 6
  Length = 25
  Placement = pos=(-70,-22.5,13) rot=(0,0,1;0rad)
  Width = 45
FEATURE [Part::MultiFuse] Fusion142
  Shapes = -> [Box134,Box116,Box130,Cylinder224,Box131,Cylinder222,Cylinder221,Cylinder223]
FEATURE [Part::Cut] Cut097
  Base = -> Fillet082
  Tool = -> Fusion142
FEATURE [Part::Box] Box136  label="Würfel126"
  AttacherType = Attacher::AttachEngine3D
  Height = 21
  Length = 6
  Placement = pos=(-11.5,11,-7) rot=(0,0,1;0rad)
  Width = 10
FEATURE [Part::Cut] Cut098
  Base = -> Chamfer021
  Tool = -> Cylinder225
FEATURE [Part::Cylinder] Cylinder226  label="Zylinder226"
  Angle = 360
  AttacherType = Attacher::AttachEngine3D
  FirstAngle = 0
  Height = 21
  Placement = pos=(-8.5,17,-10) rot=(0,0,1;0rad)
  Radius = 1.5
  SecondAngle = 0
FEATURE [Part::Box] Box137  label="Würfel127"
  AttacherType = Attacher::AttachEngine3D
  Height = 21
  Length = 8
  Placement = pos=(-12.5,5.5,-3) rot=(0,0,1;0rad)
  Width = 10
FEATURE [Part::Box] Box138  label="Würfel128"
  AttacherType = Attacher::AttachEngine3D
  Height = 21
  Length = 8
  Placement = pos=(-12.5,8.5,-3) rot=(0,0,1;0rad)
  Width = 10
FEATURE [Part::Box] Box139  label="Würfel129"
  AttacherType = Attacher::AttachEngine3D
  Height = 3
  Length = 56
  Placement = pos=(-43.5,20,-7) rot=(0,0,1;0rad)
  Width = 1
FEATURE [Part::Box] Box140  label="Würfel130"
  AttacherType = Attacher::AttachEngine3D
  Height = 21
  Length = 8
  Placement = pos=(-12.5,5.5,-3) rot=(0,0,1;0rad)
  Width = 10
FEATURE [Part::Box] Box141  label="Würfel131"
  AttacherType = Attacher::AttachEngine3D
  Height = 21
  Length = 8
  Placement = pos=(-12.5,8.5,-3) rot=(0,0,1;0rad)
  Width = 10
FEATURE [Part::Box] Box142  label="Würfel132"
  AttacherType = Attacher::AttachEngine3D
  Height = 21
  Length = 6
  Placement = pos=(-11.5,11,-7) rot=(0,0,1;0rad)
  Width = 10
FEATURE [Part::Cylinder] Cylinder227  label="Zylinder227"
  Angle = 360
  AttacherType = Attacher::AttachEngine3D
  FirstAngle = 0
  Height = 21
  Placement = pos=(-8.5,17,-10) rot=(0,0,1;0rad)
  Radius = 1.5
  SecondAngle = 0
FEATURE [Part::Box] Box143  label="Würfel133"
  AttacherType = Attacher::AttachEngine3D
  Height = 8
  Length = 14
  Placement = pos=(19,-13.5,12.5) rot=(0,0,1;0rad)
  Width = 27
FEATURE [Part::Box] Box144  label="Würfel134"
  AttacherType = Attacher::AttachEngine3D
  Height = 7
  Length = 11
  Placement = pos=(20,-15.5,11) rot=(0,0,1;0rad)
  Width = 31
FEATURE [Part::Cut] Cut101
  Base = -> Box144
  Tool = -> Box143
FEATURE [Part::Cylinder] Cylinder228  label="Zylinder228"
  Angle = 360
  AttacherType = Attacher::AttachEngine3D
  FirstAngle = 0
  Height = 21
  Placement = pos=(-8.5,17,-3) rot=(0,0,1;0rad)
  Radius = 2
  SecondAngle = 0
FEATURE [Part::MultiFuse] Fusion144
  Shapes = -> [Box110,Cylinder226,Box138,Box137,Cylinder228]
FEATURE [Part::Cut] Cut099
  Base = -> Box136
  Tool = -> Fusion144
FEATURE [Part::Cylinder] Cylinder229  label="Zylinder229"
  Angle = 360
  AttacherType = Attacher::AttachEngine3D
  FirstAngle = 0
  Height = 21
  Placement = pos=(-8.5,17,-3) rot=(0,0,1;0rad)
  Radius = 2
  SecondAngle = 0
FEATURE [Part::MultiFuse] Fusion145
  Shapes = -> [Box139,Cylinder227,Box141,Box140,Cylinder229]
FEATURE [Part::Cut] Cut100
  Base = -> Box142
  Placement = pos=(-17,2e-15,0) rot=(0,0,1;3.14159rad)
  Tool = -> Fusion145
FEATURE [Part::Box] Box145  label="Würfel135"
  AttacherType = Attacher::AttachEngine3D
  Height = 10
  Length = 11
  Placement = pos=(-12,14.5,-19) rot=(0,0,1;0rad)
  Width = 5
FEATURE [Part::Cylinder] Cylinder230  label="Zylinder230"
  Angle = 360
  AttacherType = Attacher::AttachEngine3D
  FirstAngle = 0
  Height = 15
  Placement = pos=(-8.5,17,-20) rot=(0,0,1;0rad)
  Radius = 1
  SecondAngle = 0
FEATURE [Part::Cut] Cut102
  Base = -> Box145
  Tool = -> Cylinder230
FEATURE [Part::Box] Box146  label="Würfel136"
  AttacherType = Attacher::AttachEngine3D
  Height = 10
  Length = 11
  Placement = pos=(-12,13.5,-19) rot=(0,0,1;0rad)
  Width = 5
FEATURE [Part::Cylinder] Cylinder231  label="Zylinder231"
  Angle = 360
  AttacherType = Attacher::AttachEngine3D
  FirstAngle = 0
  Height = 15
  Placement = pos=(-8.5,16,-20) rot=(0,0,1;0rad)
  Radius = 1
  SecondAngle = 0
FEATURE [Part::Cut] Cut103
  Base = -> Box146
  Placement = pos=(0,-33.5,0) rot=(0,0,1;0rad)
  Tool = -> Cylinder231
FEATURE [Part::MultiFuse] Fusion147
  Shapes = -> [Fusion131,Cut103,Cut102]
FEATURE [App::DocumentObjectGroup] Gruppe024  label="bar_unused"
  Group = -> [Cut061,Fillet075,Fillet076,Cut070]
FEATURE [App::DocumentObjectGroup] Gruppe025  label="board_image"
  Group = -> [ImagePlane]
FEATURE [Part::Box] Box147  label="Würfel137"
  AttacherType = Attacher::AttachEngine3D
  Height = 6
  Length = 4
  Placement = pos=(-45,-9,9) rot=(0,0,1;0rad)
  Width = 18
FEATURE [Part::Box] Box148  label="Würfel138"
  AttacherType = Attacher::AttachEngine3D
  Height = 4
  Length = 10
  Placement = pos=(-51,-6,12) rot=(0,0,1;0rad)
  Width = 12
FEATURE [Part::Box] Box149  label="Würfel139"
  AttacherType = Attacher::AttachEngine3D
  Height = 6
  Length = 5
  Placement = pos=(-45,-3,6) rot=(0,0,1;0rad)
  Width = 6
FEATURE [Part::Box] Box150  label="Würfel140"
  AttacherType = Attacher::AttachEngine3D
  Height = 2
  Length = 24
  Placement = pos=(-66,-3,6) rot=(0,0,1;0rad)
  Width = 6
FEATURE [Part::Fillet] Fillet090
  Base = -> Box147
  Edges = 2 edges r=2: [Edge9,Edge11]
FEATURE [App::DocumentObjectGroup] Gruppe026  label="board_carrier_source"
FEATURE [Part::MultiFuse] Fusion148
  Shapes = -> [Box149,Box150,Fillet090]
FEATURE [Part::Box] Box151  label="Würfel141"
  AttacherType = Attacher::AttachEngine3D
  Height = 13.5
  Length = 5.5
  Placement = pos=(-66,-13,-7) rot=(0,0,1;0rad)
  Width = 26
FEATURE [Part::Cylinder] Cylinder232  label="Zylinder232"
  Angle = 360
  AttacherType = Attacher::AttachEngine3D
  FirstAngle = 0
  Height = 19
  Placement = pos=(-63.5,-10,-10) rot=(0,0,1;0rad)
  Radius = 1
  SecondAngle = 0
FEATURE [Part::Cylinder] Cylinder233  label="Zylinder233"
  Angle = 360
  AttacherType = Attacher::AttachEngine3D
  FirstAngle = 0
  Height = 19
  Placement = pos=(-63.5,10,-10) rot=(0,0,1;0rad)
  Radius = 1
  SecondAngle = 0
FEATURE [Part::Fillet] Fillet093
  Base = -> Box151
  Edges = 2 edges r=6: [Edge10,Edge12]
FEATURE [Part::Fillet] Fillet094
  Base = -> Fusion148
  Edges = 1 edges r=1: [Edge29]
FEATURE [Part::Box] Box152  label="Würfel142"
  AttacherType = Attacher::AttachEngine3D
  Height = 11.5
  Length = 8.5
  Placement = pos=(-67,-10,-7) rot=(0,0,1;0rad)
  Width = 14
FEATURE [Part::Fillet] Fillet095
  Base = -> Box152
  Edges = 2 edges r=3: [Edge10,Edge12]
  Placement = pos=(0,3,0) rot=(0,0,1;0rad)
FEATURE [Part::MultiFuse] Fusion149
  Shapes = -> [Fillet095,Cylinder233,Cylinder232]
FEATURE [Part::Cut] Cut104
  Base = -> Fillet093
  Tool = -> Fusion149
FEATURE [Part::MultiFuse] Fusion150
  Shapes = -> [Fillet094,Cut104]
FEATURE [Part::Fillet] Fillet092
  Base = -> Box148
  Edges = 4 edges r=1: [Edge9,Edge10,Edge11,Edge12]
  Placement = pos=(2,0,-1) rot=(0,0,1;0rad)
FEATURE [Part::Cylinder] Cylinder234  label="Zylinder234"
  Angle = 360
  AttacherType = Attacher::AttachEngine3D
  FirstAngle = 0
  Height = 10
  Placement = pos=(5.723,-13.7,22.15) rot=(0,-1,0;1.5708rad)
  Radius = 4
  SecondAngle = 0
FEATURE [Part::Box] Box153  label="Würfel143"
  AttacherType = Attacher::AttachEngine3D
  Height = 42.2
  Length = 2
  Placement = pos=(0,-19.5,-7) rot=(0,0,1;0rad)
  Width = 28
FEATURE [Part::Box] Box154  label="Würfel144"
  AttacherType = Attacher::AttachEngine3D
  Height = 10
  Length = 5
  Placement = pos=(-1.5,-3,28) rot=(0,0,1;0rad)
  Width = 13
FEATURE [Part::Box] Box155  label="Würfel145"
  AttacherType = Attacher::AttachEngine3D
  Height = 10
  Length = 5
  Placement = pos=(-1.5,-20.75,28) rot=(0,0,1;0rad)
  Width = 13
FEATURE [Part::Cylinder] Cylinder235  label="Zylinder235"
  Angle = 360
  AttacherType = Attacher::AttachEngine3D
  FirstAngle = 0
  Height = 10
  Placement = pos=(7.85,-5.4,32.7) rot=(0,-1,0;1.5708rad)
  Radius = 1.4
  SecondAngle = 0
FEATURE [Part::Cylinder] Cylinder020  label="Zylinder236"
  Angle = 360
  AttacherType = Attacher::AttachEngine3D
  FirstAngle = 0
  Height = 10
  Placement = pos=(5.723,2.55,22.15) rot=(0,-1,0;1.5708rad)
  Radius = 4
  SecondAngle = 0
FEATURE [Part::Box] Box156  label="Würfel007"
  AttacherType = Attacher::AttachEngine3D
  Height = 10
  Length = 5
  Placement = pos=(-1.5,-20.75,-9.75) rot=(0,0,1;0rad)
  Width = 13
FEATURE [Part::Box] Box157  label="Würfel146"
  AttacherType = Attacher::AttachEngine3D
  Height = 10
  Length = 5
  Placement = pos=(-1.5,-3,-9.75) rot=(0,0,1;0rad)
  Width = 13
FEATURE [Part::Cylinder] Cylinder019  label="Zylinder237"
  Angle = 360
  AttacherType = Attacher::AttachEngine3D
  FirstAngle = 0
  Height = 10
  Placement = pos=(7.95,-5.4,-4.5) rot=(0,-1,0;1.5708rad)
  Radius = 1.4
  SecondAngle = 0
FEATURE [Part::Cylinder] Cylinder236  label="Zylinder238"
  Angle = 360
  AttacherType = Attacher::AttachEngine3D
  FirstAngle = 0
  Height = 10
  Placement = pos=(5.723,2.55,6.15) rot=(0,-1,0;1.5708rad)
  Radius = 4
  SecondAngle = 0
FEATURE [Part::Cylinder] Cylinder237  label="Zylinder239"
  Angle = 360
  AttacherType = Attacher::AttachEngine3D
  FirstAngle = 0
  Height = 10
  Placement = pos=(5.723,-13.7,6.15) rot=(0,-1,0;1.5708rad)
  Radius = 4
  SecondAngle = 0
FEATURE [Part::Fillet] Fillet008
  Base = -> Box156
  Edges = 1 edges r=3: [Edge12]
FEATURE [Part::Fillet] Fillet009
  Base = -> Box155
  Edges = 1 edges r=3: [Edge11]
FEATURE [Part::Fillet] Fillet004
  Base = -> Box154
  Edges = 1 edges r=3: [Edge9]
FEATURE [Part::Fillet] Fillet007
  Base = -> Box157
  Edges = 1 edges r=3: [Edge10]
FEATURE [Part::MultiFuse] Fusion153
  Shapes = -> [Fillet004,Fillet009,Fillet007,Fillet008]
FEATURE [Part::MultiFuse] Fusion154
  Shapes = -> [Cylinder235,Cylinder019]
FEATURE [Part::MultiFuse] Fusion156
  Shapes = -> [Cylinder020,Cylinder234,Cylinder236,Cylinder237]
FEATURE [Part::Cut] Cut004
  Base = -> Box153
  Tool = -> Fusion153
FEATURE [Part::Fillet] Fillet010
  Base = -> Cut004
  Edges = 4 edges r=3: [Edge18,Edge19,Edge32,Edge35]
FEATURE [Part::Fillet] Fillet011
  Base = -> Fillet010
  Edges = 2 edges r=2.24: [Edge39,Edge42]
FEATURE [Part::Fillet] Fillet012
  Base = -> Fillet011
  Edges = 2 edges r=2.24: [Edge56,Edge60]
FEATURE [Part::Cut] Cut106
  Base = -> Fillet012
  Tool = -> Fusion154
FEATURE [Part::Fillet] Fillet013
  Base = -> Cut106
  Edges = 7 edges r=0.5: [Edge36,Edge41,Edge44,Edge49,Edge52,Edge57,Edge60]
FEATURE [Part::Fillet] Fillet096
  Base = -> Fillet013
  Edges = 1 edges r=0.5: [Edge17]
FEATURE [Part::Cut] Cut006
  Base = -> Fillet096
  Placement = pos=(54.5,-14,-11) rot=(-1,0,0;1.5708rad)
  Tool = -> Fusion156
FEATURE [Part::Feature] Part__Feature  label="Evo_mini_commercial"
  Placement = pos=(58.5,-71,-41.5) rot=(0.57735,0.57735,0.57735;4.18879rad)
  shape: bbox 13.71 x 42.61 x 30.53 mm, 936 faces, 0 solids (baked)
FEATURE [Part::Box] Box158  label="Würfel147"
  AttacherType = Attacher::AttachEngine3D
  Height = 11
  Length = 10
  Placement = pos=(-39,-23,-4) rot=(0,0,1;0rad)
  Width = 10
FEATURE [Part::Cut] Cut107
  Base = -> Chamfer017
  Tool = -> Box158
FEATURE [App::DocumentObjectGroup] Gruppe005  label="base"
  Group = -> [Cut107]
FEATURE [Part::MultiFuse] Fusion157
  Shapes = -> [Fusion150,Cut098,Cut097,Cut099,Cut100,Cut101]
FEATURE [Part::Cut] Cut108
  Base = -> Fusion157
  Tool = -> Fillet092
FEATURE [Part::Box] Box159  label="Würfel148"
  AttacherType = Attacher::AttachEngine3D
  Height = 10
  Length = 18
  Placement = pos=(25,-3.5,-10.5) rot=(0,0,1;0rad)
  Width = 7
FEATURE [Part::Cylinder] Cylinder238  label="Zylinder240"
  Angle = 360
  AttacherType = Attacher::AttachEngine3D
  FirstAngle = 0
  Height = 19
  Placement = pos=(28.75,0,-11.5) rot=(0,0,1;0rad)
  Radius = 1.4
  SecondAngle = 0
FEATURE [Part::Box] Box160  label="Würfel149"
  AttacherType = Attacher::AttachEngine3D
  Height = 18
  Length = 10
  Placement = pos=(21.8,-2.75,-7) rot=(0,0,1;0rad)
  Width = 5.5
FEATURE [Part::Chamfer] Chamfer023
  Base = -> Box160
  Edges = 2 edges: [Edge2 r1=17 r2=4,Edge6 r1=17 r2=0.8]
FEATURE [Part::Box] Box161  label="Würfel150"
  AttacherType = Attacher::AttachEngine3D
  Height = 2.2
  Length = 10
  Placement = pos=(22,-5,-9.1) rot=(0,0,1;0rad)
  Width = 10
FEATURE [Part::MultiFuse] Fusion158
  Shapes = -> [Cylinder238,Box161,Chamfer023]
FEATURE [Part::Cylinder] Cylinder239  label="Zylinder241"
  Angle = 360
  AttacherType = Attacher::AttachEngine3D
  FirstAngle = 0
  Height = 10
  Placement = pos=(37.5,5,-5.5) rot=(1,0,0;1.5708rad)
  Radius = 2
  SecondAngle = 0
FEATURE [Part::Fillet] Fillet097
  Base = -> Box159
  Edges = 2 edges r=4.9: [Edge6,Edge8]
FEATURE [Part::MultiFuse] Fusion159
  Shapes = -> [Cylinder239,Fusion158]
FEATURE [Part::Cut] Cut109
  Base = -> Fillet097
  Tool = -> Fusion159
FEATURE [Part::Box] Box162  label="Würfel151"
  AttacherType = Attacher::AttachEngine3D
  Height = 12
  Length = 16
  Placement = pos=(28.5,-3.75,-11.5) rot=(0,0,1;0rad)
  Width = 7.5
FEATURE [Part::Box] Box163  label="Würfel152"
  AttacherType = Attacher::AttachEngine3D
  Height = 10
  Length = 22
  Placement = pos=(27,-3.5,-10.5) rot=(0,0,1;0rad)
  Width = 12
FEATURE [Part::Fillet] Fillet099
  Base = -> Box163
  Edges = 2 edges r=4.9: [Edge6,Edge8]
  Placement = pos=(82,-2.5,-11) rot=(0,1,0;3.14159rad)
FEATURE [Part::Cylinder] Cylinder240  label="Zylinder242"
  Angle = 360
  AttacherType = Attacher::AttachEngine3D
  FirstAngle = 0
  Height = 15
  Placement = pos=(37.5,7.5,-5.5) rot=(1,0,0;1.5708rad)
  Radius = 2
  SecondAngle = 0
FEATURE [Part::MultiFuse] Fusion160
  Shapes = -> [Cylinder240,Box162]
FEATURE [Part::Cut] Cut110
  Base = -> Fillet099
  Tool = -> Fusion160
FEATURE [Part::MultiFuse] Fusion161
  Shapes = -> [Cut006,Cut110]
FEATURE [Part::Box] Box164  label="Würfel153"
  AttacherType = Attacher::AttachEngine3D
  Height = 3
  Length = 7
  Placement = pos=(21,-5,-12) rot=(0,0,1;0rad)
  Width = 10
FEATURE [Part::Cylinder] Cylinder241  label="Zylinder243"
  Angle = 360
  AttacherType = Attacher::AttachEngine3D
  FirstAngle = 0
  Height = 10
  Placement = pos=(28.5,0,-16.5) rot=(0,0,1;0rad)
  Radius = 2.8
  SecondAngle = 0
FEATURE [Part::Cut] Cut111
  Base = -> Box164
  Tool = -> Cylinder241
FEATURE [Part::Cut] Cut112
  Base = -> Cut109
  Tool = -> Cut111
FEATURE [App::DocumentObjectGroup] Gruppe027  label="sensor_evo_mini"
  Group = -> [Part__Feature,Fusion161,Cut112]
FEATURE [Part::Cone] Cone  label="Kegel"
  Angle = 360
  AttacherType = Attacher::AttachEngine3D
  Height = 15
  Placement = pos=(20,49,-50) rot=(0,0,1;0rad)
  Radius1 = 2
  Radius2 = 4
FEATURE [Sketcher::SketchObject] Sketch020
  FullyConstrained = false
  MapMode = 5
  Placement = pos=(0,0,0) rot=(0.57735,0.57735,0.57735;2.0944rad)
  Support = -> [YZ_Plane030]
  sketch-geometry (50):
    g0: LineSegment StartX=4 StartY=4 StartZ=0 EndX=4 EndY=10 EndZ=0
    g1: LineSegment StartX=4 StartY=10 StartZ=0 EndX=21 EndY=10 EndZ=0
    g2: LineSegment StartX=5 StartY=-29 StartZ=0 EndX=18 EndY=-29 EndZ=0
    g3: LineSegment StartX=5 StartY=-29 StartZ=0 EndX=5 EndY=-33 EndZ=0
    g4: LineSegment StartX=5 StartY=-33 StartZ=0 EndX=28 EndY=-33 EndZ=0
    g5: LineSegment StartX=4 StartY=4 StartZ=0 EndX=16 EndY=4 EndZ=0
    g6: LineSegment StartX=16 StartY=4 StartZ=0 EndX=21 EndY=6 EndZ=0
    g7: Circle CenterX=21 CenterY=10 CenterZ=0 NormalX=0 NormalY=0 NormalZ=1 AngleXU=0 Radius=2
    g8: Circle CenterX=33 CenterY=12 CenterZ=0 NormalX=0 NormalY=0 NormalZ=1 AngleXU=0 Radius=2
    g9: Circle CenterX=40 CenterY=18 CenterZ=0 NormalX=0 NormalY=0 NormalZ=1 AngleXU=0 Radius=2
    g10: BSplineCurve PolesCount=3 KnotsCount=2 Degree=2 IsPeriodic=0
    g11: GeomPoint X=21 Y=10 Z=0
    g12: GeomPoint X=40 Y=18 Z=0
    g13: Circle CenterX=40 CenterY=18 CenterZ=0 NormalX=0 NormalY=0 NormalZ=1 AngleXU=0 Radius=1
    g14: Circle CenterX=42 CenterY=12 CenterZ=0 NormalX=0 NormalY=0 NormalZ=1 AngleXU=0 Radius=1
    g15: Circle CenterX=49 CenterY=7 CenterZ=0 NormalX=0 NormalY=0 NormalZ=1 AngleXU=0 Radius=1
    g16: BSplineCurve PolesCount=3 KnotsCount=2 Degree=2 IsPeriodic=0
    g17: GeomPoint X=40 Y=18 Z=0
    g18: GeomPoint X=49 Y=7 Z=0
    g19: Circle CenterX=49 CenterY=7 CenterZ=0 NormalX=0 NormalY=0 NormalZ=1 AngleXU=0 Radius=8
    g20: Circle CenterX=50 CenterY=-43 CenterZ=0 NormalX=0 NormalY=0 NormalZ=1 AngleXU=0 Radius=8
    g21: BSplineCurve PolesCount=2 KnotsCount=2 Degree=1 IsPeriodic=0
    g22: GeomPoint X=49 Y=7 Z=0
    g23: GeomPoint X=50 Y=-43 Z=0
    g24: Circle CenterX=48 CenterY=-43 CenterZ=0 NormalX=0 NormalY=0 NormalZ=1 AngleXU=0 Radius=8
    g25: Circle CenterX=48 CenterY=10 CenterZ=0 NormalX=0 NormalY=0 NormalZ=1 AngleXU=0 Radius=8
    g26: Circle CenterX=38 CenterY=10 CenterZ=0 NormalX=0 NormalY=0 NormalZ=1 AngleXU=0 Radius=8
    g27: BSplineCurve PolesCount=3 KnotsCount=2 Degree=2 IsPeriodic=0
    g28: GeomPoint X=48 Y=-43 Z=0
    g29: GeomPoint X=38 Y=10 Z=0
    g30: LineSegment StartX=48 StartY=-43 StartZ=0 EndX=50 EndY=-43 EndZ=0
    g31: Circle CenterX=28 CenterY=-33 CenterZ=0 NormalX=0 NormalY=0 NormalZ=1 AngleXU=0 Radius=4
    g32: Circle CenterX=31.5452 CenterY=5.41621 CenterZ=0 NormalX=0 NormalY=0 NormalZ=1 AngleXU=0 Radius=4
    g33: Circle CenterX=38 CenterY=10 CenterZ=0 NormalX=0 NormalY=0 NormalZ=1 AngleXU=0 Radius=4
    g34: BSplineCurve PolesCount=3 KnotsCount=2 Degree=2 IsPeriodic=0
    g35: GeomPoint X=28 Y=-33 Z=0
    g36: GeomPoint X=38 Y=10 Z=0
    g37-g43: Circle x7 (B-spline internal-alignment scaffolding for g44; pole/knot coordinates omitted)
    g44: BSplineCurve PolesCount=7 KnotsCount=5 Degree=3 IsPeriodic=0
    g45-g49: GeomPoint x5 (B-spline internal-alignment scaffolding for g44; pole/knot coordinates omitted)
  constraints (42):
    c: Weight(g7) = 1
    c: Equal(g7,g8)
    c: Equal(g7,g9)
    c: InternalAlignment(g7,g10)
    c: InternalAlignment(g8,g10)
    c: InternalAlignment(g9,g10)
    c: InternalAlignment(g11,g10)
    c: InternalAlignment(g12,g10)
    c: Weight(g13) = 1
    c: Equal(g13,g14)
    c: Equal(g13,g15)
    c: InternalAlignment(g13,g16)
    c: InternalAlignment(g14,g16)
    c: InternalAlignment(g15,g16)
    c: InternalAlignment(g17,g16)
    c: InternalAlignment(g18,g16)
    c: Weight(g19) = 1
    c: Equal(g19,g20)
    c: InternalAlignment(g19,g21)
    c: InternalAlignment(g20,g21)
    c: InternalAlignment(g22,g21)
    c: InternalAlignment(g23,g21)
    c: Weight(g24) = 1
    c: Equal(g24,g25)
    c: Equal(g24,g26)
    c: InternalAlignment(g24,g27)
    c: InternalAlignment(g25,g27)
    c: InternalAlignment(g26,g27)
    c: InternalAlignment(g28,g27)
    c: InternalAlignment(g29,g27)
    c: Weight(g31) = 1
    c: Equal(g31,g32)
    c: Equal(g31,g33)
    c: InternalAlignment(g31,g34)
    c: InternalAlignment(g32,g34)
    c: InternalAlignment(g33,g34)
    c: InternalAlignment(g35,g34)
    c: InternalAlignment(g36,g34)
    c: Weight(g37) = 1
    c: Equal(g37, g38-g43) x6
    c: InternalAlignment(g37-g43 -> g44) x7
    c: InternalAlignment(g45-g49 -> g44) x5
FEATURE [Part::Wedge] Wedge005  label="Keil005"
  AttacherType = Attacher::AttachEngine3D
  Placement = pos=(12.5,10,0) rot=(0,0,1;0rad)
  X2max = 6
  X2min = 2
  Xmax = 8
  Xmin = 0
  Ymax = 18
  Ymin = 0
  Z2max = 8
  Z2min = 2
  Zmax = 8
  Zmin = 2
FEATURE [Part::Box] Box165  label="Würfel154"
  AttacherType = Attacher::AttachEngine3D
  Height = 7
  Length = 7
  Placement = pos=(13,1,1) rot=(0,0,1;0rad)
  Width = 9
FEATURE [Part::Cylinder] Cylinder242  label="Zylinder244"
  Angle = 360
  AttacherType = Attacher::AttachEngine3D
  FirstAngle = 0
  Height = 14
  Placement = pos=(16.5,10,-2) rot=(0,0,1;0rad)
  Radius = 1.5
  SecondAngle = 0
FEATURE [Part::Cylinder] Cylinder243  label="Zylinder245"
  Angle = 360
  AttacherType = Attacher::AttachEngine3D
  FirstAngle = 0
  Height = 10
  Placement = pos=(16.5,10,-31.5) rot=(0,0,1;0rad)
  Radius = 3.15
  SecondAngle = 0
FEATURE [Part::Cylinder] Cylinder244  label="Zylinder246"
  Angle = 360
  AttacherType = Attacher::AttachEngine3D
  FirstAngle = 0
  Height = 10
  Placement = pos=(16.5,10,-2) rot=(0,0,1;0rad)
  Radius = 4.25
  SecondAngle = 0
FEATURE [Part::Cylinder] Cylinder245  label="Zylinder247"
  Angle = 360
  AttacherType = Attacher::AttachEngine3D
  FirstAngle = 0
  Height = 3
  Placement = pos=(16.5,10,9.5) rot=(0,0,1;0rad)
  Radius = 3
  SecondAngle = 0
FEATURE [Part::MultiFuse] Fusion163
  Shapes = -> [Cylinder243,Cylinder244,Wedge005,Box165,Cylinder242,Cylinder245]
FEATURE [PartDesign::Pad] Pad020
  AllowMultiFace = false
  Direction = (1,1,1)
  Length = 10
  Length2 = 100
  Placement = pos=(0,0,0) rot=(0.57735,0.57735,0.57735;2.0944rad)
  Profile = -> Sketch020
  Type = 0
FEATURE [Part::Chamfer] Chamfer024
  Base = -> Pad020
  Edges = 1 edges: [Edge21 r1=7 r2=50]
  Placement = pos=(11.5,0,0) rot=(0,0,1;0rad)
FEATURE [Part::Fillet] Fillet100
  Base = -> Chamfer024
  Edges = 1 edges r=1: [Edge4]
FEATURE [Part::Fillet] Fillet103
  Base = -> Fillet100
  Edges = 1 edges r=1: [Edge44]
FEATURE [Part::Fillet] Fillet101
  Base = -> Fillet103
  Edges = 2 edges r=4: [Edge16,Edge50]
FEATURE [Part::Cylinder] Cylinder246  label="Zylinder248"
  Angle = 360
  AttacherType = Attacher::AttachEngine3D
  FirstAngle = 0
  Height = 20
  Placement = pos=(16.5,23,-38.5) rot=(0,0,1;0rad)
  Radius = 0.6
  SecondAngle = 0
FEATURE [Part::MultiFuse] Fusion162
  Shapes = -> [Cylinder246,Fusion163]
FEATURE [Part::Cylinder] Cylinder247  label="Zylinder249"
  Angle = 360
  AttacherType = Attacher::AttachEngine3D
  FirstAngle = 0
  Height = 2.5
  Placement = pos=(16.5,23,-35.5) rot=(0,0,1;0rad)
  Radius = 1.4
  SecondAngle = 0
FEATURE [Part::Box] Box166  label="Würfel155"
  AttacherType = Attacher::AttachEngine3D
  Height = 0.5
  Length = 12
  Placement = pos=(10.5,2.5,4) rot=(0,0,1;0rad)
  Width = 16
FEATURE [Part::MultiFuse] Fusion164
  Shapes = -> [Cylinder247,Fillet101]
FEATURE [Part::Cut] Cut113
  Base = -> Fusion164
  Tool = -> Fusion162
FEATURE [Part::Cut] Cut114
  Base = -> Cut113
  Tool = -> Box166
FEATURE [Part::Fillet] Fillet102
  Base = -> Cut114
  Edges = 2 edges r=4: [Edge5,Edge37]
FEATURE [Part::Cut] Cut115
  Base = -> Cone
  Tool = -> Fillet102
FEATURE [Part::Cone] Cone001  label="Kegel001"
  Angle = 360
  AttacherType = Attacher::AttachEngine3D
  Height = 15
  Placement = pos=(20,-49,-50) rot=(0,0,1;0rad)
  Radius1 = 2
  Radius2 = 4
FEATURE [Sketcher::SketchObject] Sketch021
  FullyConstrained = false
  MapMode = 5
  Placement = pos=(0,0,0) rot=(0.57735,0.57735,0.57735;2.0944rad)
  Support = -> [YZ_Plane031]
  sketch-geometry (50):
    g0: LineSegment StartX=4 StartY=4 StartZ=0 EndX=4 EndY=10 EndZ=0
    g1: LineSegment StartX=4 StartY=10 StartZ=0 EndX=21 EndY=10 EndZ=0
    g2: LineSegment StartX=5 StartY=-29 StartZ=0 EndX=18 EndY=-29 EndZ=0
    g3: LineSegment StartX=5 StartY=-29 StartZ=0 EndX=5 EndY=-33 EndZ=0
    g4: LineSegment StartX=5 StartY=-33 StartZ=0 EndX=28 EndY=-33 EndZ=0
    g5: LineSegment StartX=4 StartY=4 StartZ=0 EndX=16 EndY=4 EndZ=0
    g6: LineSegment StartX=16 StartY=4 StartZ=0 EndX=21 EndY=6 EndZ=0
    g7: Circle CenterX=21 CenterY=10 CenterZ=0 NormalX=0 NormalY=0 NormalZ=1 AngleXU=0 Radius=2
    g8: Circle CenterX=33 CenterY=12 CenterZ=0 NormalX=0 NormalY=0 NormalZ=1 AngleXU=0 Radius=2
    g9: Circle CenterX=40 CenterY=18 CenterZ=0 NormalX=0 NormalY=0 NormalZ=1 AngleXU=0 Radius=2
    g10: BSplineCurve PolesCount=3 KnotsCount=2 Degree=2 IsPeriodic=0
    g11: GeomPoint X=21 Y=10 Z=0
    g12: GeomPoint X=40 Y=18 Z=0
    g13: Circle CenterX=40 CenterY=18 CenterZ=0 NormalX=0 NormalY=0 NormalZ=1 AngleXU=0 Radius=1
    g14: Circle CenterX=42 CenterY=12 CenterZ=0 NormalX=0 NormalY=0 NormalZ=1 AngleXU=0 Radius=1
    g15: Circle CenterX=49 CenterY=7 CenterZ=0 NormalX=0 NormalY=0 NormalZ=1 AngleXU=0 Radius=1
    g16: BSplineCurve PolesCount=3 KnotsCount=2 Degree=2 IsPeriodic=0
    g17: GeomPoint X=40 Y=18 Z=0
    g18: GeomPoint X=49 Y=7 Z=0
    g19: Circle CenterX=49 CenterY=7 CenterZ=0 NormalX=0 NormalY=0 NormalZ=1 AngleXU=0 Radius=8
    g20: Circle CenterX=50 CenterY=-43 CenterZ=0 NormalX=0 NormalY=0 NormalZ=1 AngleXU=0 Radius=8
    g21: BSplineCurve PolesCount=2 KnotsCount=2 Degree=1 IsPeriodic=0
    g22: GeomPoint X=49 Y=7 Z=0
    g23: GeomPoint X=50 Y=-43 Z=0
    g24: Circle CenterX=48 CenterY=-43 CenterZ=0 NormalX=0 NormalY=0 NormalZ=1 AngleXU=0 Radius=8
    g25: Circle CenterX=48 CenterY=10 CenterZ=0 NormalX=0 NormalY=0 NormalZ=1 AngleXU=0 Radius=8
    g26: Circle CenterX=38 CenterY=10 CenterZ=0 NormalX=0 NormalY=0 NormalZ=1 AngleXU=0 Radius=8
    g27: BSplineCurve PolesCount=3 KnotsCount=2 Degree=2 IsPeriodic=0
    g28: GeomPoint X=48 Y=-43 Z=0
    g29: GeomPoint X=38 Y=10 Z=0
    g30: LineSegment StartX=48 StartY=-43 StartZ=0 EndX=50 EndY=-43 EndZ=0
    g31: Circle CenterX=28 CenterY=-33 CenterZ=0 NormalX=0 NormalY=0 NormalZ=1 AngleXU=0 Radius=4
    g32: Circle CenterX=31.5452 CenterY=5.41621 CenterZ=0 NormalX=0 NormalY=0 NormalZ=1 AngleXU=0 Radius=4
    g33: Circle CenterX=38 CenterY=10 CenterZ=0 NormalX=0 NormalY=0 NormalZ=1 AngleXU=0 Radius=4
    g34: BSplineCurve PolesCount=3 KnotsCount=2 Degree=2 IsPeriodic=0
    g35: GeomPoint X=28 Y=-33 Z=0
    g36: GeomPoint X=38 Y=10 Z=0
    g37-g43: Circle x7 (B-spline internal-alignment scaffolding for g44; pole/knot coordinates omitted)
    g44: BSplineCurve PolesCount=7 KnotsCount=5 Degree=3 IsPeriodic=0
    g45-g49: GeomPoint x5 (B-spline internal-alignment scaffolding for g44; pole/knot coordinates omitted)
  constraints (42):
    c: Weight(g7) = 1
    c: Equal(g7,g8)
    c: Equal(g7,g9)
    c: InternalAlignment(g7,g10)
    c: InternalAlignment(g8,g10)
    c: InternalAlignment(g9,g10)
    c: InternalAlignment(g11,g10)
    c: InternalAlignment(g12,g10)
    c: Weight(g13) = 1
    c: Equal(g13,g14)
    c: Equal(g13,g15)
    c: InternalAlignment(g13,g16)
    c: InternalAlignment(g14,g16)
    c: InternalAlignment(g15,g16)
    c: InternalAlignment(g17,g16)
    c: InternalAlignment(g18,g16)
    c: Weight(g19) = 1
    c: Equal(g19,g20)
    c: InternalAlignment(g19,g21)
    c: InternalAlignment(g20,g21)
    c: InternalAlignment(g22,g21)
    c: InternalAlignment(g23,g21)
    c: Weight(g24) = 1
    c: Equal(g24,g25)
    c: Equal(g24,g26)
    c: InternalAlignment(g24,g27)
    c: InternalAlignment(g25,g27)
    c: InternalAlignment(g26,g27)
    c: InternalAlignment(g28,g27)
    c: InternalAlignment(g29,g27)
    c: Weight(g31) = 1
    c: Equal(g31,g32)
    c: Equal(g31,g33)
    c: InternalAlignment(g31,g34)
    c: InternalAlignment(g32,g34)
    c: InternalAlignment(g33,g34)
    c: InternalAlignment(g35,g34)
    c: InternalAlignment(g36,g34)
    c: Weight(g37) = 1
    c: Equal(g37, g38-g43) x6
    c: InternalAlignment(g37-g43 -> g44) x7
    c: InternalAlignment(g45-g49 -> g44) x5
FEATURE [Part::Wedge] Wedge006  label="Keil006"
  AttacherType = Attacher::AttachEngine3D
  Placement = pos=(12.5,10,0) rot=(0,0,1;0rad)
  X2max = 6
  X2min = 2
  Xmax = 8
  Xmin = 0
  Ymax = 18
  Ymin = 0
  Z2max = 8
  Z2min = 2
  Zmax = 8
  Zmin = 2
FEATURE [Part::Box] Box167  label="Würfel156"
  AttacherType = Attacher::AttachEngine3D
  Height = 7
  Length = 7
  Placement = pos=(13,1,1) rot=(0,0,1;0rad)
  Width = 9
FEATURE [Part::Cylinder] Cylinder248  label="Zylinder250"
  Angle = 360
  AttacherType = Attacher::AttachEngine3D
  FirstAngle = 0
  Height = 3
  Placement = pos=(16.5,10,9.5) rot=(0,0,1;0rad)
  Radius = 3
  SecondAngle = 0
FEATURE [Part::Cylinder] Cylinder249  label="Zylinder251"
  Angle = 360
  AttacherType = Attacher::AttachEngine3D
  FirstAngle = 0
  Height = 14
  Placement = pos=(16.5,10,-2) rot=(0,0,1;0rad)
  Radius = 1.5
  SecondAngle = 0
FEATURE [Part::Cylinder] Cylinder250  label="Zylinder252"
  Angle = 360
  AttacherType = Attacher::AttachEngine3D
  FirstAngle = 0
  Height = 10
  Placement = pos=(16.5,10,-31.5) rot=(0,0,1;0rad)
  Radius = 3.15
  SecondAngle = 0
FEATURE [Part::Cylinder] Cylinder251  label="Zylinder253"
  Angle = 360
  AttacherType = Attacher::AttachEngine3D
  FirstAngle = 0
  Height = 20
  Placement = pos=(16.5,23,-38.5) rot=(0,0,1;0rad)
  Radius = 0.6
  SecondAngle = 0
FEATURE [Part::Cylinder] Cylinder252  label="Zylinder254"
  Angle = 360
  AttacherType = Attacher::AttachEngine3D
  FirstAngle = 0
  Height = 2.5
  Placement = pos=(16.5,23,-35.5) rot=(0,0,1;0rad)
  Radius = 1.4
  SecondAngle = 0
FEATURE [Part::Cylinder] Cylinder253  label="Zylinder255"
  Angle = 360
  AttacherType = Attacher::AttachEngine3D
  FirstAngle = 0
  Height = 10
  Placement = pos=(16.5,10,-2) rot=(0,0,1;0rad)
  Radius = 4.25
  SecondAngle = 0
FEATURE [Part::MultiFuse] Fusion167
  Shapes = -> [Cylinder250,Cylinder253,Wedge006,Box167,Cylinder249,Cylinder248]
FEATURE [Part::MultiFuse] Fusion166
  Shapes = -> [Cylinder251,Fusion167]
FEATURE [Part::Box] Box168  label="Würfel157"
  AttacherType = Attacher::AttachEngine3D
  Height = 0.5
  Length = 12
  Placement = pos=(10.5,2.5,4) rot=(0,0,1;0rad)
  Width = 16
FEATURE [PartDesign::Pad] Pad021
  AllowMultiFace = false
  Direction = (1,1,1)
  Length = 10
  Length2 = 100
  Placement = pos=(0,0,0) rot=(0.57735,0.57735,0.57735;2.0944rad)
  Profile = -> Sketch021
  Type = 0
FEATURE [PartDesign::Body] Pad010Body001
  Group = -> [Sketch021,Pad021]
  Origin = -> Origin019
  Tip = -> Pad021
FEATURE [Part::Chamfer] Chamfer025
  Base = -> Pad010Body001
  Edges = 1 edges: [Edge21 r1=7 r2=50]
  Placement = pos=(11.5,0,0) rot=(0,0,1;0rad)
FEATURE [Part::Fillet] Fillet105
  Base = -> Chamfer025
  Edges = 1 edges r=1: [Edge4]
FEATURE [Part::Fillet] Fillet104
  Base = -> Fillet105
  Edges = 1 edges r=1: [Edge44]
FEATURE [Part::Fillet] Fillet106
  Base = -> Fillet104
  Edges = 2 edges r=4: [Edge16,Edge50]
FEATURE [Part::MultiFuse] Fusion165
  Shapes = -> [Cylinder252,Fillet106]
FEATURE [Part::Cut] Cut117
  Base = -> Fusion165
  Tool = -> Fusion166
FEATURE [Part::Cut] Cut116
  Base = -> Cut117
  Tool = -> Box168
FEATURE [Part::Fillet] Fillet107
  Base = -> Cut116
  Edges = 2 edges r=4: [Edge5,Edge37]
FEATURE [Part::Mirroring] Part__Mirroring006  label="Fillet070 (Mirror #2)001"
  Base = (16.5,-27,0)
  Normal = (0,0,1)
  Placement = pos=(0,0,0) rot=(1,0,0;3.14159rad)
  Source = -> Fillet107
FEATURE [App::DocumentObjectGroup] Gruppe028  label="feet"
  Group = -> [Cut115,Part__Mirroring006,Cone001,YZ_Plane030]
FEATURE [Part::Box] Box169  label="battery_2000"
  AttacherType = Attacher::AttachEngine3D
  Height = 5
  Length = 60
  Placement = pos=(-68,-18.5,-18) rot=(0,0,1;0rad)
  Width = 37
FEATURE [App::DocumentObjectGroup] Gruppe007  label="__unused"
  Group = -> [Fusion007,YZ_Plane004,Fusion064,Fusion067,Box066,Fusion100,Fusion051,Fusion106,Gruppe010,Box070,Chamfer022,Gruppe024,Box169]
FEATURE [Part::Box] Box170  label="Würfel159"
  AttacherType = Attacher::AttachEngine3D
  Height = 6
  Length = 60
  Placement = pos=(-65.5,-19,-18) rot=(0,0,1;0rad)
  Width = 38
FEATURE [Part::Fillet] Fillet108
  Base = -> Box170
  Edges = 4 edges r=1: [Edge9,Edge10,Edge11,Edge12]
  Placement = pos=(0,0,-4) rot=(0,0,1;0rad)
FEATURE [App::DocumentObjectGroup] Gruppe029  label="battery2"
  Group = -> [Box170,Fillet108]
FEATURE [Part::Box] Box171  label="Würfel160"
  AttacherType = Attacher::AttachEngine3D
  Height = 15
  Length = 15.5
  Placement = pos=(-60,17,-25) rot=(0,0,1;0rad)
  Width = 4
FEATURE [Part::Cylinder] Cylinder254  label="Zylinder256"
  Angle = 360
  AttacherType = Attacher::AttachEngine3D
  FirstAngle = 0
  Height = 15.5
  Placement = pos=(-52.5,20.5,-25.5) rot=(0,0,1;0rad)
  Radius = 4
  SecondAngle = 0
FEATURE [Part::Chamfer] Chamfer026
  Base = -> Box171
  Edges = 1 edges r=3: [Edge11]
FEATURE [Part::Box] Box172  label="Würfel161"
  AttacherType = Attacher::AttachEngine3D
  Height = 15
  Length = 15.5
  Placement = pos=(-60,-21,-25) rot=(0,0,1;0rad)
  Width = 4
FEATURE [Part::Cylinder] Cylinder255  label="Zylinder257"
  Angle = 360
  AttacherType = Attacher::AttachEngine3D
  FirstAngle = 0
  Height = 15.5
  Placement = pos=(-52.5,-20.5,-25.5) rot=(0,0,1;0rad)
  Radius = 4
  SecondAngle = 0
FEATURE [Part::Chamfer] Chamfer027
  Base = -> Box172
  Edges = 1 edges r=3: [Edge9]
FEATURE [Part::MultiFuse] Fusion168
  Shapes = -> [Cylinder254,Cylinder255]
FEATURE [Part::MultiFuse] Fusion169
  Shapes = -> [Chamfer026,Chamfer027]
FEATURE [Part::Box] Box173  label="Würfel162"
  AttacherType = Attacher::AttachEngine3D
  Height = 16.5
  Length = 10
  Placement = pos=(-34,10,-25.5) rot=(0,0,1;0rad)
  Width = 11
FEATURE [Part::Box] Box174  label="Würfel163"
  AttacherType = Attacher::AttachEngine3D
  Height = 16.5
  Length = 10
  Placement = pos=(-34,-21,-25.5) rot=(0,0,1;0rad)
  Width = 11
FEATURE [Part::Box] Box175  label="Würfel164"
  AttacherType = Attacher::AttachEngine3D
  Height = 4
  Length = 12.5
  Placement = pos=(-17,-21,-20) rot=(0,0,1;0rad)
  Width = 42
FEATURE [Part::Box] Box176  label="Würfel165"
  AttacherType = Attacher::AttachEngine3D
  Height = 10
  Length = 10
  Placement = pos=(-6,-3,-23.5) rot=(0,0,1;0rad)
  Width = 6
FEATURE [Part::Chamfer] Chamfer028
  Base = -> Box173
  Edges = 1 edges: [Edge11 r1=3 r2=8]
FEATURE [Part::Box] Box177  label="Würfel166"
  AttacherType = Attacher::AttachEngine3D
  Height = 9
  Length = 49
  Placement = pos=(-69.5,-19,-20.5) rot=(0,0,1;0rad)
  Width = 10
FEATURE [Part::Box] Box178  label="Würfel167"
  AttacherType = Attacher::AttachEngine3D
  Height = 9
  Length = 49
  Placement = pos=(-69.5,9,-20.5) rot=(0,0,1;0rad)
  Width = 10
FEATURE [Part::Chamfer] Chamfer029
  Base = -> Box178
  Edges = 1 edges: [Edge12 r1=5 r2=7]
FEATURE [Part::Chamfer] Chamfer030
  Base = -> Box177
  Edges = 1 edges: [Edge10 r1=5 r2=7]
FEATURE [Part::Chamfer] Chamfer031
  Base = -> Box174
  Edges = 1 edges: [Edge9 r1=3 r2=8]
FEATURE [Part::Box] Box179  label="Würfel168"
  AttacherType = Attacher::AttachEngine3D
  Height = 6
  Length = 60
  Placement = pos=(-65.5,-19,-18) rot=(0,0,1;0rad)
  Width = 38
FEATURE [Part::Fillet] Fillet109
  Base = -> Box179
  Edges = 4 edges r=1: [Edge9,Edge10,Edge11,Edge12]
  Placement = pos=(0,0,-4) rot=(0,0,1;0rad)
FEATURE [Part::MultiFuse] Fusion174
  Shapes = -> [Box176,Box175,Fusion168,Fillet109,Chamfer030,Chamfer029]
FEATURE [Part::MultiFuse] Fusion175
  Shapes = -> [Fusion169,Chamfer028,Chamfer031,Fusion147]
FEATURE [Part::Cut] Cut118
  Base = -> Fusion175
  Tool = -> Fusion174
FEATURE [App::DocumentObjectGroup] Gruppe006  label="bottom_rear"
  Group = -> [Cut118]
FEATURE [Part::Cylinder] Cylinder259  label="Zylinder261"
  Angle = 360
  AttacherType = Attacher::AttachEngine3D
  FirstAngle = 0
  Height = 14
  Placement = pos=(16.5,10,-2) rot=(0,0,1;0rad)
  Radius = 1.5
  SecondAngle = 0
FEATURE [Part::Cylinder] Cylinder260  label="Zylinder262"
  Angle = 360
  AttacherType = Attacher::AttachEngine3D
  FirstAngle = 0
  Height = 10
  Placement = pos=(16.5,10,-2) rot=(0,0,1;0rad)
  Radius = 4.25
  SecondAngle = 0
FEATURE [Part::Cylinder] Cylinder261  label="Zylinder263"
  Angle = 360
  AttacherType = Attacher::AttachEngine3D
  FirstAngle = 0
  Height = 3
  Placement = pos=(16.5,10,9.5) rot=(0,0,1;0rad)
  Radius = 3
  SecondAngle = 0
FEATURE [Part::Wedge] Wedge009  label="Keil009"
  AttacherType = Attacher::AttachEngine3D
  Placement = pos=(12.5,10,0) rot=(0,0,1;0rad)
  X2max = 6
  X2min = 2
  Xmax = 8
  Xmin = 0
  Ymax = 18
  Ymin = 0
  Z2max = 8
  Z2min = 2
  Zmax = 8
  Zmin = 2
FEATURE [Part::Wedge] Wedge010  label="Keil010"
  AttacherType = Attacher::AttachEngine3D
  Placement = pos=(20.5,10,0) rot=(0,0,1;3.14159rad)
  X2max = 6
  X2min = 2
  Xmax = 8
  Xmin = 0
  Ymax = 18
  Ymin = 0
  Z2max = 8
  Z2min = 2
  Zmax = 8
  Zmin = 2
FEATURE [Part::MultiFuse] Fusion177
  Placement = pos=(-23,-10,16) rot=(0,1,0;1.5708rad)
  Shapes = -> [Wedge010,Cylinder260,Cylinder259,Cylinder261,Wedge009]
FEATURE [Part::Box] Box180  label="Würfel169"
  AttacherType = Attacher::AttachEngine3D
  Height = 11
  Length = 7
  Placement = pos=(-20,-18,-5.5) rot=(0,0,1;0rad)
  Width = 36
FEATURE [Part::Chamfer] Chamfer033
  Base = -> Box180
  Edges = 2 edges: [Edge9 r1=4 r2=15,Edge11 r1=4 r2=15]
FEATURE [Part::Box] Box181  label="Würfel170"
  AttacherType = Attacher::AttachEngine3D
  Height = 19
  Length = 15
  Placement = pos=(-25.5,-30,-38) rot=(0,0,1;0rad)
  Width = 60
FEATURE [Part::Cut] Cut120
  Base = -> Chamfer033
  Tool = -> Fusion177
FEATURE [Part::Cylinder] Cylinder264  label="Zylinder266"
  Angle = 360
  AttacherType = Attacher::AttachEngine3D
  FirstAngle = 0
  Height = 2.5
  Placement = pos=(16.5,23,-35.5) rot=(0,0,1;0rad)
  Radius = 1.4
  SecondAngle = 0
FEATURE [Sketcher::SketchObject] Sketch022
  FullyConstrained = false
  MapMode = 5
  Placement = pos=(0,0,0) rot=(0.57735,0.57735,0.57735;2.0944rad)
  Support = -> [YZ_Plane033]
  sketch-geometry (50):
    g0: LineSegment StartX=4 StartY=4 StartZ=0 EndX=4 EndY=10 EndZ=0
    g1: LineSegment StartX=4 StartY=10 StartZ=0 EndX=21 EndY=10 EndZ=0
    g2: LineSegment StartX=5 StartY=-29 StartZ=0 EndX=18 EndY=-29 EndZ=0
    g3: LineSegment StartX=5 StartY=-29 StartZ=0 EndX=5 EndY=-33 EndZ=0
    g4: LineSegment StartX=5 StartY=-33 StartZ=0 EndX=28 EndY=-33 EndZ=0
    g5: LineSegment StartX=4 StartY=4 StartZ=0 EndX=16 EndY=4 EndZ=0
    g6: LineSegment StartX=16 StartY=4 StartZ=0 EndX=21 EndY=6 EndZ=0
    g7: Circle CenterX=21 CenterY=10 CenterZ=0 NormalX=0 NormalY=0 NormalZ=1 AngleXU=0 Radius=2
    g8: Circle CenterX=33 CenterY=12 CenterZ=0 NormalX=0 NormalY=0 NormalZ=1 AngleXU=0 Radius=2
    g9: Circle CenterX=40 CenterY=18 CenterZ=0 NormalX=0 NormalY=0 NormalZ=1 AngleXU=0 Radius=2
    g10: BSplineCurve PolesCount=3 KnotsCount=2 Degree=2 IsPeriodic=0
    g11: GeomPoint X=21 Y=10 Z=0
    g12: GeomPoint X=40 Y=18 Z=0
    g13: Circle CenterX=40 CenterY=18 CenterZ=0 NormalX=0 NormalY=0 NormalZ=1 AngleXU=0 Radius=1
    g14: Circle CenterX=42 CenterY=12 CenterZ=0 NormalX=0 NormalY=0 NormalZ=1 AngleXU=0 Radius=1
    g15: Circle CenterX=49 CenterY=7 CenterZ=0 NormalX=0 NormalY=0 NormalZ=1 AngleXU=0 Radius=1
    g16: BSplineCurve PolesCount=3 KnotsCount=2 Degree=2 IsPeriodic=0
    g17: GeomPoint X=40 Y=18 Z=0
    g18: GeomPoint X=49 Y=7 Z=0
    g19: Circle CenterX=49 CenterY=7 CenterZ=0 NormalX=0 NormalY=0 NormalZ=1 AngleXU=0 Radius=8
    g20: Circle CenterX=50 CenterY=-43 CenterZ=0 NormalX=0 NormalY=0 NormalZ=1 AngleXU=0 Radius=8
    g21: BSplineCurve PolesCount=2 KnotsCount=2 Degree=1 IsPeriodic=0
    g22: GeomPoint X=49 Y=7 Z=0
    g23: GeomPoint X=50 Y=-43 Z=0
    g24: Circle CenterX=48 CenterY=-43 CenterZ=0 NormalX=0 NormalY=0 NormalZ=1 AngleXU=0 Radius=8
    g25: Circle CenterX=48 CenterY=10 CenterZ=0 NormalX=0 NormalY=0 NormalZ=1 AngleXU=0 Radius=8
    g26: Circle CenterX=38 CenterY=10 CenterZ=0 NormalX=0 NormalY=0 NormalZ=1 AngleXU=0 Radius=8
    g27: BSplineCurve PolesCount=3 KnotsCount=2 Degree=2 IsPeriodic=0
    g28: GeomPoint X=48 Y=-43 Z=0
    g29: GeomPoint X=38 Y=10 Z=0
    g30: LineSegment StartX=48 StartY=-43 StartZ=0 EndX=50 EndY=-43 EndZ=0
    g31: Circle CenterX=28 CenterY=-33 CenterZ=0 NormalX=0 NormalY=0 NormalZ=1 AngleXU=0 Radius=4
    g32: Circle CenterX=31.5452 CenterY=5.41621 CenterZ=0 NormalX=0 NormalY=0 NormalZ=1 AngleXU=0 Radius=4
    g33: Circle CenterX=38 CenterY=10 CenterZ=0 NormalX=0 NormalY=0 NormalZ=1 AngleXU=0 Radius=4
    g34: BSplineCurve PolesCount=3 KnotsCount=2 Degree=2 IsPeriodic=0
    g35: GeomPoint X=28 Y=-33 Z=0
    g36: GeomPoint X=38 Y=10 Z=0
    g37-g43: Circle x7 (B-spline internal-alignment scaffolding for g44; pole/knot coordinates omitted)
    g44: BSplineCurve PolesCount=7 KnotsCount=5 Degree=3 IsPeriodic=0
    g45-g49: GeomPoint x5 (B-spline internal-alignment scaffolding for g44; pole/knot coordinates omitted)
  constraints (42):
    c: Weight(g7) = 1
    c: Equal(g7,g8)
    c: Equal(g7,g9)
    c: InternalAlignment(g7,g10)
    c: InternalAlignment(g8,g10)
    c: InternalAlignment(g9,g10)
    c: InternalAlignment(g11,g10)
    c: InternalAlignment(g12,g10)
    c: Weight(g13) = 1
    c: Equal(g13,g14)
    c: Equal(g13,g15)
    c: InternalAlignment(g13,g16)
    c: InternalAlignment(g14,g16)
    c: InternalAlignment(g15,g16)
    c: InternalAlignment(g17,g16)
    c: InternalAlignment(g18,g16)
    c: Weight(g19) = 1
    c: Equal(g19,g20)
    c: InternalAlignment(g19,g21)
    c: InternalAlignment(g20,g21)
    c: InternalAlignment(g22,g21)
    c: InternalAlignment(g23,g21)
    c: Weight(g24) = 1
    c: Equal(g24,g25)
    c: Equal(g24,g26)
    c: InternalAlignment(g24,g27)
    c: InternalAlignment(g25,g27)
    c: InternalAlignment(g26,g27)
    c: InternalAlignment(g28,g27)
    c: InternalAlignment(g29,g27)
    c: Weight(g31) = 1
    c: Equal(g31,g32)
    c: Equal(g31,g33)
    c: InternalAlignment(g31,g34)
    c: InternalAlignment(g32,g34)
    c: InternalAlignment(g33,g34)
    c: InternalAlignment(g35,g34)
    c: InternalAlignment(g36,g34)
    c: Weight(g37) = 1
    c: Equal(g37, g38-g43) x6
    c: InternalAlignment(g37-g43 -> g44) x7
    c: InternalAlignment(g45-g49 -> g44) x5
FEATURE [PartDesign::Pad] Pad022
  AllowMultiFace = false
  Direction = (1,1,1)
  Length = 10
  Length2 = 100
  Placement = pos=(0,0,0) rot=(0.57735,0.57735,0.57735;2.0944rad)
  Profile = -> Sketch022
  Type = 0
FEATURE [Part::Chamfer] Chamfer034
  Base = -> Pad022
  Edges = 1 edges: [Edge21 r1=7 r2=50]
  Placement = pos=(11.5,0,0) rot=(0,0,1;0rad)
FEATURE [Part::Fillet] Fillet111
  Base = -> Chamfer034
  Edges = 1 edges r=1: [Edge4]
FEATURE [Part::Fillet] Fillet112
  Base = -> Fillet111
  Edges = 1 edges r=1: [Edge44]
FEATURE [Part::Fillet] Fillet110
  Base = -> Fillet112
  Edges = 2 edges r=4: [Edge16,Edge50]
FEATURE [Part::MultiFuse] Fusion180
  Placement = pos=(-34.5,0,0) rot=(0,0,1;0rad)
  Shapes = -> [Cylinder264,Fillet110]
FEATURE [Part::Mirroring] Part__Mirroring  label="Fusion180 (Mirror #7)"
  Base = (0,0,0)
  Normal = (0,1,0)
  Source = -> Fusion180
FEATURE [Part::MultiFuse] Fusion181
  Shapes = -> [Cut120,Fusion180,Part__Mirroring]
FEATURE [Part::Cut] Cut121
  Base = -> Fusion181
  Tool = -> Box181
FEATURE [App::DocumentObjectGroup] Gruppe011  label="leg_centre"
  Group = -> [Cut121]
FEATURE [Part::Box] Box184  label="Würfel173"
  AttacherType = Attacher::AttachEngine3D
  Height = 12
  Length = 16
  Placement = pos=(28.5,-3.75,-11.5) rot=(0,0,1;0rad)
  Width = 7.5
FEATURE [Part::Box] Box185  label="Würfel174"
  AttacherType = Attacher::AttachEngine3D
  Height = 10
  Length = 22
  Placement = pos=(27,-3.5,-10.5) rot=(0,0,1;0rad)
  Width = 12
FEATURE [Part::Cylinder] Cylinder271  label="Zylinder273"
  Angle = 360
  AttacherType = Attacher::AttachEngine3D
  FirstAngle = 0
  Height = 15
  Placement = pos=(37.5,7.5,-5.5) rot=(1,0,0;1.5708rad)
  Radius = 2
  SecondAngle = 0
FEATURE [Part::MultiFuse] Fusion185
  Shapes = -> [Cylinder271,Box184]
FEATURE [Part::Fillet] Fillet120
  Base = -> Box185
  Edges = 2 edges r=4.9: [Edge6,Edge8]
  Placement = pos=(82,-2.5,-11) rot=(0,1,0;3.14159rad)
FEATURE [Part::Cut] Cut122
  Base = -> Fillet120
  Tool = -> Fusion185
FEATURE [Part::Box] Box186  label="Würfel175"
  AttacherType = Attacher::AttachEngine3D
  Height = 21.59
  Length = 2
  Placement = pos=(61.5,-4.5,-14) rot=(0,0,1;0rad)
  Width = 8.89
FEATURE [Part::Cylinder] Cylinder272  label="Zylinder274"
  Angle = 360
  AttacherType = Attacher::AttachEngine3D
  FirstAngle = 0
  Height = 18
  Placement = pos=(48,0,-11.55) rot=(0,1,0;1.5708rad)
  Radius = 1.5
  SecondAngle = 0
FEATURE [Part::FeaturePython] Tube  # WARN: FeaturePython — macro-defined, semantics opaque (R4)
  AttacherType = Attacher::AttachEngine3D
  Height = 10
  InnerRadius = 28
  OuterRadius = 35
  Placement = pos=(25.5,0,-17) rot=(0,0,1;0rad)
FEATURE [Part::Box] Box189  label="Würfel178"
  AttacherType = Attacher::AttachEngine3D
  Height = 12
  Length = 62
  Placement = pos=(-10.5,-37,-18) rot=(0,0,1;0rad)
  Width = 73
FEATURE [Part::Box] Box190  label="Würfel179"
  AttacherType = Attacher::AttachEngine3D
  Height = 12
  Length = 10
  Placement = pos=(47.5,-27.5,-18) rot=(0,0,1;0rad)
  Width = 10
FEATURE [Part::Box] Box191  label="Würfel180"
  AttacherType = Attacher::AttachEngine3D
  Height = 12
  Length = 10
  Placement = pos=(47.5,17.5,-18) rot=(0,0,1;0rad)
  Width = 10
FEATURE [Part::MultiFuse] Fusion186
  Shapes = -> [Box189,Box190,Box191]
FEATURE [Part::Cut] Cut126
  Base = -> Tube
  Tool = -> Fusion186
FEATURE [Part::Cylinder] Cylinder273  label="Zylinder275"
  Angle = 360
  AttacherType = Attacher::AttachEngine3D
  FirstAngle = 0
  Height = 10
  Placement = pos=(57,0,-11.55) rot=(0,1,0;1.5708rad)
  Radius = 1.5
  SecondAngle = 0
FEATURE [Part::Box] Box192  label="Würfel181"
  AttacherType = Attacher::AttachEngine3D
  Height = 21.59
  Length = 2
  Placement = pos=(61.5,-4.5,-14) rot=(0,0,1;0rad)
  Width = 8.89
FEATURE [Part::Cut] Cut127
  Base = -> Box192
  Placement = pos=(-2,0,0) rot=(0,0,1;0rad)
  Tool = -> Cylinder273
FEATURE [Part::MultiFuse] Fusion187
  Placement = pos=(-2,0,0) rot=(0,0,1;0rad)
  Shapes = -> [Box186,Cylinder272]
FEATURE [Part::Cylinder] Cylinder274  label="Zylinder276"
  Angle = 360
  AttacherType = Attacher::AttachEngine3D
  FirstAngle = 0
  Height = 10
  Placement = pos=(57,0,-11.55) rot=(0,1,0;1.5708rad)
  Radius = 1.5
  SecondAngle = 0
FEATURE [Part::Box] Box193  label="Würfel182"
  AttacherType = Attacher::AttachEngine3D
  Height = 21.59
  Length = 2
  Placement = pos=(61.5,-4.5,-14) rot=(0,0,1;0rad)
  Width = 8.89
FEATURE [Part::Cut] Cut128
  Base = -> Box193
  Placement = pos=(-0.210743,9.6543,0) rot=(0,0,-1;0.349066rad)
  Tool = -> Cylinder274
FEATURE [Part::Cylinder] Cylinder275  label="Zylinder277"
  Angle = 360
  AttacherType = Attacher::AttachEngine3D
  FirstAngle = 0
  Height = 18
  Placement = pos=(48,0,-11.55) rot=(0,1,0;1.5708rad)
  Radius = 1.5
  SecondAngle = 0
FEATURE [Part::Box] Box194  label="Würfel183"
  AttacherType = Attacher::AttachEngine3D
  Height = 21.59
  Length = 2
  Placement = pos=(61.5,-4.5,-14) rot=(0,0,1;0rad)
  Width = 8.89
FEATURE [Part::MultiFuse] Fusion188
  Placement = pos=(-0.210743,9.6543,0) rot=(0,0,-1;0.349066rad)
  Shapes = -> [Box194,Cylinder275]
FEATURE [Part::Cylinder] Cylinder276  label="Zylinder278"
  Angle = 360
  AttacherType = Attacher::AttachEngine3D
  FirstAngle = 0
  Height = 18
  Placement = pos=(48,0,-11.55) rot=(0,1,0;1.5708rad)
  Radius = 1.5
  SecondAngle = 0
FEATURE [Part::Box] Box195  label="Würfel184"
  AttacherType = Attacher::AttachEngine3D
  Height = 21.59
  Length = 2
  Placement = pos=(61.5,-4.5,-14) rot=(0,0,1;0rad)
  Width = 8.89
FEATURE [Part::MultiFuse] Fusion189
  Placement = pos=(-0.210743,9.6543,0) rot=(0,0,-1;0.349066rad)
  Shapes = -> [Box195,Cylinder276]
FEATURE [Part::Cylinder] Cylinder277  label="Zylinder279"
  Angle = 360
  AttacherType = Attacher::AttachEngine3D
  FirstAngle = 0
  Height = 10
  Placement = pos=(57,0,-11.55) rot=(0,1,0;1.5708rad)
  Radius = 1.5
  SecondAngle = 0
FEATURE [Part::Box] Box196  label="Würfel185"
  AttacherType = Attacher::AttachEngine3D
  Height = 21.59
  Length = 2
  Placement = pos=(61.5,-4.5,-14) rot=(0,0,1;0rad)
  Width = 8.89
FEATURE [Part::Cut] Cut129
  Base = -> Box196
  Placement = pos=(-0.210743,9.6543,0) rot=(0,0,-1;0.349066rad)
  Tool = -> Cylinder277
FEATURE [Part::Mirroring] Part__Mirroring007  label="Fusion189 (Mirror #8)"
  Base = (0,0,0)
  Normal = (0,1,0)
  Source = -> Fusion189
FEATURE [Part::Mirroring] Part__Mirroring008  label="Cut129 (Mirror #9)"
  Base = (0,0,0)
  Normal = (0,1,0)
  Source = -> Cut129
FEATURE [Part::Chamfer] Chamfer035
  Base = -> Cut122
  Edges = 1 edges r=6.5: [Edge22]
FEATURE [Part::Cylinder] Cylinder279  label="Zylinder281"
  Angle = 360
  AttacherType = Attacher::AttachEngine3D
  FirstAngle = 0
  Height = 8
  Placement = pos=(46.7638,7.51754,-11.55) rot=(-0.171088,0.970288,0.171088;1.60095rad)
  Radius = 3
  SecondAngle = 0
FEATURE [Part::Mirroring] Part__Mirroring009  label="Zylinder281 (Mirror #10)"
  Base = (0,0,0)
  Normal = (0,1,0)
  Source = -> Cylinder279
FEATURE [Part::Cylinder] Cylinder280  label="Zylinder282"
  Angle = 360
  AttacherType = Attacher::AttachEngine3D
  FirstAngle = 0
  Height = 12
  Placement = pos=(44,0,-11.55) rot=(0,1,0;1.5708rad)
  Radius = 3
  SecondAngle = 0
FEATURE [Part::Cylinder] Cylinder281  label="Zylinder283"
  Angle = 360
  AttacherType = Attacher::AttachEngine3D
  FirstAngle = 0
  Height = 8
  Placement = pos=(46.7638,7.51754,-11.55) rot=(-0.171088,0.970288,0.171088;1.60095rad)
  Radius = 3
  SecondAngle = 0
FEATURE [Part::MultiFuse] Fusion193
  Shapes = -> [Fusion187,Fusion188,Part__Mirroring007]
FEATURE [Part::MultiFuse] Fusion194  label="tof_boards"
  Placement = pos=(4.58307,0,12.5919) rot=(0,1,0;0.349066rad)
  Shapes = -> [Cut127,Cut128,Part__Mirroring008]
FEATURE [Part::MultiFuse] Fusion195
  Shapes = -> [Part__Mirroring009,Cylinder280,Cylinder281]
FEATURE [Part::Cut] Cut130
  Base = -> Cut126
  Tool = -> Fusion195
FEATURE [Part::Cut] Cut131
  Base = -> Cut130
  Tool = -> Fusion193
FEATURE [Part::Cylinder] Cylinder282  label="Zylinder284"
  Angle = 360
  AttacherType = Attacher::AttachEngine3D
  FirstAngle = 0
  Height = 12
  Placement = pos=(44,0,-11.55) rot=(0,1,0;1.5708rad)
  Radius = 3
  SecondAngle = 0
FEATURE [Part::Cut] Cut132
  Base = -> Chamfer035
  Tool = -> Cylinder282
FEATURE [Part::MultiFuse] Fusion196  label="sensor_tof"
  Placement = pos=(4.16867,0,12.4767) rot=(0,1,0;0.349066rad)
  Shapes = -> [Cut131,Cut132]
FEATURE [Part::Box] Box197  label="Würfel186"
  AttacherType = Attacher::AttachEngine3D
  Height = 8
  Length = 21
  Placement = pos=(0,0,26.5) rot=(0,0,1;0rad)
  Width = 19
FEATURE [Part::Cylinder] Cylinder294  label="Zylinder296"
  Angle = 360
  AttacherType = Attacher::AttachEngine3D
  FirstAngle = 0
  Height = 7
  Placement = pos=(23.75,13,16) rot=(0,0,1;0rad)
  Radius = 8
  SecondAngle = 0
FEATURE [Part::Box] Box220  label="Würfel208"
  AttacherType = Attacher::AttachEngine3D
  Height = 8
  Length = 28
  Placement = pos=(-3,5,26.5) rot=(0,0,1;0rad)
  Width = 1
FEATURE [Part::Cylinder] Cylinder295  label="Zylinder297"
  Angle = 360
  AttacherType = Attacher::AttachEngine3D
  FirstAngle = 0
  Height = 7
  Placement = pos=(23.75,-13,16) rot=(0,0,1;0rad)
  Radius = 8
  SecondAngle = 0
FEATURE [Part::Box] Box221  label="Würfel209"
  AttacherType = Attacher::AttachEngine3D
  Height = 5.5
  Length = 18
  Placement = pos=(14.5,-13.5,15) rot=(0,0,1;0rad)
  Width = 27
FEATURE [Part::Box] Box222  label="Würfel210"
  AttacherType = Attacher::AttachEngine3D
  Height = 3
  Length = 10
  Placement = pos=(8.75,-22.5,17.5) rot=(0,0,1;0rad)
  Width = 44
FEATURE [Part::Box] Box223  label="Würfel211"
  AttacherType = Attacher::AttachEngine3D
  Height = 2.5
  Length = 13
  Placement = pos=(18.75,-13.5,20.5) rot=(0,0,1;0rad)
  Width = 27
FEATURE [Part::MultiFuse] Fusion206  label="MiniServo"
  Shapes = -> [Box197,Box220]
FEATURE [Part::Cylinder] Cylinder296  label="Zylinder298"
  Angle = 360
  AttacherType = Attacher::AttachEngine3D
  FirstAngle = 0
  Height = 10
  Placement = pos=(25.5,-17.5,12.25) rot=(0,0,1;0rad)
  Radius = 1.6
  SecondAngle = 0
FEATURE [Part::Cylinder] Cylinder297  label="Zylinder299"
  Angle = 360
  AttacherType = Attacher::AttachEngine3D
  FirstAngle = 0
  Height = 10
  Placement = pos=(25.5,17.5,13) rot=(0,0,1;0rad)
  Radius = 1.6
  SecondAngle = 0
FEATURE [Part::Box] Box224  label="board005"
  AttacherType = Attacher::AttachEngine3D
  Height = 4
  Length = 69.8
  Placement = pos=(-42.5,-19.4,16) rot=(0,0,1;0rad)
  Width = 38.8
FEATURE [Part::Cylinder] Cylinder298  label="Zylinder300"
  Angle = 360
  AttacherType = Attacher::AttachEngine3D
  FirstAngle = 0
  Height = 20
  Placement = pos=(22.5,23,30.5) rot=(1,0,0;1.5708rad)
  Radius = 1
  SecondAngle = 0
FEATURE [Part::Cylinder] Cylinder299  label="Zylinder301"
  Angle = 360
  AttacherType = Attacher::AttachEngine3D
  FirstAngle = 0
  Height = 20
  Placement = pos=(-1.5,23,30.5) rot=(1,0,0;1.5708rad)
  Radius = 1
  SecondAngle = 0
FEATURE [Part::MultiFuse] Fusion207
  Placement = pos=(19.5,1,-3.75) rot=(0,0,1;0rad)
  Shapes = -> [Fusion206,Cylinder298,Cylinder299]
FEATURE [Part::Box] Box225  label="Würfel212"
  AttacherType = Attacher::AttachEngine3D
  Height = 9
  Length = 31
  Placement = pos=(14.5,7,20.75) rot=(0,0,1;0rad)
  Width = 15
FEATURE [Part::Cylinder] Cylinder300  label="Zylinder302"
  Angle = 360
  AttacherType = Attacher::AttachEngine3D
  FirstAngle = 0
  Height = 10
  Placement = pos=(25.5,-17.5,21.5) rot=(0,0,1;0rad)
  Radius = 2.6
  SecondAngle = 0
FEATURE [Part::Cylinder] Cylinder301  label="Zylinder303"
  Angle = 360
  AttacherType = Attacher::AttachEngine3D
  FirstAngle = 0
  Height = 10
  Placement = pos=(25.5,17.5,21.5) rot=(0,0,1;0rad)
  Radius = 2.6
  SecondAngle = 0
FEATURE [Part::Fillet] Fillet121
  Base = -> Box225
  Edges = 2 edges r=3: [Edge3,Edge7]
FEATURE [Part::MultiFuse] Fusion205
  Shapes = -> [Box223,Cylinder295,Cylinder294,Fillet121]
FEATURE [Part::Box] Box226  label="Würfel213"
  AttacherType = Attacher::AttachEngine3D
  Height = 6
  Length = 11
  Placement = pos=(10.5,-22.5,17.5) rot=(0,0,1;0rad)
  Width = 17
FEATURE [Part::Box] Box227  label="Würfel214"
  AttacherType = Attacher::AttachEngine3D
  Height = 11
  Length = 4
  Placement = pos=(36.5,18.25,23.5) rot=(0,0,1;0rad)
  Width = 8
FEATURE [Mesh::Feature] hexbug_adapter_2_b_arm
  Placement = pos=(78.25,4,30.75) rot=(0,0,1;0rad)
FEATURE [App::DocumentObjectGroup] Gruppe017  label="__other"
  Group = -> [Part002,Part,Gruppe018,Gruppe019,Gruppe020,Gruppe021,Gruppe022,Gruppe026,hexbug_adapter_2_b_arm]
FEATURE [Part::Box] Box230  label="Würfel217"
  AttacherType = Attacher::AttachEngine3D
  Height = 10
  Length = 20.75
  Placement = pos=(17.5,-10.25,32.25) rot=(0,0,1;0rad)
  Width = 9.25
FEATURE [Part::Cylinder] Cylinder309  label="Zylinder311"
  Angle = 360
  AttacherType = Attacher::AttachEngine3D
  FirstAngle = 0
  Height = 10
  Placement = pos=(14,-13.75,33.25) rot=(0,0,1;0rad)
  Radius = 1.6
  SecondAngle = 0
FEATURE [Part::Cylinder] Cylinder310  label="Zylinder312"
  Angle = 360
  AttacherType = Attacher::AttachEngine3D
  FirstAngle = 0
  Height = 10
  Placement = pos=(35,-13.75,33.25) rot=(0,0,1;0rad)
  Radius = 1.6
  SecondAngle = 0
FEATURE [Part::Box] Box231  label="Würfel218"
  AttacherType = Attacher::AttachEngine3D
  Height = 2
  Length = 26
  Placement = pos=(12,-16,41.5) rot=(0,0,1;0rad)
  Width = 15
FEATURE [Part::Box] Box232  label="Würfel219"
  AttacherType = Attacher::AttachEngine3D
  Height = 10
  Length = 10
  Placement = pos=(28.75,-6.75,16.25) rot=(0,0,1;0rad)
  Width = 10
FEATURE [Part::MultiFuse] Fusion204
  Shapes = -> [Box222,Box221,Cylinder296,Cylinder297,Box224,Cylinder300,Cylinder301,Box226,Box227,Box232]
FEATURE [Part::Cut] Cut140
  Base = -> Fusion205
  Tool = -> Fusion204
FEATURE [Part::Cut] Cut141
  Base = -> Cut140
  Placement = pos=(0,0,2) rot=(0,0,1;0rad)
  Tool = -> Fusion207
FEATURE [App::DocumentObjectGroup] Gruppe030  label="sensor_holder_front"
  Group = -> [Cut141]
FEATURE [Part::MultiFuse] Fusion209
  Placement = pos=(0.5,0,5) rot=(0,0,1;0rad)
  Shapes = -> [Cylinder309,Cylinder310]
FEATURE [Part::Cylinder] Cylinder311  label="Zylinder313"
  Angle = 360
  AttacherType = Attacher::AttachEngine3D
  FirstAngle = 0
  Height = 24
  Placement = pos=(16.5,-14.1361,32.7038) rot=(0.57735,-0.57735,0.57735;4.18879rad)
  Radius = 9
  SecondAngle = 0
FEATURE [Part::Cylinder] Cylinder312  label="Zylinder314"
  Angle = 360
  AttacherType = Attacher::AttachEngine3D
  FirstAngle = 0
  Height = 17
  Placement = pos=(16,3.36386,32.4538) rot=(0,0.707107,-0.707107;3.14159rad)
  Radius = 9
  SecondAngle = 0
FEATURE [Part::Cylinder] Cylinder313  label="Zylinder315"
  Angle = 360
  AttacherType = Attacher::AttachEngine3D
  FirstAngle = 0
  Height = 10
  Placement = pos=(38.25,-5,36.25) rot=(1,0,0;1.5708rad)
  Radius = 2
  SecondAngle = 0
FEATURE [Part::Cut] Cut144
  Base = -> Box231
  Placement = pos=(0,1.75,0) rot=(0,0,1;0rad)
  Tool = -> Fusion209
FEATURE [Part::Fillet] Fillet122
  Base = -> Cut144
  Edges = 2 edges r=3: [Edge1,Edge6]
  Placement = pos=(-4.75,0,0) rot=(0,0,1;0rad)
FEATURE [Part::Cylinder] Cylinder315  label="Zylinder317"
  Angle = 360
  AttacherType = Attacher::AttachEngine3D
  FirstAngle = 0
  Height = 10
  Placement = pos=(38.25,5.75,36.25) rot=(1,0,0;1.5708rad)
  Radius = 3
  SecondAngle = 0
FEATURE [Part::Cylinder] Cylinder316  label="Zylinder318"
  Angle = 360
  AttacherType = Attacher::AttachEngine3D
  FirstAngle = 0
  Height = 4
  Placement = pos=(38.25,-1,36.25) rot=(1,0,0;1.5708rad)
  Radius = 4
  SecondAngle = 0
FEATURE [Part::Box] Box233  label="Würfel220"
  AttacherType = Attacher::AttachEngine3D
  Height = 8
  Length = 12
  Placement = pos=(26.25,-5,32.25) rot=(0,0,1;0rad)
  Width = 4
FEATURE [Part::Box] Box234  label="Würfel221"
  AttacherType = Attacher::AttachEngine3D
  Height = 3.5
  Length = 21
  Placement = pos=(22.5,-4.25,34.5) rot=(0,0,1;0rad)
  Width = 7
FEATURE [Part::Cylinder] Cylinder317  label="Zylinder319"
  Angle = 360
  AttacherType = Attacher::AttachEngine3D
  FirstAngle = 0
  Height = 10
  Placement = pos=(38.25,3.25,36.25) rot=(1,0,0;1.5708rad)
  Radius = 1.25
  SecondAngle = 0
FEATURE [Part::MultiFuse] Fusion210
  Shapes = -> [Cylinder311,Cylinder312]
FEATURE [Part::MultiFuse] Fusion211
  Shapes = -> [Box233,Box230,Cylinder316]
FEATURE [Part::Cylinder] Cylinder318  label="Zylinder320"
  Angle = 360
  AttacherType = Attacher::AttachEngine3D
  FirstAngle = 0
  Height = 10
  Placement = pos=(38.25,-0.5,46.25) rot=(1,0,0;1.5708rad)
  Radius = 6
  SecondAngle = 0
FEATURE [Part::MultiFuse] Fusion212
  Shapes = -> [Cylinder313,Cylinder315,Box234,Cylinder317,Cylinder318]
FEATURE [Part::Cut] Cut145
  Base = -> Fusion211
  Tool = -> Fusion212
FEATURE [Part::Cut] Cut146
  Base = -> Cut145
  Tool = -> Fusion210
FEATURE [Part::MultiFuse] Fusion213
  Shapes = -> [Fillet122,Cut146]
FEATURE [Part::Box] Box235  label="Würfel222"
  AttacherType = Attacher::AttachEngine3D
  Height = 10
  Length = 10
  Placement = pos=(-45,-21,17.5) rot=(0,0,1;0rad)
  Width = 42
FEATURE [Part::Cylinder] Cylinder319  label="Zylinder321"
  Angle = 360
  AttacherType = Attacher::AttachEngine3D
  FirstAngle = 0
  Height = 15
  Placement = pos=(-40.5,-17.5,12.25) rot=(0,0,1;0rad)
  Radius = 1.6
  SecondAngle = 0
FEATURE [Part::Cylinder] Cylinder320  label="Zylinder322"
  Angle = 360
  AttacherType = Attacher::AttachEngine3D
  FirstAngle = 0
  Height = 14
  Placement = pos=(-40.5,17.5,13) rot=(0,0,1;0rad)
  Radius = 1.6
  SecondAngle = 0
FEATURE [Part::Fillet] Fillet123
  Base = -> Box235
  Edges = 2 edges r=2: [Edge10,Edge12]
FEATURE [Part::Cylinder] Cylinder321  label="Zylinder323"
  Angle = 360
  AttacherType = Attacher::AttachEngine3D
  FirstAngle = 0
  Height = 10
  Placement = pos=(-40.5,17.5,24) rot=(0,0,1;0rad)
  Radius = 2.6
  SecondAngle = 0
FEATURE [Part::Cylinder] Cylinder322  label="Zylinder324"
  Angle = 360
  AttacherType = Attacher::AttachEngine3D
  FirstAngle = 0
  Height = 10
  Placement = pos=(-40.5,-17.5,24) rot=(0,0,1;0rad)
  Radius = 2.6
  SecondAngle = 0
FEATURE [Part::Box] Box236  label="Würfel223"
  AttacherType = Attacher::AttachEngine3D
  Height = 10
  Length = 25
  Placement = pos=(7.75,-8.25,42) rot=(0,0,1;0rad)
  Width = 10
FEATURE [Part::Cut] Cut147
  Base = -> Fusion213
  Tool = -> Box236
FEATURE [Part::Cylinder] Cylinder323  label="Zylinder325"
  Angle = 360
  AttacherType = Attacher::AttachEngine3D
  FirstAngle = 0
  Height = 20
  Placement = pos=(22.5,23,30.5) rot=(1,0,0;1.5708rad)
  Radius = 1
  SecondAngle = 0
FEATURE [Part::Cylinder] Cylinder324  label="Zylinder326"
  Angle = 360
  AttacherType = Attacher::AttachEngine3D
  FirstAngle = 0
  Height = 20
  Placement = pos=(-1.5,23,30.5) rot=(1,0,0;1.5708rad)
  Radius = 1
  SecondAngle = 0
FEATURE [Part::Box] Box237  label="Würfel224"
  AttacherType = Attacher::AttachEngine3D
  Height = 8
  Length = 21
  Placement = pos=(0,0,26.5) rot=(0,0,1;0rad)
  Width = 19
FEATURE [Part::Box] Box238  label="Würfel225"
  AttacherType = Attacher::AttachEngine3D
  Height = 8
  Length = 28
  Placement = pos=(-3,5,26.5) rot=(0,0,1;0rad)
  Width = 1
FEATURE [Part::MultiFuse] Fusion214  label="MiniServo001"
  Shapes = -> [Box237,Box238]
FEATURE [Part::MultiFuse] Fusion215
  Shapes = -> [Cylinder324,Cylinder323]
FEATURE [Part::Cut] Cut148  label="miniServo"
  Base = -> Fusion214
  Placement = pos=(19.5,0,-1.75) rot=(0,0,1;0rad)
  Tool = -> Fusion215
FEATURE [Part::Box] Box239  label="Würfel226"
  AttacherType = Attacher::AttachEngine3D
  Height = 10
  Length = 25
  Placement = pos=(10.0314,-8.25,26.4316) rot=(0,1,0;0.174533rad)
  Width = 10
FEATURE [Part::Cut] Cut149
  Base = -> Cut147
  Tool = -> Box239
FEATURE [App::DocumentObjectGroup] Gruppe031  label="Screen_holder"
  Group = -> [Cut144,Cut149]
FEATURE [Part::Box] Box240  label="Würfel227"
  AttacherType = Attacher::AttachEngine3D
  Height = 8.5
  Length = 12
  Placement = pos=(-46,-15.25,17.5) rot=(0,0,1;0rad)
  Width = 30.5
FEATURE [Part::Cylinder] Cylinder325  label="Zylinder327"
  Angle = 360
  AttacherType = Attacher::AttachEngine3D
  FirstAngle = 0
  Height = 18
  Placement = pos=(-40.5,-17.5,12.25) rot=(0,0,1;0rad)
  Radius = 2
  SecondAngle = 0
FEATURE [Part::Cylinder] Cylinder326  label="Zylinder328"
  Angle = 360
  AttacherType = Attacher::AttachEngine3D
  FirstAngle = 0
  Height = 18
  Placement = pos=(-40.5,-2,12.25) rot=(0,0,1;0rad)
  Radius = 2
  SecondAngle = 0
FEATURE [Part::MultiFuse] Fusion217
  Placement = pos=(0,9.75,0) rot=(0,0,1;0rad)
  Shapes = -> [Cylinder325,Cylinder326]
FEATURE [Part::Box] Box241  label="board006"
  AttacherType = Attacher::AttachEngine3D
  Height = 4
  Length = 69.8
  Placement = pos=(-43,-19.6,16) rot=(0,0,1;0rad)
  Width = 39.2
FEATURE [Part::MultiFuse] Fusion216
  Shapes = -> [Box240,Cylinder322,Cylinder321,Cylinder320,Cylinder319,Fusion217,Box241]
FEATURE [Part::Cut] Cut150
  Base = -> Fillet123
  Placement = pos=(0,0,0.5) rot=(0,0,1;0rad)
  Tool = -> Fusion216
FEATURE [App::DocumentObjectGroup] Gruppe032  label="sensor_bank"
  Group = -> [Cut150]
FEATURE [Part::Box] Box242  label="Würfel228"
  AttacherType = Attacher::AttachEngine3D
  Height = 11
  Length = 10
  Placement = pos=(-53.5,-12,8) rot=(0,0,1;0rad)
  Width = 24
FEATURE [Part::Cut] Cut151
  Base = -> Cut108
  Tool = -> Box242
FEATURE [Part::Box] Box243  label="Würfel229"
  AttacherType = Attacher::AttachEngine3D
  Height = 25
  Length = 6
  Placement = pos=(-11.5,-23,-7) rot=(0,0,1;0rad)
  Width = 2
FEATURE [Part::Box] Box244  label="Würfel230"
  AttacherType = Attacher::AttachEngine3D
  Height = 4.5
  Length = 7
  Placement = pos=(-12,-21.25,-7.75) rot=(0,0,1;0rad)
  Width = 1.5
FEATURE [Part::Box] Box245  label="Würfel231"
  AttacherType = Attacher::AttachEngine3D
  Height = 25
  Length = 6
  Placement = pos=(-11.5,21,-7) rot=(0,0,1;0rad)
  Width = 2
FEATURE [Part::Fillet] Fillet124
  Base = -> Box245
  Edges = 2 edges r=1.5: [Edge11,Edge12]
FEATURE [Part::Fillet] Fillet125
  Base = -> Box243
  Edges = 2 edges r=1.5: [Edge9,Edge10]
FEATURE [Part::Box] Box246  label="Würfel232"
  AttacherType = Attacher::AttachEngine3D
  Height = 4.5
  Length = 7
  Placement = pos=(-12,19.75,-7.75) rot=(0,0,1;0rad)
  Width = 1.5
FEATURE [Part::MultiFuse] Fusion218
  Shapes = -> [Box244,Box246]
FEATURE [Part::MultiFuse] Fusion219
  Shapes = -> [Cut151,Fillet124,Fillet125]
FEATURE [Part::Cut] Cut152
  Base = -> Fusion219
  Tool = -> Fusion218
FEATURE [App::DocumentObjectGroup] Gruppe015  label="board_carrier"
  Group = -> [Box243,Box245,Cut152]
